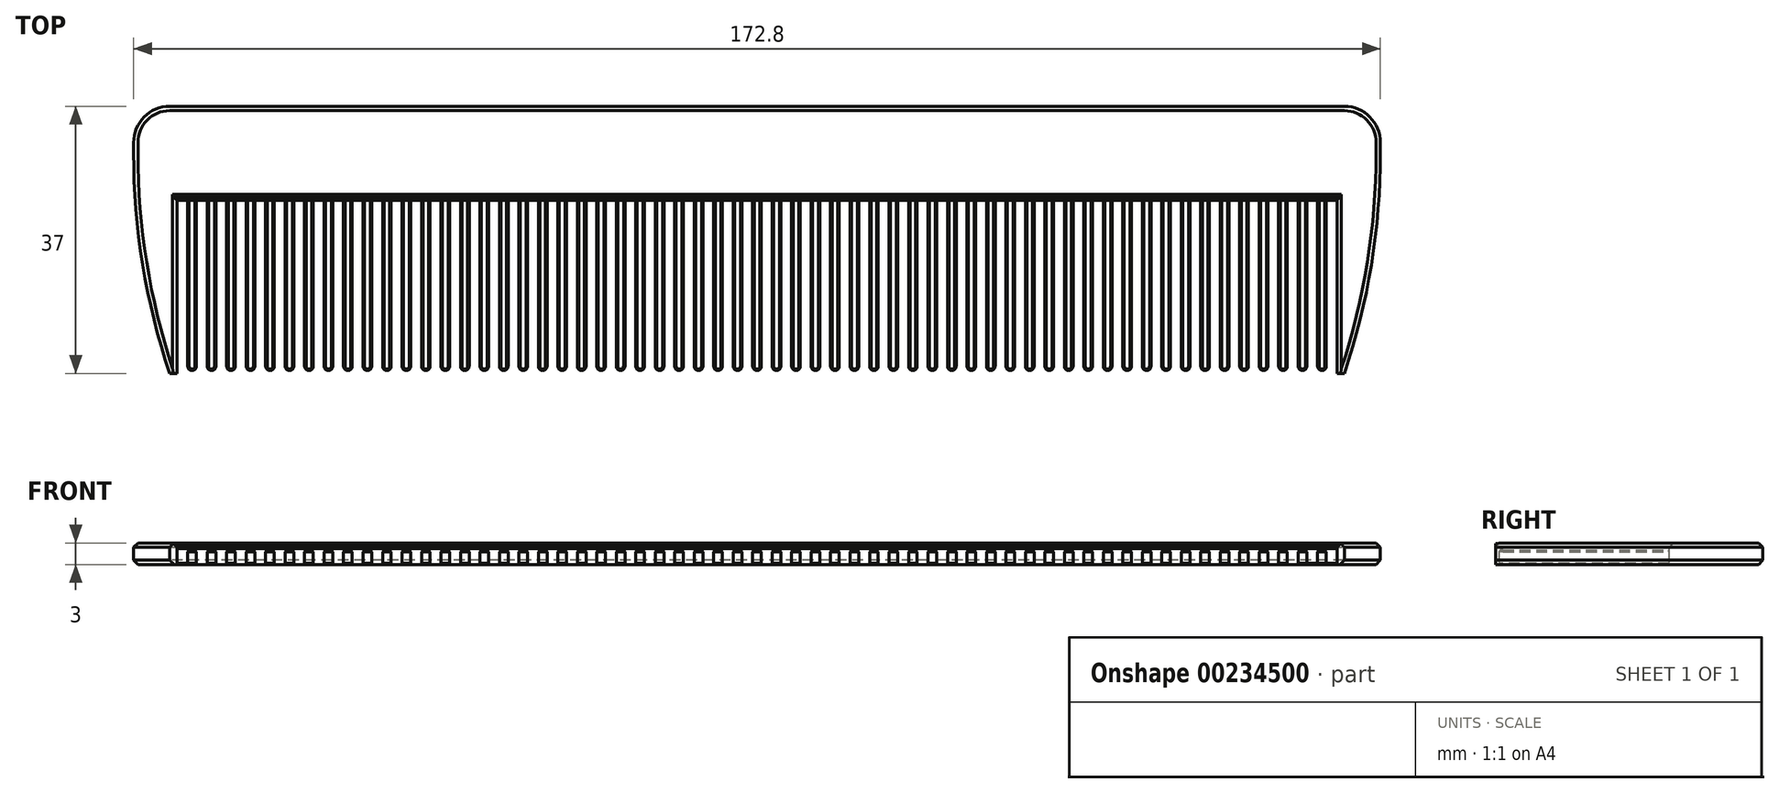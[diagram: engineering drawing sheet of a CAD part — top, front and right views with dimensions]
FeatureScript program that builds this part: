
annotation { "Feature Type Name" : "Feature", "Feature Type Description" : "" }
export const myFeature = defineFeature(function(context is Context, id is Id, definition is map)
    precondition{}
    {
        {
            var Q0;
            Q0=qCreatedBy(makeId("Top.planeOp"),FACE);
            var sketch = newSketch(context, id + "F0", { "sketchPlane" : qUnion([Q0])});
            skLineSegment(sketch, "E0.bottom", {"start": v(-80.4, 6.5) * mm, "end": v(80.4, 6.5) * mm});
            skLineSegment(sketch, "E0.top", {"start": v(-80.4, -6.5) * mm, "end": v(80.4, -6.5) * mm});
            skPoint(sketch, "E0.middle", {"position": v(0, 0) * mm});
            skLineSegment(sketch, "E1", {"start": v(-80.4, -6.5) * mm, "end": v(-80.4, -30.5) * mm});
            skLineSegment(sketch, "E2", {"start": v(-80.4, -30.5) * mm, "end": v(-81.4, -30.5) * mm});
            skArc(sketch, "E3", {"start": v(-81.4, -30.5) * mm, "mid": v(-85.14, -15.45) * mm, "end": v(-86.4, 0) * mm});
            skPoint(sketch, "E4", {"position": v(80.4, 0) * mm});
            skLineSegment(sketch, "E5", {"start": v(80.4, 0) * mm, "end": v(-80.4, 0) * mm, "construction": true});
            skLineSegment(sketch, "E6", {"start": v(-86.4, 0) * mm, "end": v(-86.4, 1.5) * mm});
            skLineSegment(sketch, "E7", {"start": v(-81.4, 6.5) * mm, "end": v(-80.4, 6.5) * mm});
            skPoint(sketch, "E8.visualSharp", {"position": v(-86.4, 6.5) * mm});
            skArc(sketch, "E8.filletArc", {"start": v(-81.4, 6.5) * mm, "mid": v(-84.94, 5.04) * mm, "end": v(-86.4, 1.5) * mm});
            skLineSegment(sketch, "E9", {"start": v(0, 0) * mm, "end": v(0, 6.5) * mm, "construction": true});
            skLineSegment(sketch, "E10.MirrorCS", {"start": v(80.4, -6.5) * mm, "end": v(80.4, -30.5) * mm});
            skLineSegment(sketch, "E11.MirrorCS", {"start": v(80.4, -30.5) * mm, "end": v(81.4, -30.5) * mm});
            skArc(sketch, "E12.MirrorCS", {"start": v(81.4, -30.5) * mm, "mid": v(85.14, -15.45) * mm, "end": v(86.4, 0) * mm});
            skArc(sketch, "E13.MirrorCS", {"start": v(81.4, 6.5) * mm, "mid": v(84.94, 5.04) * mm, "end": v(86.4, 1.5) * mm});
            skLineSegment(sketch, "E14.MirrorCS", {"start": v(86.4, 0) * mm, "end": v(86.4, 1.5) * mm});
            skLineSegment(sketch, "E15.MirrorCS", {"start": v(81.4, 6.5) * mm, "end": v(80.4, 6.5) * mm});
            skSolve(sketch);
        }
        {
            var Q0;
            Q0 = qSketchRegion(id + "F0", true);
            extrude(context, id + "F1", {"entities" : qUnion([Q0]), "depth" : 3 * mm});
        }
        {
            var Q0;
            Q0=qCreatedBy(makeId("Top.planeOp"),FACE);
            var sketch = newSketch(context, id + "F2", { "sketchPlane" : qUnion([Q0])});
            skLineSegment(sketch, "E16.bottom", {"start": v(-78.9, -6.5) * mm, "end": v(-77.7, -6.5) * mm});
            skLineSegment(sketch, "E16.left", {"start": v(-78.9, -6.5) * mm, "end": v(-78.9, -29.5) * mm});
            skLineSegment(sketch, "E16.right", {"start": v(-77.7, -6.5) * mm, "end": v(-77.7, -29.5) * mm});
            skArc(sketch, "E17", {"start": v(-78.9, -29.5) * mm, "mid": v(-78.3, -30.1) * mm, "end": v(-77.7, -29.5) * mm});
            skLineSegment(sketch, "E18.1.0.0", {"start": v(-76.2, -6.5) * mm, "end": v(-76.2, -29.5) * mm});
            skLineSegment(sketch, "E18.1.0.1", {"start": v(-75, -6.5) * mm, "end": v(-75, -29.5) * mm});
            skArc(sketch, "E18.1.0.2", {"start": v(-76.2, -29.5) * mm, "mid": v(-75.6, -30.1) * mm, "end": v(-75, -29.5) * mm});
            skLineSegment(sketch, "E18.1.0.3", {"start": v(-76.2, -6.5) * mm, "end": v(-75, -6.5) * mm});
            skLineSegment(sketch, "E18.2.0.0", {"start": v(-73.5, -6.5) * mm, "end": v(-73.5, -29.5) * mm});
            skLineSegment(sketch, "E18.2.0.1", {"start": v(-72.3, -6.5) * mm, "end": v(-72.3, -29.5) * mm});
            skArc(sketch, "E18.2.0.2", {"start": v(-73.5, -29.5) * mm, "mid": v(-72.9, -30.1) * mm, "end": v(-72.3, -29.5) * mm});
            skLineSegment(sketch, "E18.2.0.3", {"start": v(-73.5, -6.5) * mm, "end": v(-72.3, -6.5) * mm});
            skLineSegment(sketch, "E18.3.0.0", {"start": v(-70.8, -6.5) * mm, "end": v(-70.8, -29.5) * mm});
            skLineSegment(sketch, "E18.3.0.1", {"start": v(-69.6, -6.5) * mm, "end": v(-69.6, -29.5) * mm});
            skArc(sketch, "E18.3.0.2", {"start": v(-70.8, -29.5) * mm, "mid": v(-70.2, -30.1) * mm, "end": v(-69.6, -29.5) * mm});
            skLineSegment(sketch, "E18.3.0.3", {"start": v(-70.8, -6.5) * mm, "end": v(-69.6, -6.5) * mm});
            skLineSegment(sketch, "E18.4.0.0", {"start": v(-68.1, -6.5) * mm, "end": v(-68.1, -29.5) * mm});
            skLineSegment(sketch, "E18.4.0.1", {"start": v(-66.9, -6.5) * mm, "end": v(-66.9, -29.5) * mm});
            skArc(sketch, "E18.4.0.2", {"start": v(-68.1, -29.5) * mm, "mid": v(-67.5, -30.1) * mm, "end": v(-66.9, -29.5) * mm});
            skLineSegment(sketch, "E18.4.0.3", {"start": v(-68.1, -6.5) * mm, "end": v(-66.9, -6.5) * mm});
            skLineSegment(sketch, "E18.5.0.0", {"start": v(-65.4, -6.5) * mm, "end": v(-65.4, -29.5) * mm});
            skLineSegment(sketch, "E18.5.0.1", {"start": v(-64.2, -6.5) * mm, "end": v(-64.2, -29.5) * mm});
            skArc(sketch, "E18.5.0.2", {"start": v(-65.4, -29.5) * mm, "mid": v(-64.8, -30.1) * mm, "end": v(-64.2, -29.5) * mm});
            skLineSegment(sketch, "E18.5.0.3", {"start": v(-65.4, -6.5) * mm, "end": v(-64.2, -6.5) * mm});
            skLineSegment(sketch, "E18.6.0.0", {"start": v(-62.7, -6.5) * mm, "end": v(-62.7, -29.5) * mm});
            skLineSegment(sketch, "E18.6.0.1", {"start": v(-61.5, -6.5) * mm, "end": v(-61.5, -29.5) * mm});
            skArc(sketch, "E18.6.0.2", {"start": v(-62.7, -29.5) * mm, "mid": v(-62.1, -30.1) * mm, "end": v(-61.5, -29.5) * mm});
            skLineSegment(sketch, "E18.6.0.3", {"start": v(-62.7, -6.5) * mm, "end": v(-61.5, -6.5) * mm});
            skLineSegment(sketch, "E18.7.0.0", {"start": v(-60, -6.5) * mm, "end": v(-60, -29.5) * mm});
            skLineSegment(sketch, "E18.7.0.1", {"start": v(-58.8, -6.5) * mm, "end": v(-58.8, -29.5) * mm});
            skArc(sketch, "E18.7.0.2", {"start": v(-60, -29.5) * mm, "mid": v(-59.4, -30.1) * mm, "end": v(-58.8, -29.5) * mm});
            skLineSegment(sketch, "E18.7.0.3", {"start": v(-60, -6.5) * mm, "end": v(-58.8, -6.5) * mm});
            skLineSegment(sketch, "E18.8.0.0", {"start": v(-57.3, -6.5) * mm, "end": v(-57.3, -29.5) * mm});
            skLineSegment(sketch, "E18.8.0.1", {"start": v(-56.1, -6.5) * mm, "end": v(-56.1, -29.5) * mm});
            skArc(sketch, "E18.8.0.2", {"start": v(-57.3, -29.5) * mm, "mid": v(-56.7, -30.1) * mm, "end": v(-56.1, -29.5) * mm});
            skLineSegment(sketch, "E18.8.0.3", {"start": v(-57.3, -6.5) * mm, "end": v(-56.1, -6.5) * mm});
            skLineSegment(sketch, "E18.9.0.0", {"start": v(-54.6, -6.5) * mm, "end": v(-54.6, -29.5) * mm});
            skLineSegment(sketch, "E18.9.0.1", {"start": v(-53.4, -6.5) * mm, "end": v(-53.4, -29.5) * mm});
            skArc(sketch, "E18.9.0.2", {"start": v(-54.6, -29.5) * mm, "mid": v(-54, -30.1) * mm, "end": v(-53.4, -29.5) * mm});
            skLineSegment(sketch, "E18.9.0.3", {"start": v(-54.6, -6.5) * mm, "end": v(-53.4, -6.5) * mm});
            skLineSegment(sketch, "E18.10.0.0", {"start": v(-51.9, -6.5) * mm, "end": v(-51.9, -29.5) * mm});
            skLineSegment(sketch, "E18.10.0.1", {"start": v(-50.7, -6.5) * mm, "end": v(-50.7, -29.5) * mm});
            skArc(sketch, "E18.10.0.2", {"start": v(-51.9, -29.5) * mm, "mid": v(-51.3, -30.1) * mm, "end": v(-50.7, -29.5) * mm});
            skLineSegment(sketch, "E18.10.0.3", {"start": v(-51.9, -6.5) * mm, "end": v(-50.7, -6.5) * mm});
            skLineSegment(sketch, "E18.11.0.0", {"start": v(-49.2, -6.5) * mm, "end": v(-49.2, -29.5) * mm});
            skLineSegment(sketch, "E18.11.0.1", {"start": v(-48, -6.5) * mm, "end": v(-48, -29.5) * mm});
            skArc(sketch, "E18.11.0.2", {"start": v(-49.2, -29.5) * mm, "mid": v(-48.6, -30.1) * mm, "end": v(-48, -29.5) * mm});
            skLineSegment(sketch, "E18.11.0.3", {"start": v(-49.2, -6.5) * mm, "end": v(-48, -6.5) * mm});
            skLineSegment(sketch, "E18.12.0.0", {"start": v(-46.5, -6.5) * mm, "end": v(-46.5, -29.5) * mm});
            skLineSegment(sketch, "E18.12.0.1", {"start": v(-45.3, -6.5) * mm, "end": v(-45.3, -29.5) * mm});
            skArc(sketch, "E18.12.0.2", {"start": v(-46.5, -29.5) * mm, "mid": v(-45.9, -30.1) * mm, "end": v(-45.3, -29.5) * mm});
            skLineSegment(sketch, "E18.12.0.3", {"start": v(-46.5, -6.5) * mm, "end": v(-45.3, -6.5) * mm});
            skLineSegment(sketch, "E18.13.0.0", {"start": v(-43.8, -6.5) * mm, "end": v(-43.8, -29.5) * mm});
            skLineSegment(sketch, "E18.13.0.1", {"start": v(-42.6, -6.5) * mm, "end": v(-42.6, -29.5) * mm});
            skArc(sketch, "E18.13.0.2", {"start": v(-43.8, -29.5) * mm, "mid": v(-43.2, -30.1) * mm, "end": v(-42.6, -29.5) * mm});
            skLineSegment(sketch, "E18.13.0.3", {"start": v(-43.8, -6.5) * mm, "end": v(-42.6, -6.5) * mm});
            skLineSegment(sketch, "E18.14.0.0", {"start": v(-41.1, -6.5) * mm, "end": v(-41.1, -29.5) * mm});
            skLineSegment(sketch, "E18.14.0.1", {"start": v(-39.9, -6.5) * mm, "end": v(-39.9, -29.5) * mm});
            skArc(sketch, "E18.14.0.2", {"start": v(-41.1, -29.5) * mm, "mid": v(-40.5, -30.1) * mm, "end": v(-39.9, -29.5) * mm});
            skLineSegment(sketch, "E18.14.0.3", {"start": v(-41.1, -6.5) * mm, "end": v(-39.9, -6.5) * mm});
            skLineSegment(sketch, "E18.15.0.0", {"start": v(-38.4, -6.5) * mm, "end": v(-38.4, -29.5) * mm});
            skLineSegment(sketch, "E18.15.0.1", {"start": v(-37.2, -6.5) * mm, "end": v(-37.2, -29.5) * mm});
            skArc(sketch, "E18.15.0.2", {"start": v(-38.4, -29.5) * mm, "mid": v(-37.8, -30.1) * mm, "end": v(-37.2, -29.5) * mm});
            skLineSegment(sketch, "E18.15.0.3", {"start": v(-38.4, -6.5) * mm, "end": v(-37.2, -6.5) * mm});
            skLineSegment(sketch, "E18.16.0.0", {"start": v(-35.7, -6.5) * mm, "end": v(-35.7, -29.5) * mm});
            skLineSegment(sketch, "E18.16.0.1", {"start": v(-34.5, -6.5) * mm, "end": v(-34.5, -29.5) * mm});
            skArc(sketch, "E18.16.0.2", {"start": v(-35.7, -29.5) * mm, "mid": v(-35.1, -30.1) * mm, "end": v(-34.5, -29.5) * mm});
            skLineSegment(sketch, "E18.16.0.3", {"start": v(-35.7, -6.5) * mm, "end": v(-34.5, -6.5) * mm});
            skLineSegment(sketch, "E18.17.0.0", {"start": v(-33, -6.5) * mm, "end": v(-33, -29.5) * mm});
            skLineSegment(sketch, "E18.17.0.1", {"start": v(-31.8, -6.5) * mm, "end": v(-31.8, -29.5) * mm});
            skArc(sketch, "E18.17.0.2", {"start": v(-33, -29.5) * mm, "mid": v(-32.4, -30.1) * mm, "end": v(-31.8, -29.5) * mm});
            skLineSegment(sketch, "E18.17.0.3", {"start": v(-33, -6.5) * mm, "end": v(-31.8, -6.5) * mm});
            skLineSegment(sketch, "E18.18.0.0", {"start": v(-30.3, -6.5) * mm, "end": v(-30.3, -29.5) * mm});
            skLineSegment(sketch, "E18.18.0.1", {"start": v(-29.1, -6.5) * mm, "end": v(-29.1, -29.5) * mm});
            skArc(sketch, "E18.18.0.2", {"start": v(-30.3, -29.5) * mm, "mid": v(-29.7, -30.1) * mm, "end": v(-29.1, -29.5) * mm});
            skLineSegment(sketch, "E18.18.0.3", {"start": v(-30.3, -6.5) * mm, "end": v(-29.1, -6.5) * mm});
            skLineSegment(sketch, "E18.19.0.0", {"start": v(-27.6, -6.5) * mm, "end": v(-27.6, -29.5) * mm});
            skLineSegment(sketch, "E18.19.0.1", {"start": v(-26.4, -6.5) * mm, "end": v(-26.4, -29.5) * mm});
            skArc(sketch, "E18.19.0.2", {"start": v(-27.6, -29.5) * mm, "mid": v(-27, -30.1) * mm, "end": v(-26.4, -29.5) * mm});
            skLineSegment(sketch, "E18.19.0.3", {"start": v(-27.6, -6.5) * mm, "end": v(-26.4, -6.5) * mm});
            skLineSegment(sketch, "E18.20.0.0", {"start": v(-24.9, -6.5) * mm, "end": v(-24.9, -29.5) * mm});
            skLineSegment(sketch, "E18.20.0.1", {"start": v(-23.7, -6.5) * mm, "end": v(-23.7, -29.5) * mm});
            skArc(sketch, "E18.20.0.2", {"start": v(-24.9, -29.5) * mm, "mid": v(-24.3, -30.1) * mm, "end": v(-23.7, -29.5) * mm});
            skLineSegment(sketch, "E18.20.0.3", {"start": v(-24.9, -6.5) * mm, "end": v(-23.7, -6.5) * mm});
            skLineSegment(sketch, "E18.21.0.0", {"start": v(-22.2, -6.5) * mm, "end": v(-22.2, -29.5) * mm});
            skLineSegment(sketch, "E18.21.0.1", {"start": v(-21, -6.5) * mm, "end": v(-21, -29.5) * mm});
            skArc(sketch, "E18.21.0.2", {"start": v(-22.2, -29.5) * mm, "mid": v(-21.6, -30.1) * mm, "end": v(-21, -29.5) * mm});
            skLineSegment(sketch, "E18.21.0.3", {"start": v(-22.2, -6.5) * mm, "end": v(-21, -6.5) * mm});
            skLineSegment(sketch, "E18.22.0.0", {"start": v(-19.5, -6.5) * mm, "end": v(-19.5, -29.5) * mm});
            skLineSegment(sketch, "E18.22.0.1", {"start": v(-18.3, -6.5) * mm, "end": v(-18.3, -29.5) * mm});
            skArc(sketch, "E18.22.0.2", {"start": v(-19.5, -29.5) * mm, "mid": v(-18.9, -30.1) * mm, "end": v(-18.3, -29.5) * mm});
            skLineSegment(sketch, "E18.22.0.3", {"start": v(-19.5, -6.5) * mm, "end": v(-18.3, -6.5) * mm});
            skLineSegment(sketch, "E18.23.0.0", {"start": v(-16.8, -6.5) * mm, "end": v(-16.8, -29.5) * mm});
            skLineSegment(sketch, "E18.23.0.1", {"start": v(-15.6, -6.5) * mm, "end": v(-15.6, -29.5) * mm});
            skArc(sketch, "E18.23.0.2", {"start": v(-16.8, -29.5) * mm, "mid": v(-16.2, -30.1) * mm, "end": v(-15.6, -29.5) * mm});
            skLineSegment(sketch, "E18.23.0.3", {"start": v(-16.8, -6.5) * mm, "end": v(-15.6, -6.5) * mm});
            skLineSegment(sketch, "E18.24.0.0", {"start": v(-14.1, -6.5) * mm, "end": v(-14.1, -29.5) * mm});
            skLineSegment(sketch, "E18.24.0.1", {"start": v(-12.9, -6.5) * mm, "end": v(-12.9, -29.5) * mm});
            skArc(sketch, "E18.24.0.2", {"start": v(-14.1, -29.5) * mm, "mid": v(-13.5, -30.1) * mm, "end": v(-12.9, -29.5) * mm});
            skLineSegment(sketch, "E18.24.0.3", {"start": v(-14.1, -6.5) * mm, "end": v(-12.9, -6.5) * mm});
            skLineSegment(sketch, "E18.25.0.0", {"start": v(-11.4, -6.5) * mm, "end": v(-11.4, -29.5) * mm});
            skLineSegment(sketch, "E18.25.0.1", {"start": v(-10.2, -6.5) * mm, "end": v(-10.2, -29.5) * mm});
            skArc(sketch, "E18.25.0.2", {"start": v(-11.4, -29.5) * mm, "mid": v(-10.8, -30.1) * mm, "end": v(-10.2, -29.5) * mm});
            skLineSegment(sketch, "E18.25.0.3", {"start": v(-11.4, -6.5) * mm, "end": v(-10.2, -6.5) * mm});
            skLineSegment(sketch, "E18.26.0.0", {"start": v(-8.7, -6.5) * mm, "end": v(-8.7, -29.5) * mm});
            skLineSegment(sketch, "E18.26.0.1", {"start": v(-7.5, -6.5) * mm, "end": v(-7.5, -29.5) * mm});
            skArc(sketch, "E18.26.0.2", {"start": v(-8.7, -29.5) * mm, "mid": v(-8.1, -30.1) * mm, "end": v(-7.5, -29.5) * mm});
            skLineSegment(sketch, "E18.26.0.3", {"start": v(-8.7, -6.5) * mm, "end": v(-7.5, -6.5) * mm});
            skLineSegment(sketch, "E18.27.0.0", {"start": v(-6, -6.5) * mm, "end": v(-6, -29.5) * mm});
            skLineSegment(sketch, "E18.27.0.1", {"start": v(-4.8, -6.5) * mm, "end": v(-4.8, -29.5) * mm});
            skArc(sketch, "E18.27.0.2", {"start": v(-6, -29.5) * mm, "mid": v(-5.4, -30.1) * mm, "end": v(-4.8, -29.5) * mm});
            skLineSegment(sketch, "E18.27.0.3", {"start": v(-6, -6.5) * mm, "end": v(-4.8, -6.5) * mm});
            skLineSegment(sketch, "E18.28.0.0", {"start": v(-3.3, -6.5) * mm, "end": v(-3.3, -29.5) * mm});
            skLineSegment(sketch, "E18.28.0.1", {"start": v(-2.1, -6.5) * mm, "end": v(-2.1, -29.5) * mm});
            skArc(sketch, "E18.28.0.2", {"start": v(-3.3, -29.5) * mm, "mid": v(-2.7, -30.1) * mm, "end": v(-2.1, -29.5) * mm});
            skLineSegment(sketch, "E18.28.0.3", {"start": v(-3.3, -6.5) * mm, "end": v(-2.1, -6.5) * mm});
            skLineSegment(sketch, "E18.29.0.0", {"start": v(-0.6, -6.5) * mm, "end": v(-0.6, -29.5) * mm});
            skLineSegment(sketch, "E18.29.0.1", {"start": v(0.6, -6.5) * mm, "end": v(0.6, -29.5) * mm});
            skArc(sketch, "E18.29.0.2", {"start": v(-0.6, -29.5) * mm, "mid": v(0, -30.1) * mm, "end": v(0.6, -29.5) * mm});
            skLineSegment(sketch, "E18.29.0.3", {"start": v(-0.6, -6.5) * mm, "end": v(0.6, -6.5) * mm});
            skLineSegment(sketch, "E18.30.0.0", {"start": v(2.1, -6.5) * mm, "end": v(2.1, -29.5) * mm});
            skLineSegment(sketch, "E18.30.0.1", {"start": v(3.3, -6.5) * mm, "end": v(3.3, -29.5) * mm});
            skArc(sketch, "E18.30.0.2", {"start": v(2.1, -29.5) * mm, "mid": v(2.7, -30.1) * mm, "end": v(3.3, -29.5) * mm});
            skLineSegment(sketch, "E18.30.0.3", {"start": v(2.1, -6.5) * mm, "end": v(3.3, -6.5) * mm});
            skLineSegment(sketch, "E18.31.0.0", {"start": v(4.8, -6.5) * mm, "end": v(4.8, -29.5) * mm});
            skLineSegment(sketch, "E18.31.0.1", {"start": v(6, -6.5) * mm, "end": v(6, -29.5) * mm});
            skArc(sketch, "E18.31.0.2", {"start": v(4.8, -29.5) * mm, "mid": v(5.4, -30.1) * mm, "end": v(6, -29.5) * mm});
            skLineSegment(sketch, "E18.31.0.3", {"start": v(4.8, -6.5) * mm, "end": v(6, -6.5) * mm});
            skLineSegment(sketch, "E18.32.0.0", {"start": v(7.5, -6.5) * mm, "end": v(7.5, -29.5) * mm});
            skLineSegment(sketch, "E18.32.0.1", {"start": v(8.7, -6.5) * mm, "end": v(8.7, -29.5) * mm});
            skArc(sketch, "E18.32.0.2", {"start": v(7.5, -29.5) * mm, "mid": v(8.1, -30.1) * mm, "end": v(8.7, -29.5) * mm});
            skLineSegment(sketch, "E18.32.0.3", {"start": v(7.5, -6.5) * mm, "end": v(8.7, -6.5) * mm});
            skLineSegment(sketch, "E18.33.0.0", {"start": v(10.2, -6.5) * mm, "end": v(10.2, -29.5) * mm});
            skLineSegment(sketch, "E18.33.0.1", {"start": v(11.4, -6.5) * mm, "end": v(11.4, -29.5) * mm});
            skArc(sketch, "E18.33.0.2", {"start": v(10.2, -29.5) * mm, "mid": v(10.8, -30.1) * mm, "end": v(11.4, -29.5) * mm});
            skLineSegment(sketch, "E18.33.0.3", {"start": v(10.2, -6.5) * mm, "end": v(11.4, -6.5) * mm});
            skLineSegment(sketch, "E18.34.0.0", {"start": v(12.9, -6.5) * mm, "end": v(12.9, -29.5) * mm});
            skLineSegment(sketch, "E18.34.0.1", {"start": v(14.1, -6.5) * mm, "end": v(14.1, -29.5) * mm});
            skArc(sketch, "E18.34.0.2", {"start": v(12.9, -29.5) * mm, "mid": v(13.5, -30.1) * mm, "end": v(14.1, -29.5) * mm});
            skLineSegment(sketch, "E18.34.0.3", {"start": v(12.9, -6.5) * mm, "end": v(14.1, -6.5) * mm});
            skLineSegment(sketch, "E18.35.0.0", {"start": v(15.6, -6.5) * mm, "end": v(15.6, -29.5) * mm});
            skLineSegment(sketch, "E18.35.0.1", {"start": v(16.8, -6.5) * mm, "end": v(16.8, -29.5) * mm});
            skArc(sketch, "E18.35.0.2", {"start": v(15.6, -29.5) * mm, "mid": v(16.2, -30.1) * mm, "end": v(16.8, -29.5) * mm});
            skLineSegment(sketch, "E18.35.0.3", {"start": v(15.6, -6.5) * mm, "end": v(16.8, -6.5) * mm});
            skLineSegment(sketch, "E18.36.0.0", {"start": v(18.3, -6.5) * mm, "end": v(18.3, -29.5) * mm});
            skLineSegment(sketch, "E18.36.0.1", {"start": v(19.5, -6.5) * mm, "end": v(19.5, -29.5) * mm});
            skArc(sketch, "E18.36.0.2", {"start": v(18.3, -29.5) * mm, "mid": v(18.9, -30.1) * mm, "end": v(19.5, -29.5) * mm});
            skLineSegment(sketch, "E18.36.0.3", {"start": v(18.3, -6.5) * mm, "end": v(19.5, -6.5) * mm});
            skLineSegment(sketch, "E18.37.0.0", {"start": v(21, -6.5) * mm, "end": v(21, -29.5) * mm});
            skLineSegment(sketch, "E18.37.0.1", {"start": v(22.2, -6.5) * mm, "end": v(22.2, -29.5) * mm});
            skArc(sketch, "E18.37.0.2", {"start": v(21, -29.5) * mm, "mid": v(21.6, -30.1) * mm, "end": v(22.2, -29.5) * mm});
            skLineSegment(sketch, "E18.37.0.3", {"start": v(21, -6.5) * mm, "end": v(22.2, -6.5) * mm});
            skLineSegment(sketch, "E18.38.0.0", {"start": v(23.7, -6.5) * mm, "end": v(23.7, -29.5) * mm});
            skLineSegment(sketch, "E18.38.0.1", {"start": v(24.9, -6.5) * mm, "end": v(24.9, -29.5) * mm});
            skArc(sketch, "E18.38.0.2", {"start": v(23.7, -29.5) * mm, "mid": v(24.3, -30.1) * mm, "end": v(24.9, -29.5) * mm});
            skLineSegment(sketch, "E18.38.0.3", {"start": v(23.7, -6.5) * mm, "end": v(24.9, -6.5) * mm});
            skLineSegment(sketch, "E18.39.0.0", {"start": v(26.4, -6.5) * mm, "end": v(26.4, -29.5) * mm});
            skLineSegment(sketch, "E18.39.0.1", {"start": v(27.6, -6.5) * mm, "end": v(27.6, -29.5) * mm});
            skArc(sketch, "E18.39.0.2", {"start": v(26.4, -29.5) * mm, "mid": v(27, -30.1) * mm, "end": v(27.6, -29.5) * mm});
            skLineSegment(sketch, "E18.39.0.3", {"start": v(26.4, -6.5) * mm, "end": v(27.6, -6.5) * mm});
            skLineSegment(sketch, "E18.40.0.0", {"start": v(29.1, -6.5) * mm, "end": v(29.1, -29.5) * mm});
            skLineSegment(sketch, "E18.40.0.1", {"start": v(30.3, -6.5) * mm, "end": v(30.3, -29.5) * mm});
            skArc(sketch, "E18.40.0.2", {"start": v(29.1, -29.5) * mm, "mid": v(29.7, -30.1) * mm, "end": v(30.3, -29.5) * mm});
            skLineSegment(sketch, "E18.40.0.3", {"start": v(29.1, -6.5) * mm, "end": v(30.3, -6.5) * mm});
            skLineSegment(sketch, "E18.41.0.0", {"start": v(31.8, -6.5) * mm, "end": v(31.8, -29.5) * mm});
            skLineSegment(sketch, "E18.41.0.1", {"start": v(33, -6.5) * mm, "end": v(33, -29.5) * mm});
            skArc(sketch, "E18.41.0.2", {"start": v(31.8, -29.5) * mm, "mid": v(32.4, -30.1) * mm, "end": v(33, -29.5) * mm});
            skLineSegment(sketch, "E18.41.0.3", {"start": v(31.8, -6.5) * mm, "end": v(33, -6.5) * mm});
            skLineSegment(sketch, "E18.42.0.0", {"start": v(34.5, -6.5) * mm, "end": v(34.5, -29.5) * mm});
            skLineSegment(sketch, "E18.42.0.1", {"start": v(35.7, -6.5) * mm, "end": v(35.7, -29.5) * mm});
            skArc(sketch, "E18.42.0.2", {"start": v(34.5, -29.5) * mm, "mid": v(35.1, -30.1) * mm, "end": v(35.7, -29.5) * mm});
            skLineSegment(sketch, "E18.42.0.3", {"start": v(34.5, -6.5) * mm, "end": v(35.7, -6.5) * mm});
            skLineSegment(sketch, "E18.43.0.0", {"start": v(37.2, -6.5) * mm, "end": v(37.2, -29.5) * mm});
            skLineSegment(sketch, "E18.43.0.1", {"start": v(38.4, -6.5) * mm, "end": v(38.4, -29.5) * mm});
            skArc(sketch, "E18.43.0.2", {"start": v(37.2, -29.5) * mm, "mid": v(37.8, -30.1) * mm, "end": v(38.4, -29.5) * mm});
            skLineSegment(sketch, "E18.43.0.3", {"start": v(37.2, -6.5) * mm, "end": v(38.4, -6.5) * mm});
            skLineSegment(sketch, "E18.44.0.0", {"start": v(39.9, -6.5) * mm, "end": v(39.9, -29.5) * mm});
            skLineSegment(sketch, "E18.44.0.1", {"start": v(41.1, -6.5) * mm, "end": v(41.1, -29.5) * mm});
            skArc(sketch, "E18.44.0.2", {"start": v(39.9, -29.5) * mm, "mid": v(40.5, -30.1) * mm, "end": v(41.1, -29.5) * mm});
            skLineSegment(sketch, "E18.44.0.3", {"start": v(39.9, -6.5) * mm, "end": v(41.1, -6.5) * mm});
            skLineSegment(sketch, "E18.45.0.0", {"start": v(42.6, -6.5) * mm, "end": v(42.6, -29.5) * mm});
            skLineSegment(sketch, "E18.45.0.1", {"start": v(43.8, -6.5) * mm, "end": v(43.8, -29.5) * mm});
            skArc(sketch, "E18.45.0.2", {"start": v(42.6, -29.5) * mm, "mid": v(43.2, -30.1) * mm, "end": v(43.8, -29.5) * mm});
            skLineSegment(sketch, "E18.45.0.3", {"start": v(42.6, -6.5) * mm, "end": v(43.8, -6.5) * mm});
            skLineSegment(sketch, "E18.46.0.0", {"start": v(45.3, -6.5) * mm, "end": v(45.3, -29.5) * mm});
            skLineSegment(sketch, "E18.46.0.1", {"start": v(46.5, -6.5) * mm, "end": v(46.5, -29.5) * mm});
            skArc(sketch, "E18.46.0.2", {"start": v(45.3, -29.5) * mm, "mid": v(45.9, -30.1) * mm, "end": v(46.5, -29.5) * mm});
            skLineSegment(sketch, "E18.46.0.3", {"start": v(45.3, -6.5) * mm, "end": v(46.5, -6.5) * mm});
            skLineSegment(sketch, "E18.47.0.0", {"start": v(48, -6.5) * mm, "end": v(48, -29.5) * mm});
            skLineSegment(sketch, "E18.47.0.1", {"start": v(49.2, -6.5) * mm, "end": v(49.2, -29.5) * mm});
            skArc(sketch, "E18.47.0.2", {"start": v(48, -29.5) * mm, "mid": v(48.6, -30.1) * mm, "end": v(49.2, -29.5) * mm});
            skLineSegment(sketch, "E18.47.0.3", {"start": v(48, -6.5) * mm, "end": v(49.2, -6.5) * mm});
            skLineSegment(sketch, "E18.48.0.0", {"start": v(50.7, -6.5) * mm, "end": v(50.7, -29.5) * mm});
            skLineSegment(sketch, "E18.48.0.1", {"start": v(51.9, -6.5) * mm, "end": v(51.9, -29.5) * mm});
            skArc(sketch, "E18.48.0.2", {"start": v(50.7, -29.5) * mm, "mid": v(51.3, -30.1) * mm, "end": v(51.9, -29.5) * mm});
            skLineSegment(sketch, "E18.48.0.3", {"start": v(50.7, -6.5) * mm, "end": v(51.9, -6.5) * mm});
            skLineSegment(sketch, "E18.49.0.0", {"start": v(53.4, -6.5) * mm, "end": v(53.4, -29.5) * mm});
            skLineSegment(sketch, "E18.49.0.1", {"start": v(54.6, -6.5) * mm, "end": v(54.6, -29.5) * mm});
            skArc(sketch, "E18.49.0.2", {"start": v(53.4, -29.5) * mm, "mid": v(54, -30.1) * mm, "end": v(54.6, -29.5) * mm});
            skLineSegment(sketch, "E18.49.0.3", {"start": v(53.4, -6.5) * mm, "end": v(54.6, -6.5) * mm});
            skLineSegment(sketch, "E18.50.0.0", {"start": v(56.1, -6.5) * mm, "end": v(56.1, -29.5) * mm});
            skLineSegment(sketch, "E18.50.0.1", {"start": v(57.3, -6.5) * mm, "end": v(57.3, -29.5) * mm});
            skArc(sketch, "E18.50.0.2", {"start": v(56.1, -29.5) * mm, "mid": v(56.7, -30.1) * mm, "end": v(57.3, -29.5) * mm});
            skLineSegment(sketch, "E18.50.0.3", {"start": v(56.1, -6.5) * mm, "end": v(57.3, -6.5) * mm});
            skLineSegment(sketch, "E18.51.0.0", {"start": v(58.8, -6.5) * mm, "end": v(58.8, -29.5) * mm});
            skLineSegment(sketch, "E18.51.0.1", {"start": v(60, -6.5) * mm, "end": v(60, -29.5) * mm});
            skArc(sketch, "E18.51.0.2", {"start": v(58.8, -29.5) * mm, "mid": v(59.4, -30.1) * mm, "end": v(60, -29.5) * mm});
            skLineSegment(sketch, "E18.51.0.3", {"start": v(58.8, -6.5) * mm, "end": v(60, -6.5) * mm});
            skLineSegment(sketch, "E18.52.0.0", {"start": v(61.5, -6.5) * mm, "end": v(61.5, -29.5) * mm});
            skLineSegment(sketch, "E18.52.0.1", {"start": v(62.7, -6.5) * mm, "end": v(62.7, -29.5) * mm});
            skArc(sketch, "E18.52.0.2", {"start": v(61.5, -29.5) * mm, "mid": v(62.1, -30.1) * mm, "end": v(62.7, -29.5) * mm});
            skLineSegment(sketch, "E18.52.0.3", {"start": v(61.5, -6.5) * mm, "end": v(62.7, -6.5) * mm});
            skLineSegment(sketch, "E18.53.0.0", {"start": v(64.2, -6.5) * mm, "end": v(64.2, -29.5) * mm});
            skLineSegment(sketch, "E18.53.0.1", {"start": v(65.4, -6.5) * mm, "end": v(65.4, -29.5) * mm});
            skArc(sketch, "E18.53.0.2", {"start": v(64.2, -29.5) * mm, "mid": v(64.8, -30.1) * mm, "end": v(65.4, -29.5) * mm});
            skLineSegment(sketch, "E18.53.0.3", {"start": v(64.2, -6.5) * mm, "end": v(65.4, -6.5) * mm});
            skLineSegment(sketch, "E18.54.0.0", {"start": v(66.9, -6.5) * mm, "end": v(66.9, -29.5) * mm});
            skLineSegment(sketch, "E18.54.0.1", {"start": v(68.1, -6.5) * mm, "end": v(68.1, -29.5) * mm});
            skArc(sketch, "E18.54.0.2", {"start": v(66.9, -29.5) * mm, "mid": v(67.5, -30.1) * mm, "end": v(68.1, -29.5) * mm});
            skLineSegment(sketch, "E18.54.0.3", {"start": v(66.9, -6.5) * mm, "end": v(68.1, -6.5) * mm});
            skLineSegment(sketch, "E18.55.0.0", {"start": v(69.6, -6.5) * mm, "end": v(69.6, -29.5) * mm});
            skLineSegment(sketch, "E18.55.0.1", {"start": v(70.8, -6.5) * mm, "end": v(70.8, -29.5) * mm});
            skArc(sketch, "E18.55.0.2", {"start": v(69.6, -29.5) * mm, "mid": v(70.2, -30.1) * mm, "end": v(70.8, -29.5) * mm});
            skLineSegment(sketch, "E18.55.0.3", {"start": v(69.6, -6.5) * mm, "end": v(70.8, -6.5) * mm});
            skLineSegment(sketch, "E18.56.0.0", {"start": v(72.3, -6.5) * mm, "end": v(72.3, -29.5) * mm});
            skLineSegment(sketch, "E18.56.0.1", {"start": v(73.5, -6.5) * mm, "end": v(73.5, -29.5) * mm});
            skArc(sketch, "E18.56.0.2", {"start": v(72.3, -29.5) * mm, "mid": v(72.9, -30.1) * mm, "end": v(73.5, -29.5) * mm});
            skLineSegment(sketch, "E18.56.0.3", {"start": v(72.3, -6.5) * mm, "end": v(73.5, -6.5) * mm});
            skLineSegment(sketch, "E18.57.0.0", {"start": v(75, -6.5) * mm, "end": v(75, -29.5) * mm});
            skLineSegment(sketch, "E18.57.0.1", {"start": v(76.2, -6.5) * mm, "end": v(76.2, -29.5) * mm});
            skArc(sketch, "E18.57.0.2", {"start": v(75, -29.5) * mm, "mid": v(75.6, -30.1) * mm, "end": v(76.2, -29.5) * mm});
            skLineSegment(sketch, "E18.57.0.3", {"start": v(75, -6.5) * mm, "end": v(76.2, -6.5) * mm});
            skLineSegment(sketch, "E18.58.0.0", {"start": v(77.7, -6.5) * mm, "end": v(77.7, -29.5) * mm});
            skLineSegment(sketch, "E18.58.0.1", {"start": v(78.9, -6.5) * mm, "end": v(78.9, -29.5) * mm});
            skArc(sketch, "E18.58.0.2", {"start": v(77.7, -29.5) * mm, "mid": v(78.3, -30.1) * mm, "end": v(78.9, -29.5) * mm});
            skLineSegment(sketch, "E18.58.0.3", {"start": v(77.7, -6.5) * mm, "end": v(78.9, -6.5) * mm});
            skLineSegment(sketch, "E18.direction1", {"start": v(-78.9, -29.5) * mm, "end": v(-76.2, -29.5) * mm, "construction": true});
            skSolve(sketch);
        }
        {
            var Q0;
            Q0 = qSketchRegion(id + "F2", true);
            extrude(context, id + "F3", {"entities" : qUnion([Q0]), "operationType" : NewBodyOperationType.ADD, "depth" : 2 * mm});
        }
        {
            var Q0;
            Q0=makeQuery(id+"F1.opExtrude","CAP_FACE",FACE,{"disambiguationData":[OSD([sQuery(id+"F0.wireOp",EDGE,"E0.bottom"),sQuery(id+"F0.wireOp",EDGE,"E0.top"),sQuery(id+"F0.wireOp",EDGE,"E1"),sQuery(id+"F0.wireOp",EDGE,"E2"),sQuery(id+"F0.wireOp",EDGE,"E3"),sQuery(id+"F0.wireOp",EDGE,"E6"),sQuery(id+"F0.wireOp",EDGE,"E7"),sQuery(id+"F0.wireOp",EDGE,"E8.filletArc"),sQuery(id+"F0.wireOp",EDGE,"E10.MirrorCS"),sQuery(id+"F0.wireOp",EDGE,"E11.MirrorCS"),sQuery(id+"F0.wireOp",EDGE,"E12.MirrorCS"),sQuery(id+"F0.wireOp",EDGE,"E13.MirrorCS"),sQuery(id+"F0.wireOp",EDGE,"E14.MirrorCS"),sQuery(id+"F0.wireOp",EDGE,"E15.MirrorCS")])],"isStart":false});
            chamfer(context, id + "F4", {"entities" : qUnion([Q0]), "width" : 0.6 * mm, "tangentPropagation" : true});
        }
        {
            var Q0;
            Q0=makeQuery(id+"F1.opExtrude","CAP_EDGE",EDGE,{"disambiguationData":[OSD([sQuery(id+"F0.wireOp",EDGE,"E0.bottom"),sQuery(id+"F0.wireOp",EDGE,"E7"),sQuery(id+"F0.wireOp",EDGE,"E15.MirrorCS")])],"isStart":true});
            var Q1;
            Q1=makeQuery(id+"F1.opExtrude","CAP_EDGE",EDGE,{"disambiguationData":[OSD([sQuery(id+"F0.wireOp",EDGE,"E8.filletArc")])],"isStart":true});
            var Q2;
            Q2=makeQuery(id+"F1.opExtrude","CAP_EDGE",EDGE,{"disambiguationData":[OSD([sQuery(id+"F0.wireOp",EDGE,"E3")])],"isStart":true});
            var Q3;
            Q3=makeQuery(id+"F1.opExtrude","CAP_EDGE",EDGE,{"disambiguationData":[OSD([sQuery(id+"F0.wireOp",EDGE,"E13.MirrorCS")])],"isStart":true});
            var Q4;
            Q4=makeQuery(id+"F1.opExtrude","CAP_EDGE",EDGE,{"disambiguationData":[OSD([sQuery(id+"F0.wireOp",EDGE,"E6")])],"isStart":true});
            chamfer(context, id + "F5", {"entities" : qUnion([Q0, Q1, Q2, Q3, Q4]), "width" : 0.6 * mm, "tangentPropagation" : true});
        }
        {
            var Q0;
            {var subQ1=sQuery(id+"F0.wireOp",EDGE,"E1");var subQ2=sQuery(id+"F0.wireOp",EDGE,"E0.top");Q0=makeQuery(id+"F3.boolean.opBoolean","SPLIT",EDGE,{"disambiguationData":[TD([makeQuery(id+"F1.opExtrude","SWEPT_FACE",FACE,{"disambiguationData":[OSD([subQ1])]})])],"derivedFrom":makeQuery(id+"F1.opExtrude","CAP_EDGE",EDGE,{"disambiguationData":[OSD([subQ2])],"isStart":true})});}
            var Q1;
            {var subQ1=sQuery(id+"F2.wireOp",EDGE,"E18.40.0.1");var subQ2=sQuery(id+"F0.wireOp",EDGE,"E0.top");Q1=makeQuery(id+"F3.boolean.opBoolean","SPLIT",EDGE,{"disambiguationData":[TD([makeQuery(id+"F3.opExtrude","SWEPT_FACE",FACE,{"disambiguationData":[OSD([subQ1])]})])],"derivedFrom":makeQuery(id+"F1.opExtrude","CAP_EDGE",EDGE,{"disambiguationData":[OSD([subQ2])],"isStart":true})});}
            var Q2;
            {var subQ0=sQuery(id+"F2.wireOp",EDGE,"E18.30.0.1");var subQ2=sQuery(id+"F0.wireOp",EDGE,"E0.top");Q2=makeQuery(id+"F3.boolean.opBoolean","SPLIT",EDGE,{"disambiguationData":[TD([makeQuery(id+"F3.opExtrude","SWEPT_FACE",FACE,{"disambiguationData":[OSD([subQ0])]})])],"derivedFrom":makeQuery(id+"F1.opExtrude","CAP_EDGE",EDGE,{"disambiguationData":[OSD([subQ2])],"isStart":true})});}
            var Q3;
            {var subQ0=sQuery(id+"F2.wireOp",EDGE,"E18.44.0.1");var subQ2=sQuery(id+"F0.wireOp",EDGE,"E0.top");Q3=makeQuery(id+"F3.boolean.opBoolean","SPLIT",EDGE,{"disambiguationData":[TD([makeQuery(id+"F3.opExtrude","SWEPT_FACE",FACE,{"disambiguationData":[OSD([subQ0])]})])],"derivedFrom":makeQuery(id+"F1.opExtrude","CAP_EDGE",EDGE,{"disambiguationData":[OSD([subQ2])],"isStart":true})});}
            var Q4;
            Q4=makeQuery(id+"F3.opExtrude","CAP_EDGE",EDGE,{"disambiguationData":[OSD([sQuery(id+"F2.wireOp",EDGE,"E18.57.0.2")])],"isStart":true});
            var Q5;
            Q5=makeQuery(id+"F3.opExtrude","CAP_EDGE",EDGE,{"disambiguationData":[OSD([sQuery(id+"F2.wireOp",EDGE,"E18.55.0.2")])],"isStart":true});
            var Q6;
            Q6=makeQuery(id+"F3.opExtrude","CAP_EDGE",EDGE,{"disambiguationData":[OSD([sQuery(id+"F2.wireOp",EDGE,"E18.53.0.2")])],"isStart":true});
            var Q7;
            Q7=makeQuery(id+"F3.opExtrude","CAP_EDGE",EDGE,{"disambiguationData":[OSD([sQuery(id+"F2.wireOp",EDGE,"E18.51.0.2")])],"isStart":true});
            var Q8;
            Q8=makeQuery(id+"F3.opExtrude","CAP_EDGE",EDGE,{"disambiguationData":[OSD([sQuery(id+"F2.wireOp",EDGE,"E18.49.0.2")])],"isStart":true});
            var Q9;
            Q9=makeQuery(id+"F3.opExtrude","CAP_EDGE",EDGE,{"disambiguationData":[OSD([sQuery(id+"F2.wireOp",EDGE,"E18.47.0.2")])],"isStart":true});
            var Q10;
            Q10=makeQuery(id+"F3.opExtrude","CAP_EDGE",EDGE,{"disambiguationData":[OSD([sQuery(id+"F2.wireOp",EDGE,"E18.45.0.2")])],"isStart":true});
            var Q11;
            Q11=makeQuery(id+"F3.opExtrude","CAP_EDGE",EDGE,{"disambiguationData":[OSD([sQuery(id+"F2.wireOp",EDGE,"E18.43.0.2")])],"isStart":true});
            var Q12;
            Q12=makeQuery(id+"F3.opExtrude","CAP_EDGE",EDGE,{"disambiguationData":[OSD([sQuery(id+"F2.wireOp",EDGE,"E18.41.0.2")])],"isStart":true});
            var Q13;
            Q13=makeQuery(id+"F3.opExtrude","CAP_EDGE",EDGE,{"disambiguationData":[OSD([sQuery(id+"F2.wireOp",EDGE,"E18.39.0.2")])],"isStart":true});
            var Q14;
            Q14=makeQuery(id+"F3.opExtrude","CAP_EDGE",EDGE,{"disambiguationData":[OSD([sQuery(id+"F2.wireOp",EDGE,"E18.37.0.2")])],"isStart":true});
            var Q15;
            Q15=makeQuery(id+"F3.opExtrude","CAP_EDGE",EDGE,{"disambiguationData":[OSD([sQuery(id+"F2.wireOp",EDGE,"E18.35.0.2")])],"isStart":true});
            var Q16;
            Q16=makeQuery(id+"F3.opExtrude","CAP_EDGE",EDGE,{"disambiguationData":[OSD([sQuery(id+"F2.wireOp",EDGE,"E18.33.0.2")])],"isStart":true});
            var Q17;
            Q17=makeQuery(id+"F3.opExtrude","CAP_EDGE",EDGE,{"disambiguationData":[OSD([sQuery(id+"F2.wireOp",EDGE,"E18.31.0.2")])],"isStart":true});
            var Q18;
            Q18=makeQuery(id+"F3.opExtrude","CAP_EDGE",EDGE,{"disambiguationData":[OSD([sQuery(id+"F2.wireOp",EDGE,"E18.29.0.2")])],"isStart":true});
            var Q19;
            Q19=makeQuery(id+"F3.opExtrude","CAP_EDGE",EDGE,{"disambiguationData":[OSD([sQuery(id+"F2.wireOp",EDGE,"E18.27.0.2")])],"isStart":true});
            var Q20;
            Q20=makeQuery(id+"F3.opExtrude","CAP_EDGE",EDGE,{"disambiguationData":[OSD([sQuery(id+"F2.wireOp",EDGE,"E18.25.0.2")])],"isStart":true});
            var Q21;
            Q21=makeQuery(id+"F3.opExtrude","CAP_EDGE",EDGE,{"disambiguationData":[OSD([sQuery(id+"F2.wireOp",EDGE,"E18.23.0.2")])],"isStart":true});
            var Q22;
            Q22=makeQuery(id+"F3.opExtrude","CAP_EDGE",EDGE,{"disambiguationData":[OSD([sQuery(id+"F2.wireOp",EDGE,"E18.21.0.2")])],"isStart":true});
            var Q23;
            Q23=makeQuery(id+"F3.opExtrude","CAP_EDGE",EDGE,{"disambiguationData":[OSD([sQuery(id+"F2.wireOp",EDGE,"E18.17.0.2")])],"isStart":true});
            var Q24;
            Q24=makeQuery(id+"F3.opExtrude","CAP_EDGE",EDGE,{"disambiguationData":[OSD([sQuery(id+"F2.wireOp",EDGE,"E18.19.0.2")])],"isStart":true});
            var Q25;
            Q25=makeQuery(id+"F3.opExtrude","CAP_EDGE",EDGE,{"disambiguationData":[OSD([sQuery(id+"F2.wireOp",EDGE,"E18.13.0.2")])],"isStart":true});
            var Q26;
            Q26=makeQuery(id+"F3.opExtrude","CAP_EDGE",EDGE,{"disambiguationData":[OSD([sQuery(id+"F2.wireOp",EDGE,"E18.15.0.2")])],"isStart":true});
            var Q27;
            Q27=makeQuery(id+"F3.opExtrude","CAP_EDGE",EDGE,{"disambiguationData":[OSD([sQuery(id+"F2.wireOp",EDGE,"E18.11.0.2")])],"isStart":true});
            var Q28;
            Q28=makeQuery(id+"F3.opExtrude","CAP_EDGE",EDGE,{"disambiguationData":[OSD([sQuery(id+"F2.wireOp",EDGE,"E18.9.0.2")])],"isStart":true});
            var Q29;
            Q29=makeQuery(id+"F3.opExtrude","CAP_EDGE",EDGE,{"disambiguationData":[OSD([sQuery(id+"F2.wireOp",EDGE,"E18.5.0.2")])],"isStart":true});
            var Q30;
            Q30=makeQuery(id+"F3.opExtrude","CAP_EDGE",EDGE,{"disambiguationData":[OSD([sQuery(id+"F2.wireOp",EDGE,"E18.7.0.2")])],"isStart":true});
            var Q31;
            Q31=makeQuery(id+"F3.opExtrude","CAP_EDGE",EDGE,{"disambiguationData":[OSD([sQuery(id+"F2.wireOp",EDGE,"E18.3.0.2")])],"isStart":true});
            var Q32;
            Q32=makeQuery(id+"F3.opExtrude","CAP_EDGE",EDGE,{"disambiguationData":[OSD([sQuery(id+"F2.wireOp",EDGE,"E18.1.0.2")])],"isStart":true});
            var Q33;
            Q33=makeQuery(id+"F3.opExtrude","CAP_EDGE",EDGE,{"disambiguationData":[OSD([sQuery(id+"F2.wireOp",EDGE,"E18.57.0.1")])],"isStart":true});
            var Q34;
            Q34=makeQuery(id+"F3.opExtrude","CAP_EDGE",EDGE,{"disambiguationData":[OSD([sQuery(id+"F2.wireOp",EDGE,"E18.55.0.1")])],"isStart":true});
            var Q35;
            Q35=makeQuery(id+"F3.opExtrude","CAP_EDGE",EDGE,{"disambiguationData":[OSD([sQuery(id+"F2.wireOp",EDGE,"E18.53.0.1")])],"isStart":true});
            var Q36;
            Q36=makeQuery(id+"F3.opExtrude","CAP_EDGE",EDGE,{"disambiguationData":[OSD([sQuery(id+"F2.wireOp",EDGE,"E18.51.0.1")])],"isStart":true});
            var Q37;
            Q37=makeQuery(id+"F3.opExtrude","CAP_EDGE",EDGE,{"disambiguationData":[OSD([sQuery(id+"F2.wireOp",EDGE,"E18.49.0.1")])],"isStart":true});
            var Q38;
            Q38=makeQuery(id+"F3.opExtrude","CAP_EDGE",EDGE,{"disambiguationData":[OSD([sQuery(id+"F2.wireOp",EDGE,"E18.47.0.1")])],"isStart":true});
            var Q39;
            Q39=makeQuery(id+"F3.opExtrude","CAP_EDGE",EDGE,{"disambiguationData":[OSD([sQuery(id+"F2.wireOp",EDGE,"E18.45.0.1")])],"isStart":true});
            var Q40;
            Q40=makeQuery(id+"F3.opExtrude","CAP_EDGE",EDGE,{"disambiguationData":[OSD([sQuery(id+"F2.wireOp",EDGE,"E18.43.0.1")])],"isStart":true});
            var Q41;
            Q41=makeQuery(id+"F3.opExtrude","CAP_EDGE",EDGE,{"disambiguationData":[OSD([sQuery(id+"F2.wireOp",EDGE,"E18.41.0.1")])],"isStart":true});
            var Q42;
            Q42=makeQuery(id+"F3.opExtrude","CAP_EDGE",EDGE,{"disambiguationData":[OSD([sQuery(id+"F2.wireOp",EDGE,"E18.37.0.1")])],"isStart":true});
            var Q43;
            Q43=makeQuery(id+"F3.opExtrude","CAP_EDGE",EDGE,{"disambiguationData":[OSD([sQuery(id+"F2.wireOp",EDGE,"E18.39.0.1")])],"isStart":true});
            var Q44;
            Q44=makeQuery(id+"F3.opExtrude","CAP_EDGE",EDGE,{"disambiguationData":[OSD([sQuery(id+"F2.wireOp",EDGE,"E18.35.0.1")])],"isStart":true});
            var Q45;
            Q45=makeQuery(id+"F3.opExtrude","CAP_EDGE",EDGE,{"disambiguationData":[OSD([sQuery(id+"F2.wireOp",EDGE,"E18.33.0.1")])],"isStart":true});
            var Q46;
            Q46=makeQuery(id+"F3.opExtrude","CAP_EDGE",EDGE,{"disambiguationData":[OSD([sQuery(id+"F2.wireOp",EDGE,"E18.31.0.1")])],"isStart":true});
            var Q47;
            Q47=makeQuery(id+"F3.opExtrude","CAP_EDGE",EDGE,{"disambiguationData":[OSD([sQuery(id+"F2.wireOp",EDGE,"E18.29.0.1")])],"isStart":true});
            var Q48;
            Q48=makeQuery(id+"F3.opExtrude","CAP_EDGE",EDGE,{"disambiguationData":[OSD([sQuery(id+"F2.wireOp",EDGE,"E18.27.0.1")])],"isStart":true});
            var Q49;
            Q49=makeQuery(id+"F3.opExtrude","CAP_EDGE",EDGE,{"disambiguationData":[OSD([sQuery(id+"F2.wireOp",EDGE,"E18.25.0.1")])],"isStart":true});
            var Q50;
            Q50=makeQuery(id+"F3.opExtrude","CAP_EDGE",EDGE,{"disambiguationData":[OSD([sQuery(id+"F2.wireOp",EDGE,"E18.23.0.1")])],"isStart":true});
            var Q51;
            Q51=makeQuery(id+"F3.opExtrude","CAP_EDGE",EDGE,{"disambiguationData":[OSD([sQuery(id+"F2.wireOp",EDGE,"E18.21.0.1")])],"isStart":true});
            var Q52;
            Q52=makeQuery(id+"F3.opExtrude","CAP_EDGE",EDGE,{"disambiguationData":[OSD([sQuery(id+"F2.wireOp",EDGE,"E18.19.0.1")])],"isStart":true});
            var Q53;
            Q53=makeQuery(id+"F3.opExtrude","CAP_EDGE",EDGE,{"disambiguationData":[OSD([sQuery(id+"F2.wireOp",EDGE,"E18.17.0.1")])],"isStart":true});
            var Q54;
            Q54=makeQuery(id+"F3.opExtrude","CAP_EDGE",EDGE,{"disambiguationData":[OSD([sQuery(id+"F2.wireOp",EDGE,"E18.15.0.1")])],"isStart":true});
            var Q55;
            Q55=makeQuery(id+"F3.opExtrude","CAP_EDGE",EDGE,{"disambiguationData":[OSD([sQuery(id+"F2.wireOp",EDGE,"E18.13.0.1")])],"isStart":true});
            var Q56;
            Q56=makeQuery(id+"F3.opExtrude","CAP_EDGE",EDGE,{"disambiguationData":[OSD([sQuery(id+"F2.wireOp",EDGE,"E18.11.0.1")])],"isStart":true});
            var Q57;
            Q57=makeQuery(id+"F3.opExtrude","CAP_EDGE",EDGE,{"disambiguationData":[OSD([sQuery(id+"F2.wireOp",EDGE,"E18.9.0.1")])],"isStart":true});
            var Q58;
            Q58=makeQuery(id+"F3.opExtrude","CAP_EDGE",EDGE,{"disambiguationData":[OSD([sQuery(id+"F2.wireOp",EDGE,"E18.7.0.1")])],"isStart":true});
            var Q59;
            Q59=makeQuery(id+"F3.opExtrude","CAP_EDGE",EDGE,{"disambiguationData":[OSD([sQuery(id+"F2.wireOp",EDGE,"E18.5.0.1")])],"isStart":true});
            var Q60;
            Q60=makeQuery(id+"F3.opExtrude","CAP_EDGE",EDGE,{"disambiguationData":[OSD([sQuery(id+"F2.wireOp",EDGE,"E18.3.0.1")])],"isStart":true});
            var Q61;
            Q61=makeQuery(id+"F3.opExtrude","CAP_EDGE",EDGE,{"disambiguationData":[OSD([sQuery(id+"F2.wireOp",EDGE,"E18.1.0.1")])],"isStart":true});
            var Q62;
            Q62=makeQuery(id+"F3.opExtrude","CAP_EDGE",EDGE,{"disambiguationData":[OSD([sQuery(id+"F2.wireOp",EDGE,"E18.55.0.0")])],"isStart":true});
            var Q63;
            Q63=makeQuery(id+"F3.opExtrude","CAP_EDGE",EDGE,{"disambiguationData":[OSD([sQuery(id+"F2.wireOp",EDGE,"E18.57.0.0")])],"isStart":true});
            var Q64;
            Q64=makeQuery(id+"F3.opExtrude","CAP_EDGE",EDGE,{"disambiguationData":[OSD([sQuery(id+"F2.wireOp",EDGE,"E18.53.0.0")])],"isStart":true});
            var Q65;
            Q65=makeQuery(id+"F3.opExtrude","CAP_EDGE",EDGE,{"disambiguationData":[OSD([sQuery(id+"F2.wireOp",EDGE,"E18.51.0.0")])],"isStart":true});
            var Q66;
            Q66=makeQuery(id+"F3.opExtrude","CAP_EDGE",EDGE,{"disambiguationData":[OSD([sQuery(id+"F2.wireOp",EDGE,"E18.49.0.0")])],"isStart":true});
            var Q67;
            Q67=makeQuery(id+"F3.opExtrude","CAP_EDGE",EDGE,{"disambiguationData":[OSD([sQuery(id+"F2.wireOp",EDGE,"E18.47.0.0")])],"isStart":true});
            var Q68;
            Q68=makeQuery(id+"F3.opExtrude","CAP_EDGE",EDGE,{"disambiguationData":[OSD([sQuery(id+"F2.wireOp",EDGE,"E18.43.0.0")])],"isStart":true});
            var Q69;
            Q69=makeQuery(id+"F3.opExtrude","CAP_EDGE",EDGE,{"disambiguationData":[OSD([sQuery(id+"F2.wireOp",EDGE,"E18.45.0.0")])],"isStart":true});
            var Q70;
            Q70=makeQuery(id+"F3.opExtrude","CAP_EDGE",EDGE,{"disambiguationData":[OSD([sQuery(id+"F2.wireOp",EDGE,"E18.41.0.0")])],"isStart":true});
            var Q71;
            Q71=makeQuery(id+"F3.opExtrude","CAP_EDGE",EDGE,{"disambiguationData":[OSD([sQuery(id+"F2.wireOp",EDGE,"E18.39.0.0")])],"isStart":true});
            var Q72;
            Q72=makeQuery(id+"F3.opExtrude","CAP_EDGE",EDGE,{"disambiguationData":[OSD([sQuery(id+"F2.wireOp",EDGE,"E18.37.0.0")])],"isStart":true});
            var Q73;
            Q73=makeQuery(id+"F3.opExtrude","CAP_EDGE",EDGE,{"disambiguationData":[OSD([sQuery(id+"F2.wireOp",EDGE,"E18.35.0.0")])],"isStart":true});
            var Q74;
            Q74=makeQuery(id+"F3.opExtrude","CAP_EDGE",EDGE,{"disambiguationData":[OSD([sQuery(id+"F2.wireOp",EDGE,"E18.33.0.0")])],"isStart":true});
            var Q75;
            Q75=makeQuery(id+"F3.opExtrude","CAP_EDGE",EDGE,{"disambiguationData":[OSD([sQuery(id+"F2.wireOp",EDGE,"E18.31.0.0")])],"isStart":true});
            var Q76;
            Q76=makeQuery(id+"F3.opExtrude","CAP_EDGE",EDGE,{"disambiguationData":[OSD([sQuery(id+"F2.wireOp",EDGE,"E18.27.0.0")])],"isStart":true});
            var Q77;
            Q77=makeQuery(id+"F3.opExtrude","CAP_EDGE",EDGE,{"disambiguationData":[OSD([sQuery(id+"F2.wireOp",EDGE,"E18.29.0.0")])],"isStart":true});
            var Q78;
            Q78=makeQuery(id+"F3.opExtrude","CAP_EDGE",EDGE,{"disambiguationData":[OSD([sQuery(id+"F2.wireOp",EDGE,"E18.25.0.0")])],"isStart":true});
            var Q79;
            Q79=makeQuery(id+"F3.opExtrude","CAP_EDGE",EDGE,{"disambiguationData":[OSD([sQuery(id+"F2.wireOp",EDGE,"E18.23.0.0")])],"isStart":true});
            var Q80;
            Q80=makeQuery(id+"F3.opExtrude","CAP_EDGE",EDGE,{"disambiguationData":[OSD([sQuery(id+"F2.wireOp",EDGE,"E18.21.0.0")])],"isStart":true});
            var Q81;
            Q81=makeQuery(id+"F3.opExtrude","CAP_EDGE",EDGE,{"disambiguationData":[OSD([sQuery(id+"F2.wireOp",EDGE,"E18.17.0.0")])],"isStart":true});
            var Q82;
            Q82=makeQuery(id+"F3.opExtrude","CAP_EDGE",EDGE,{"disambiguationData":[OSD([sQuery(id+"F2.wireOp",EDGE,"E18.19.0.0")])],"isStart":true});
            var Q83;
            Q83=makeQuery(id+"F3.opExtrude","CAP_EDGE",EDGE,{"disambiguationData":[OSD([sQuery(id+"F2.wireOp",EDGE,"E18.15.0.0")])],"isStart":true});
            var Q84;
            Q84=makeQuery(id+"F3.opExtrude","CAP_EDGE",EDGE,{"disambiguationData":[OSD([sQuery(id+"F2.wireOp",EDGE,"E18.13.0.0")])],"isStart":true});
            var Q85;
            Q85=makeQuery(id+"F3.opExtrude","CAP_EDGE",EDGE,{"disambiguationData":[OSD([sQuery(id+"F2.wireOp",EDGE,"E18.11.0.0")])],"isStart":true});
            var Q86;
            Q86=makeQuery(id+"F3.opExtrude","CAP_EDGE",EDGE,{"disambiguationData":[OSD([sQuery(id+"F2.wireOp",EDGE,"E18.9.0.0")])],"isStart":true});
            var Q87;
            Q87=makeQuery(id+"F3.opExtrude","CAP_EDGE",EDGE,{"disambiguationData":[OSD([sQuery(id+"F2.wireOp",EDGE,"E18.7.0.0")])],"isStart":true});
            var Q88;
            Q88=makeQuery(id+"F3.opExtrude","CAP_EDGE",EDGE,{"disambiguationData":[OSD([sQuery(id+"F2.wireOp",EDGE,"E18.5.0.0")])],"isStart":true});
            var Q89;
            Q89=makeQuery(id+"F3.opExtrude","CAP_EDGE",EDGE,{"disambiguationData":[OSD([sQuery(id+"F2.wireOp",EDGE,"E18.3.0.0")])],"isStart":true});
            var Q90;
            Q90=makeQuery(id+"F3.opExtrude","CAP_EDGE",EDGE,{"disambiguationData":[OSD([sQuery(id+"F2.wireOp",EDGE,"E18.1.0.0")])],"isStart":true});
            var Q91;
            Q91=makeQuery(id+"F3.opExtrude","CAP_EDGE",EDGE,{"disambiguationData":[OSD([sQuery(id+"F2.wireOp",EDGE,"E17")])],"isStart":true});
            var Q92;
            Q92=makeQuery(id+"F3.opExtrude","CAP_EDGE",EDGE,{"disambiguationData":[OSD([sQuery(id+"F2.wireOp",EDGE,"E18.58.0.2")])],"isStart":true});
            var Q93;
            Q93=makeQuery(id+"F3.opExtrude","CAP_EDGE",EDGE,{"disambiguationData":[OSD([sQuery(id+"F2.wireOp",EDGE,"E18.56.0.2")])],"isStart":true});
            var Q94;
            Q94=makeQuery(id+"F3.opExtrude","CAP_EDGE",EDGE,{"disambiguationData":[OSD([sQuery(id+"F2.wireOp",EDGE,"E18.54.0.2")])],"isStart":true});
            var Q95;
            Q95=makeQuery(id+"F3.opExtrude","CAP_EDGE",EDGE,{"disambiguationData":[OSD([sQuery(id+"F2.wireOp",EDGE,"E18.52.0.2")])],"isStart":true});
            var Q96;
            Q96=makeQuery(id+"F3.opExtrude","CAP_EDGE",EDGE,{"disambiguationData":[OSD([sQuery(id+"F2.wireOp",EDGE,"E18.50.0.2")])],"isStart":true});
            var Q97;
            Q97=makeQuery(id+"F3.opExtrude","CAP_EDGE",EDGE,{"disambiguationData":[OSD([sQuery(id+"F2.wireOp",EDGE,"E18.48.0.2")])],"isStart":true});
            var Q98;
            Q98=makeQuery(id+"F3.opExtrude","CAP_EDGE",EDGE,{"disambiguationData":[OSD([sQuery(id+"F2.wireOp",EDGE,"E18.46.0.2")])],"isStart":true});
            var Q99;
            Q99=makeQuery(id+"F3.opExtrude","CAP_EDGE",EDGE,{"disambiguationData":[OSD([sQuery(id+"F2.wireOp",EDGE,"E18.44.0.2")])],"isStart":true});
            var Q100;
            Q100=makeQuery(id+"F3.opExtrude","CAP_EDGE",EDGE,{"disambiguationData":[OSD([sQuery(id+"F2.wireOp",EDGE,"E18.42.0.2")])],"isStart":true});
            var Q101;
            Q101=makeQuery(id+"F3.opExtrude","CAP_EDGE",EDGE,{"disambiguationData":[OSD([sQuery(id+"F2.wireOp",EDGE,"E18.40.0.2")])],"isStart":true});
            var Q102;
            Q102=makeQuery(id+"F3.opExtrude","CAP_EDGE",EDGE,{"disambiguationData":[OSD([sQuery(id+"F2.wireOp",EDGE,"E18.38.0.2")])],"isStart":true});
            var Q103;
            Q103=makeQuery(id+"F3.opExtrude","CAP_EDGE",EDGE,{"disambiguationData":[OSD([sQuery(id+"F2.wireOp",EDGE,"E18.36.0.2")])],"isStart":true});
            var Q104;
            Q104=makeQuery(id+"F3.opExtrude","CAP_EDGE",EDGE,{"disambiguationData":[OSD([sQuery(id+"F2.wireOp",EDGE,"E18.34.0.2")])],"isStart":true});
            var Q105;
            Q105=makeQuery(id+"F3.opExtrude","CAP_EDGE",EDGE,{"disambiguationData":[OSD([sQuery(id+"F2.wireOp",EDGE,"E18.32.0.2")])],"isStart":true});
            var Q106;
            Q106=makeQuery(id+"F3.opExtrude","CAP_EDGE",EDGE,{"disambiguationData":[OSD([sQuery(id+"F2.wireOp",EDGE,"E18.30.0.2")])],"isStart":true});
            var Q107;
            Q107=makeQuery(id+"F3.opExtrude","CAP_EDGE",EDGE,{"disambiguationData":[OSD([sQuery(id+"F2.wireOp",EDGE,"E18.28.0.2")])],"isStart":true});
            var Q108;
            Q108=makeQuery(id+"F3.opExtrude","CAP_EDGE",EDGE,{"disambiguationData":[OSD([sQuery(id+"F2.wireOp",EDGE,"E18.26.0.2")])],"isStart":true});
            var Q109;
            Q109=makeQuery(id+"F3.opExtrude","CAP_EDGE",EDGE,{"disambiguationData":[OSD([sQuery(id+"F2.wireOp",EDGE,"E18.24.0.2")])],"isStart":true});
            var Q110;
            Q110=makeQuery(id+"F3.opExtrude","CAP_EDGE",EDGE,{"disambiguationData":[OSD([sQuery(id+"F2.wireOp",EDGE,"E18.22.0.2")])],"isStart":true});
            var Q111;
            Q111=makeQuery(id+"F3.opExtrude","CAP_EDGE",EDGE,{"disambiguationData":[OSD([sQuery(id+"F2.wireOp",EDGE,"E18.20.0.2")])],"isStart":true});
            var Q112;
            Q112=makeQuery(id+"F3.opExtrude","CAP_EDGE",EDGE,{"disambiguationData":[OSD([sQuery(id+"F2.wireOp",EDGE,"E18.18.0.2")])],"isStart":true});
            var Q113;
            Q113=makeQuery(id+"F3.opExtrude","CAP_EDGE",EDGE,{"disambiguationData":[OSD([sQuery(id+"F2.wireOp",EDGE,"E18.16.0.2")])],"isStart":true});
            var Q114;
            Q114=makeQuery(id+"F3.opExtrude","CAP_EDGE",EDGE,{"disambiguationData":[OSD([sQuery(id+"F2.wireOp",EDGE,"E18.14.0.2")])],"isStart":true});
            var Q115;
            Q115=makeQuery(id+"F3.opExtrude","CAP_EDGE",EDGE,{"disambiguationData":[OSD([sQuery(id+"F2.wireOp",EDGE,"E18.10.0.2")])],"isStart":true});
            var Q116;
            Q116=makeQuery(id+"F3.opExtrude","CAP_EDGE",EDGE,{"disambiguationData":[OSD([sQuery(id+"F2.wireOp",EDGE,"E18.12.0.2")])],"isStart":true});
            var Q117;
            Q117=makeQuery(id+"F3.opExtrude","CAP_EDGE",EDGE,{"disambiguationData":[OSD([sQuery(id+"F2.wireOp",EDGE,"E18.6.0.2")])],"isStart":true});
            var Q118;
            Q118=makeQuery(id+"F3.opExtrude","CAP_EDGE",EDGE,{"disambiguationData":[OSD([sQuery(id+"F2.wireOp",EDGE,"E18.8.0.2")])],"isStart":true});
            var Q119;
            Q119=makeQuery(id+"F3.opExtrude","CAP_EDGE",EDGE,{"disambiguationData":[OSD([sQuery(id+"F2.wireOp",EDGE,"E18.4.0.2")])],"isStart":true});
            var Q120;
            Q120=makeQuery(id+"F3.opExtrude","CAP_EDGE",EDGE,{"disambiguationData":[OSD([sQuery(id+"F2.wireOp",EDGE,"E18.2.0.2")])],"isStart":true});
            var Q121;
            Q121=makeQuery(id+"F3.opExtrude","CAP_EDGE",EDGE,{"disambiguationData":[OSD([sQuery(id+"F2.wireOp",EDGE,"E16.right")])],"isStart":true});
            var Q122;
            Q122=makeQuery(id+"F3.opExtrude","CAP_EDGE",EDGE,{"disambiguationData":[OSD([sQuery(id+"F2.wireOp",EDGE,"E18.56.0.1")])],"isStart":true});
            var Q123;
            Q123=makeQuery(id+"F3.opExtrude","CAP_EDGE",EDGE,{"disambiguationData":[OSD([sQuery(id+"F2.wireOp",EDGE,"E18.58.0.1")])],"isStart":true});
            var Q124;
            Q124=makeQuery(id+"F3.opExtrude","CAP_EDGE",EDGE,{"disambiguationData":[OSD([sQuery(id+"F2.wireOp",EDGE,"E18.54.0.1")])],"isStart":true});
            var Q125;
            Q125=makeQuery(id+"F3.opExtrude","CAP_EDGE",EDGE,{"disambiguationData":[OSD([sQuery(id+"F2.wireOp",EDGE,"E18.52.0.1")])],"isStart":true});
            var Q126;
            Q126=makeQuery(id+"F3.opExtrude","CAP_EDGE",EDGE,{"disambiguationData":[OSD([sQuery(id+"F2.wireOp",EDGE,"E18.48.0.1")])],"isStart":true});
            var Q127;
            Q127=makeQuery(id+"F3.opExtrude","CAP_EDGE",EDGE,{"disambiguationData":[OSD([sQuery(id+"F2.wireOp",EDGE,"E18.50.0.1")])],"isStart":true});
            var Q128;
            Q128=makeQuery(id+"F3.opExtrude","CAP_EDGE",EDGE,{"disambiguationData":[OSD([sQuery(id+"F2.wireOp",EDGE,"E18.46.0.1")])],"isStart":true});
            var Q129;
            Q129=makeQuery(id+"F3.opExtrude","CAP_EDGE",EDGE,{"disambiguationData":[OSD([sQuery(id+"F2.wireOp",EDGE,"E18.44.0.1")])],"isStart":true});
            var Q130;
            Q130=makeQuery(id+"F3.opExtrude","CAP_EDGE",EDGE,{"disambiguationData":[OSD([sQuery(id+"F2.wireOp",EDGE,"E18.42.0.1")])],"isStart":true});
            var Q131;
            Q131=makeQuery(id+"F3.opExtrude","CAP_EDGE",EDGE,{"disambiguationData":[OSD([sQuery(id+"F2.wireOp",EDGE,"E18.40.0.1")])],"isStart":true});
            var Q132;
            Q132=makeQuery(id+"F3.opExtrude","CAP_EDGE",EDGE,{"disambiguationData":[OSD([sQuery(id+"F2.wireOp",EDGE,"E18.38.0.1")])],"isStart":true});
            var Q133;
            Q133=makeQuery(id+"F3.opExtrude","CAP_EDGE",EDGE,{"disambiguationData":[OSD([sQuery(id+"F2.wireOp",EDGE,"E18.36.0.1")])],"isStart":true});
            var Q134;
            Q134=makeQuery(id+"F3.opExtrude","CAP_EDGE",EDGE,{"disambiguationData":[OSD([sQuery(id+"F2.wireOp",EDGE,"E18.34.0.1")])],"isStart":true});
            var Q135;
            Q135=makeQuery(id+"F3.opExtrude","CAP_EDGE",EDGE,{"disambiguationData":[OSD([sQuery(id+"F2.wireOp",EDGE,"E18.32.0.1")])],"isStart":true});
            var Q136;
            Q136=makeQuery(id+"F3.opExtrude","CAP_EDGE",EDGE,{"disambiguationData":[OSD([sQuery(id+"F2.wireOp",EDGE,"E18.30.0.1")])],"isStart":true});
            var Q137;
            Q137=makeQuery(id+"F3.opExtrude","CAP_EDGE",EDGE,{"disambiguationData":[OSD([sQuery(id+"F2.wireOp",EDGE,"E18.28.0.1")])],"isStart":true});
            var Q138;
            Q138=makeQuery(id+"F3.opExtrude","CAP_EDGE",EDGE,{"disambiguationData":[OSD([sQuery(id+"F2.wireOp",EDGE,"E18.26.0.1")])],"isStart":true});
            var Q139;
            Q139=makeQuery(id+"F3.opExtrude","CAP_EDGE",EDGE,{"disambiguationData":[OSD([sQuery(id+"F2.wireOp",EDGE,"E18.24.0.1")])],"isStart":true});
            var Q140;
            Q140=makeQuery(id+"F3.opExtrude","CAP_EDGE",EDGE,{"disambiguationData":[OSD([sQuery(id+"F2.wireOp",EDGE,"E18.22.0.1")])],"isStart":true});
            var Q141;
            Q141=makeQuery(id+"F3.opExtrude","CAP_EDGE",EDGE,{"disambiguationData":[OSD([sQuery(id+"F2.wireOp",EDGE,"E18.20.0.1")])],"isStart":true});
            var Q142;
            Q142=makeQuery(id+"F3.opExtrude","CAP_EDGE",EDGE,{"disambiguationData":[OSD([sQuery(id+"F2.wireOp",EDGE,"E18.18.0.1")])],"isStart":true});
            var Q143;
            Q143=makeQuery(id+"F3.opExtrude","CAP_EDGE",EDGE,{"disambiguationData":[OSD([sQuery(id+"F2.wireOp",EDGE,"E18.16.0.1")])],"isStart":true});
            var Q144;
            Q144=makeQuery(id+"F3.opExtrude","CAP_EDGE",EDGE,{"disambiguationData":[OSD([sQuery(id+"F2.wireOp",EDGE,"E18.14.0.1")])],"isStart":true});
            var Q145;
            Q145=makeQuery(id+"F3.opExtrude","CAP_EDGE",EDGE,{"disambiguationData":[OSD([sQuery(id+"F2.wireOp",EDGE,"E18.12.0.1")])],"isStart":true});
            var Q146;
            Q146=makeQuery(id+"F3.opExtrude","CAP_EDGE",EDGE,{"disambiguationData":[OSD([sQuery(id+"F2.wireOp",EDGE,"E18.10.0.1")])],"isStart":true});
            var Q147;
            Q147=makeQuery(id+"F3.opExtrude","CAP_EDGE",EDGE,{"disambiguationData":[OSD([sQuery(id+"F2.wireOp",EDGE,"E18.8.0.1")])],"isStart":true});
            var Q148;
            Q148=makeQuery(id+"F3.opExtrude","CAP_EDGE",EDGE,{"disambiguationData":[OSD([sQuery(id+"F2.wireOp",EDGE,"E18.6.0.1")])],"isStart":true});
            var Q149;
            Q149=makeQuery(id+"F3.opExtrude","CAP_EDGE",EDGE,{"disambiguationData":[OSD([sQuery(id+"F2.wireOp",EDGE,"E18.4.0.1")])],"isStart":true});
            var Q150;
            Q150=makeQuery(id+"F3.opExtrude","CAP_EDGE",EDGE,{"disambiguationData":[OSD([sQuery(id+"F2.wireOp",EDGE,"E18.2.0.1")])],"isStart":true});
            var Q151;
            Q151=makeQuery(id+"F3.opExtrude","CAP_EDGE",EDGE,{"disambiguationData":[OSD([sQuery(id+"F2.wireOp",EDGE,"E16.left")])],"isStart":true});
            var Q152;
            Q152=makeQuery(id+"F3.opExtrude","SWEPT_EDGE",EDGE,{"disambiguationData":[OSD([sQuery(id+"F2.wireOp",EDGE,"E18.6.0.0"),sQuery(id+"F2.wireOp",EDGE,"E18.6.0.3")])]});
            var Q153;
            Q153=makeQuery(id+"F3.opExtrude","SWEPT_EDGE",EDGE,{"disambiguationData":[OSD([sQuery(id+"F2.wireOp",EDGE,"E18.5.0.0"),sQuery(id+"F2.wireOp",EDGE,"E18.5.0.3")])]});
            var Q154;
            Q154=makeQuery(id+"F3.opExtrude","SWEPT_EDGE",EDGE,{"disambiguationData":[OSD([sQuery(id+"F2.wireOp",EDGE,"E18.3.0.1"),sQuery(id+"F2.wireOp",EDGE,"E18.3.0.3")])]});
            var Q155;
            Q155=makeQuery(id+"F3.opExtrude","SWEPT_EDGE",EDGE,{"disambiguationData":[OSD([sQuery(id+"F2.wireOp",EDGE,"E18.2.0.1"),sQuery(id+"F2.wireOp",EDGE,"E18.2.0.3")])]});
            var Q156;
            Q156=makeQuery(id+"F3.opExtrude","SWEPT_EDGE",EDGE,{"disambiguationData":[OSD([sQuery(id+"F2.wireOp",EDGE,"E18.2.0.0"),sQuery(id+"F2.wireOp",EDGE,"E18.2.0.3")])]});
            var Q157;
            Q157=makeQuery(id+"F3.opExtrude","SWEPT_EDGE",EDGE,{"disambiguationData":[OSD([sQuery(id+"F2.wireOp",EDGE,"E16.bottom"),sQuery(id+"F2.wireOp",EDGE,"E16.right")])]});
            var Q158;
            Q158=makeQuery(id+"F3.opExtrude","SWEPT_EDGE",EDGE,{"disambiguationData":[OSD([sQuery(id+"F2.wireOp",EDGE,"E18.6.0.1"),sQuery(id+"F2.wireOp",EDGE,"E18.6.0.3")])]});
            var Q159;
            {var subQ0=sQuery(id+"F2.wireOp",EDGE,"E18.11.0.1");var subQ1=sQuery(id+"F0.wireOp",EDGE,"E0.top");Q159=makeQuery(id+"F3.boolean.opBoolean","SPLIT",EDGE,{"disambiguationData":[TD([makeQuery(id+"F3.opExtrude","SWEPT_FACE",FACE,{"disambiguationData":[OSD([subQ0])]})])],"derivedFrom":makeQuery(id+"F1.opExtrude","CAP_EDGE",EDGE,{"disambiguationData":[OSD([subQ1])],"isStart":true})});}
            var Q160;
            {var subQ0=sQuery(id+"F2.wireOp",EDGE,"E18.33.0.1");var subQ1=sQuery(id+"F0.wireOp",EDGE,"E0.top");Q160=makeQuery(id+"F3.boolean.opBoolean","SPLIT",EDGE,{"disambiguationData":[TD([makeQuery(id+"F3.opExtrude","SWEPT_FACE",FACE,{"disambiguationData":[OSD([subQ0])]})])],"derivedFrom":makeQuery(id+"F1.opExtrude","CAP_EDGE",EDGE,{"disambiguationData":[OSD([subQ1])],"isStart":true})});}
            var Q161;
            {var subQ0=sQuery(id+"F2.wireOp",EDGE,"E18.43.0.1");var subQ1=sQuery(id+"F0.wireOp",EDGE,"E0.top");Q161=makeQuery(id+"F3.boolean.opBoolean","SPLIT",EDGE,{"disambiguationData":[TD([makeQuery(id+"F3.opExtrude","SWEPT_FACE",FACE,{"disambiguationData":[OSD([subQ0])]})])],"derivedFrom":makeQuery(id+"F1.opExtrude","CAP_EDGE",EDGE,{"disambiguationData":[OSD([subQ1])],"isStart":true})});}
            var Q162;
            Q162=makeQuery(id+"F3.opExtrude","CAP_EDGE",EDGE,{"disambiguationData":[OSD([sQuery(id+"F2.wireOp",EDGE,"E18.36.0.0")])],"isStart":true});
            var Q163;
            {var subQ0=sQuery(id+"F0.wireOp",EDGE,"E0.top");var subQ1=sQuery(id+"F2.wireOp",EDGE,"E18.16.0.1");Q163=makeQuery(id+"F3.boolean.opBoolean","SPLIT",EDGE,{"disambiguationData":[TD([makeQuery(id+"F3.opExtrude","SWEPT_FACE",FACE,{"disambiguationData":[OSD([subQ1])]})])],"derivedFrom":makeQuery(id+"F1.opExtrude","CAP_EDGE",EDGE,{"disambiguationData":[OSD([subQ0])],"isStart":true})});}
            var Q164;
            {var subQ0=sQuery(id+"F2.wireOp",EDGE,"E18.41.0.1");var subQ2=sQuery(id+"F0.wireOp",EDGE,"E0.top");Q164=makeQuery(id+"F3.boolean.opBoolean","SPLIT",EDGE,{"disambiguationData":[TD([makeQuery(id+"F3.opExtrude","SWEPT_FACE",FACE,{"disambiguationData":[OSD([subQ0])]})])],"derivedFrom":makeQuery(id+"F1.opExtrude","CAP_EDGE",EDGE,{"disambiguationData":[OSD([subQ2])],"isStart":true})});}
            var Q165;
            {var subQ1=sQuery(id+"F0.wireOp",EDGE,"E0.top");var subQ2=sQuery(id+"F2.wireOp",EDGE,"E18.57.0.1");Q165=makeQuery(id+"F3.boolean.opBoolean","SPLIT",EDGE,{"disambiguationData":[TD([makeQuery(id+"F3.opExtrude","SWEPT_FACE",FACE,{"disambiguationData":[OSD([subQ2])]})])],"derivedFrom":makeQuery(id+"F1.opExtrude","CAP_EDGE",EDGE,{"disambiguationData":[OSD([subQ1])],"isStart":true})});}
            var Q166;
            Q166=makeQuery(id+"F3.opExtrude","CAP_EDGE",EDGE,{"disambiguationData":[OSD([sQuery(id+"F2.wireOp",EDGE,"E18.8.0.0")])],"isStart":true});
            var Q167;
            {var subQ0=sQuery(id+"F2.wireOp",EDGE,"E18.28.0.1");var subQ2=sQuery(id+"F0.wireOp",EDGE,"E0.top");Q167=makeQuery(id+"F3.boolean.opBoolean","SPLIT",EDGE,{"disambiguationData":[TD([makeQuery(id+"F3.opExtrude","SWEPT_FACE",FACE,{"disambiguationData":[OSD([subQ0])]})])],"derivedFrom":makeQuery(id+"F1.opExtrude","CAP_EDGE",EDGE,{"disambiguationData":[OSD([subQ2])],"isStart":true})});}
            var Q168;
            Q168=makeQuery(id+"F3.opExtrude","CAP_EDGE",EDGE,{"disambiguationData":[OSD([sQuery(id+"F2.wireOp",EDGE,"E18.14.0.0")])],"isStart":true});
            var Q169;
            {var subQ0=sQuery(id+"F2.wireOp",EDGE,"E18.7.0.1");var subQ1=sQuery(id+"F0.wireOp",EDGE,"E0.top");Q169=makeQuery(id+"F3.boolean.opBoolean","SPLIT",EDGE,{"disambiguationData":[TD([makeQuery(id+"F3.opExtrude","SWEPT_FACE",FACE,{"disambiguationData":[OSD([subQ0])]})])],"derivedFrom":makeQuery(id+"F1.opExtrude","CAP_EDGE",EDGE,{"disambiguationData":[OSD([subQ1])],"isStart":true})});}
            var Q170;
            Q170=makeQuery(id+"F3.opExtrude","CAP_EDGE",EDGE,{"disambiguationData":[OSD([sQuery(id+"F2.wireOp",EDGE,"E18.38.0.0")])],"isStart":true});
            var Q171;
            Q171=makeQuery(id+"F3.opExtrude","CAP_EDGE",EDGE,{"disambiguationData":[OSD([sQuery(id+"F2.wireOp",EDGE,"E18.22.0.0")])],"isStart":true});
            var Q172;
            {var subQ1=sQuery(id+"F2.wireOp",EDGE,"E18.29.0.1");var subQ2=sQuery(id+"F0.wireOp",EDGE,"E0.top");Q172=makeQuery(id+"F3.boolean.opBoolean","SPLIT",EDGE,{"disambiguationData":[TD([makeQuery(id+"F3.opExtrude","SWEPT_FACE",FACE,{"disambiguationData":[OSD([subQ1])]})])],"derivedFrom":makeQuery(id+"F1.opExtrude","CAP_EDGE",EDGE,{"disambiguationData":[OSD([subQ2])],"isStart":true})});}
            var Q173;
            Q173=makeQuery(id+"F3.opExtrude","CAP_EDGE",EDGE,{"disambiguationData":[OSD([sQuery(id+"F2.wireOp",EDGE,"E18.4.0.0")])],"isStart":true});
            var Q174;
            {var subQ0=sQuery(id+"F2.wireOp",EDGE,"E18.39.0.1");var subQ2=sQuery(id+"F0.wireOp",EDGE,"E0.top");Q174=makeQuery(id+"F3.boolean.opBoolean","SPLIT",EDGE,{"disambiguationData":[TD([makeQuery(id+"F3.opExtrude","SWEPT_FACE",FACE,{"disambiguationData":[OSD([subQ0])]})])],"derivedFrom":makeQuery(id+"F1.opExtrude","CAP_EDGE",EDGE,{"disambiguationData":[OSD([subQ2])],"isStart":true})});}
            var Q175;
            {var subQ0=sQuery(id+"F0.wireOp",EDGE,"E0.top");var subQ2=sQuery(id+"F2.wireOp",EDGE,"E18.8.0.1");Q175=makeQuery(id+"F3.boolean.opBoolean","SPLIT",EDGE,{"disambiguationData":[TD([makeQuery(id+"F3.opExtrude","SWEPT_FACE",FACE,{"disambiguationData":[OSD([subQ2])]})])],"derivedFrom":makeQuery(id+"F1.opExtrude","CAP_EDGE",EDGE,{"disambiguationData":[OSD([subQ0])],"isStart":true})});}
            var Q176;
            {var subQ0=sQuery(id+"F2.wireOp",EDGE,"E18.24.0.1");var subQ1=sQuery(id+"F0.wireOp",EDGE,"E0.top");Q176=makeQuery(id+"F3.boolean.opBoolean","SPLIT",EDGE,{"disambiguationData":[TD([makeQuery(id+"F3.opExtrude","SWEPT_FACE",FACE,{"disambiguationData":[OSD([subQ0])]})])],"derivedFrom":makeQuery(id+"F1.opExtrude","CAP_EDGE",EDGE,{"disambiguationData":[OSD([subQ1])],"isStart":true})});}
            var Q177;
            {var subQ0=sQuery(id+"F2.wireOp",EDGE,"E18.35.0.1");var subQ1=sQuery(id+"F0.wireOp",EDGE,"E0.top");Q177=makeQuery(id+"F3.boolean.opBoolean","SPLIT",EDGE,{"disambiguationData":[TD([makeQuery(id+"F3.opExtrude","SWEPT_FACE",FACE,{"disambiguationData":[OSD([subQ0])]})])],"derivedFrom":makeQuery(id+"F1.opExtrude","CAP_EDGE",EDGE,{"disambiguationData":[OSD([subQ1])],"isStart":true})});}
            var Q178;
            {var subQ0=sQuery(id+"F2.wireOp",EDGE,"E16.right");var subQ1=sQuery(id+"F0.wireOp",EDGE,"E0.top");Q178=makeQuery(id+"F3.boolean.opBoolean","SPLIT",EDGE,{"disambiguationData":[TD([makeQuery(id+"F3.opExtrude","SWEPT_FACE",FACE,{"disambiguationData":[OSD([subQ0])]})])],"derivedFrom":makeQuery(id+"F1.opExtrude","CAP_EDGE",EDGE,{"disambiguationData":[OSD([subQ1])],"isStart":true})});}
            var Q179;
            Q179=makeQuery(id+"F3.opExtrude","CAP_EDGE",EDGE,{"disambiguationData":[OSD([sQuery(id+"F2.wireOp",EDGE,"E18.18.0.0")])],"isStart":true});
            var Q180;
            {var subQ1=sQuery(id+"F2.wireOp",EDGE,"E18.26.0.1");var subQ2=sQuery(id+"F0.wireOp",EDGE,"E0.top");Q180=makeQuery(id+"F3.boolean.opBoolean","SPLIT",EDGE,{"disambiguationData":[TD([makeQuery(id+"F3.opExtrude","SWEPT_FACE",FACE,{"disambiguationData":[OSD([subQ1])]})])],"derivedFrom":makeQuery(id+"F1.opExtrude","CAP_EDGE",EDGE,{"disambiguationData":[OSD([subQ2])],"isStart":true})});}
            var Q181;
            Q181=makeQuery(id+"F3.opExtrude","CAP_EDGE",EDGE,{"disambiguationData":[OSD([sQuery(id+"F2.wireOp",EDGE,"E18.2.0.0")])],"isStart":true});
            var Q182;
            {var subQ1=sQuery(id+"F2.wireOp",EDGE,"E18.54.0.1");var subQ2=sQuery(id+"F0.wireOp",EDGE,"E0.top");Q182=makeQuery(id+"F3.boolean.opBoolean","SPLIT",EDGE,{"disambiguationData":[TD([makeQuery(id+"F3.opExtrude","SWEPT_FACE",FACE,{"disambiguationData":[OSD([subQ1])]})])],"derivedFrom":makeQuery(id+"F1.opExtrude","CAP_EDGE",EDGE,{"disambiguationData":[OSD([subQ2])],"isStart":true})});}
            var Q183;
            {var subQ1=sQuery(id+"F0.wireOp",EDGE,"E0.top");var subQ2=sQuery(id+"F2.wireOp",EDGE,"E18.3.0.1");Q183=makeQuery(id+"F3.boolean.opBoolean","SPLIT",EDGE,{"disambiguationData":[TD([makeQuery(id+"F3.opExtrude","SWEPT_FACE",FACE,{"disambiguationData":[OSD([subQ2])]})])],"derivedFrom":makeQuery(id+"F1.opExtrude","CAP_EDGE",EDGE,{"disambiguationData":[OSD([subQ1])],"isStart":true})});}
            var Q184;
            {var subQ0=sQuery(id+"F0.wireOp",EDGE,"E0.top");var subQ2=sQuery(id+"F2.wireOp",EDGE,"E18.48.0.1");Q184=makeQuery(id+"F3.boolean.opBoolean","SPLIT",EDGE,{"disambiguationData":[TD([makeQuery(id+"F3.opExtrude","SWEPT_FACE",FACE,{"disambiguationData":[OSD([subQ2])]})])],"derivedFrom":makeQuery(id+"F1.opExtrude","CAP_EDGE",EDGE,{"disambiguationData":[OSD([subQ0])],"isStart":true})});}
            var Q185;
            {var subQ0=sQuery(id+"F2.wireOp",EDGE,"E18.42.0.1");var subQ1=sQuery(id+"F0.wireOp",EDGE,"E0.top");Q185=makeQuery(id+"F3.boolean.opBoolean","SPLIT",EDGE,{"disambiguationData":[TD([makeQuery(id+"F3.opExtrude","SWEPT_FACE",FACE,{"disambiguationData":[OSD([subQ0])]})])],"derivedFrom":makeQuery(id+"F1.opExtrude","CAP_EDGE",EDGE,{"disambiguationData":[OSD([subQ1])],"isStart":true})});}
            var Q186;
            {var subQ1=sQuery(id+"F2.wireOp",EDGE,"E18.27.0.1");var subQ2=sQuery(id+"F0.wireOp",EDGE,"E0.top");Q186=makeQuery(id+"F3.boolean.opBoolean","SPLIT",EDGE,{"disambiguationData":[TD([makeQuery(id+"F3.opExtrude","SWEPT_FACE",FACE,{"disambiguationData":[OSD([subQ1])]})])],"derivedFrom":makeQuery(id+"F1.opExtrude","CAP_EDGE",EDGE,{"disambiguationData":[OSD([subQ2])],"isStart":true})});}
            var Q187;
            Q187=makeQuery(id+"F3.opExtrude","CAP_EDGE",EDGE,{"disambiguationData":[OSD([sQuery(id+"F2.wireOp",EDGE,"E18.48.0.0")])],"isStart":true});
            var Q188;
            Q188=makeQuery(id+"F3.opExtrude","CAP_EDGE",EDGE,{"disambiguationData":[OSD([sQuery(id+"F2.wireOp",EDGE,"E18.30.0.0")])],"isStart":true});
            var Q189;
            Q189=makeQuery(id+"F3.opExtrude","CAP_EDGE",EDGE,{"disambiguationData":[OSD([sQuery(id+"F2.wireOp",EDGE,"E18.32.0.0")])],"isStart":true});
            var Q190;
            {var subQ1=sQuery(id+"F2.wireOp",EDGE,"E18.17.0.1");var subQ2=sQuery(id+"F0.wireOp",EDGE,"E0.top");Q190=makeQuery(id+"F3.boolean.opBoolean","SPLIT",EDGE,{"disambiguationData":[TD([makeQuery(id+"F3.opExtrude","SWEPT_FACE",FACE,{"disambiguationData":[OSD([subQ1])]})])],"derivedFrom":makeQuery(id+"F1.opExtrude","CAP_EDGE",EDGE,{"disambiguationData":[OSD([subQ2])],"isStart":true})});}
            var Q191;
            {var subQ1=sQuery(id+"F2.wireOp",EDGE,"E18.32.0.1");var subQ2=sQuery(id+"F0.wireOp",EDGE,"E0.top");Q191=makeQuery(id+"F3.boolean.opBoolean","SPLIT",EDGE,{"disambiguationData":[TD([makeQuery(id+"F3.opExtrude","SWEPT_FACE",FACE,{"disambiguationData":[OSD([subQ1])]})])],"derivedFrom":makeQuery(id+"F1.opExtrude","CAP_EDGE",EDGE,{"disambiguationData":[OSD([subQ2])],"isStart":true})});}
            var Q192;
            Q192=makeQuery(id+"F3.opExtrude","CAP_EDGE",EDGE,{"disambiguationData":[OSD([sQuery(id+"F2.wireOp",EDGE,"E18.28.0.0")])],"isStart":true});
            var Q193;
            {var subQ0=sQuery(id+"F0.wireOp",EDGE,"E0.top");var subQ2=sQuery(id+"F2.wireOp",EDGE,"E18.53.0.1");Q193=makeQuery(id+"F3.boolean.opBoolean","SPLIT",EDGE,{"disambiguationData":[TD([makeQuery(id+"F3.opExtrude","SWEPT_FACE",FACE,{"disambiguationData":[OSD([subQ2])]})])],"derivedFrom":makeQuery(id+"F1.opExtrude","CAP_EDGE",EDGE,{"disambiguationData":[OSD([subQ0])],"isStart":true})});}
            var Q194;
            Q194=makeQuery(id+"F3.opExtrude","CAP_EDGE",EDGE,{"disambiguationData":[OSD([sQuery(id+"F2.wireOp",EDGE,"E18.20.0.0")])],"isStart":true});
            var Q195;
            Q195=makeQuery(id+"F3.opExtrude","CAP_EDGE",EDGE,{"disambiguationData":[OSD([sQuery(id+"F2.wireOp",EDGE,"E18.24.0.0")])],"isStart":true});
            var Q196;
            Q196=makeQuery(id+"F3.opExtrude","CAP_EDGE",EDGE,{"disambiguationData":[OSD([sQuery(id+"F2.wireOp",EDGE,"E18.40.0.0")])],"isStart":true});
            var Q197;
            {var subQ1=sQuery(id+"F2.wireOp",EDGE,"E18.23.0.1");var subQ2=sQuery(id+"F0.wireOp",EDGE,"E0.top");Q197=makeQuery(id+"F3.boolean.opBoolean","SPLIT",EDGE,{"disambiguationData":[TD([makeQuery(id+"F3.opExtrude","SWEPT_FACE",FACE,{"disambiguationData":[OSD([subQ1])]})])],"derivedFrom":makeQuery(id+"F1.opExtrude","CAP_EDGE",EDGE,{"disambiguationData":[OSD([subQ2])],"isStart":true})});}
            var Q198;
            {var subQ0=sQuery(id+"F2.wireOp",EDGE,"E18.19.0.1");var subQ1=sQuery(id+"F0.wireOp",EDGE,"E0.top");Q198=makeQuery(id+"F3.boolean.opBoolean","SPLIT",EDGE,{"disambiguationData":[TD([makeQuery(id+"F3.opExtrude","SWEPT_FACE",FACE,{"disambiguationData":[OSD([subQ0])]})])],"derivedFrom":makeQuery(id+"F1.opExtrude","CAP_EDGE",EDGE,{"disambiguationData":[OSD([subQ1])],"isStart":true})});}
            var Q199;
            {var subQ1=sQuery(id+"F0.wireOp",EDGE,"E0.top");var subQ2=sQuery(id+"F2.wireOp",EDGE,"E18.18.0.1");Q199=makeQuery(id+"F3.boolean.opBoolean","SPLIT",EDGE,{"disambiguationData":[TD([makeQuery(id+"F3.opExtrude","SWEPT_FACE",FACE,{"disambiguationData":[OSD([subQ2])]})])],"derivedFrom":makeQuery(id+"F1.opExtrude","CAP_EDGE",EDGE,{"disambiguationData":[OSD([subQ1])],"isStart":true})});}
            var Q200;
            {var subQ1=sQuery(id+"F2.wireOp",EDGE,"E18.34.0.1");var subQ2=sQuery(id+"F0.wireOp",EDGE,"E0.top");Q200=makeQuery(id+"F3.boolean.opBoolean","SPLIT",EDGE,{"disambiguationData":[TD([makeQuery(id+"F3.opExtrude","SWEPT_FACE",FACE,{"disambiguationData":[OSD([subQ1])]})])],"derivedFrom":makeQuery(id+"F1.opExtrude","CAP_EDGE",EDGE,{"disambiguationData":[OSD([subQ2])],"isStart":true})});}
            var Q201;
            Q201=makeQuery(id+"F3.opExtrude","CAP_EDGE",EDGE,{"disambiguationData":[OSD([sQuery(id+"F2.wireOp",EDGE,"E18.34.0.0")])],"isStart":true});
            var Q202;
            {var subQ0=sQuery(id+"F0.wireOp",EDGE,"E0.top");var subQ1=sQuery(id+"F2.wireOp",EDGE,"E18.13.0.1");Q202=makeQuery(id+"F3.boolean.opBoolean","SPLIT",EDGE,{"disambiguationData":[TD([makeQuery(id+"F3.opExtrude","SWEPT_FACE",FACE,{"disambiguationData":[OSD([subQ1])]})])],"derivedFrom":makeQuery(id+"F1.opExtrude","CAP_EDGE",EDGE,{"disambiguationData":[OSD([subQ0])],"isStart":true})});}
            var Q203;
            Q203=makeQuery(id+"F3.opExtrude","CAP_EDGE",EDGE,{"disambiguationData":[OSD([sQuery(id+"F2.wireOp",EDGE,"E18.16.0.0")])],"isStart":true});
            var Q204;
            {var subQ1=sQuery(id+"F2.wireOp",EDGE,"E18.31.0.1");var subQ2=sQuery(id+"F0.wireOp",EDGE,"E0.top");Q204=makeQuery(id+"F3.boolean.opBoolean","SPLIT",EDGE,{"disambiguationData":[TD([makeQuery(id+"F3.opExtrude","SWEPT_FACE",FACE,{"disambiguationData":[OSD([subQ1])]})])],"derivedFrom":makeQuery(id+"F1.opExtrude","CAP_EDGE",EDGE,{"disambiguationData":[OSD([subQ2])],"isStart":true})});}
            var Q205;
            {var subQ0=sQuery(id+"F0.wireOp",EDGE,"E0.top");var subQ1=sQuery(id+"F2.wireOp",EDGE,"E18.12.0.1");Q205=makeQuery(id+"F3.boolean.opBoolean","SPLIT",EDGE,{"disambiguationData":[TD([makeQuery(id+"F3.opExtrude","SWEPT_FACE",FACE,{"disambiguationData":[OSD([subQ1])]})])],"derivedFrom":makeQuery(id+"F1.opExtrude","CAP_EDGE",EDGE,{"disambiguationData":[OSD([subQ0])],"isStart":true})});}
            var Q206;
            {var subQ1=sQuery(id+"F2.wireOp",EDGE,"E18.21.0.1");var subQ2=sQuery(id+"F0.wireOp",EDGE,"E0.top");Q206=makeQuery(id+"F3.boolean.opBoolean","SPLIT",EDGE,{"disambiguationData":[TD([makeQuery(id+"F3.opExtrude","SWEPT_FACE",FACE,{"disambiguationData":[OSD([subQ1])]})])],"derivedFrom":makeQuery(id+"F1.opExtrude","CAP_EDGE",EDGE,{"disambiguationData":[OSD([subQ2])],"isStart":true})});}
            var Q207;
            {var subQ1=sQuery(id+"F0.wireOp",EDGE,"E0.top");var subQ2=sQuery(id+"F2.wireOp",EDGE,"E18.25.0.1");Q207=makeQuery(id+"F3.boolean.opBoolean","SPLIT",EDGE,{"disambiguationData":[TD([makeQuery(id+"F3.opExtrude","SWEPT_FACE",FACE,{"disambiguationData":[OSD([subQ2])]})])],"derivedFrom":makeQuery(id+"F1.opExtrude","CAP_EDGE",EDGE,{"disambiguationData":[OSD([subQ1])],"isStart":true})});}
            var Q208;
            {var subQ1=sQuery(id+"F2.wireOp",EDGE,"E18.22.0.1");var subQ2=sQuery(id+"F0.wireOp",EDGE,"E0.top");Q208=makeQuery(id+"F3.boolean.opBoolean","SPLIT",EDGE,{"disambiguationData":[TD([makeQuery(id+"F3.opExtrude","SWEPT_FACE",FACE,{"disambiguationData":[OSD([subQ1])]})])],"derivedFrom":makeQuery(id+"F1.opExtrude","CAP_EDGE",EDGE,{"disambiguationData":[OSD([subQ2])],"isStart":true})});}
            var Q209;
            Q209=makeQuery(id+"F3.opExtrude","CAP_EDGE",EDGE,{"disambiguationData":[OSD([sQuery(id+"F2.wireOp",EDGE,"E18.54.0.0")])],"isStart":true});
            var Q210;
            {var subQ0=sQuery(id+"F2.wireOp",EDGE,"E18.45.0.1");var subQ1=sQuery(id+"F0.wireOp",EDGE,"E0.top");Q210=makeQuery(id+"F3.boolean.opBoolean","SPLIT",EDGE,{"disambiguationData":[TD([makeQuery(id+"F3.opExtrude","SWEPT_FACE",FACE,{"disambiguationData":[OSD([subQ0])]})])],"derivedFrom":makeQuery(id+"F1.opExtrude","CAP_EDGE",EDGE,{"disambiguationData":[OSD([subQ1])],"isStart":true})});}
            var Q211;
            Q211=makeQuery(id+"F3.opExtrude","CAP_EDGE",EDGE,{"disambiguationData":[OSD([sQuery(id+"F2.wireOp",EDGE,"E18.50.0.0")])],"isStart":true});
            var Q212;
            {var subQ0=sQuery(id+"F2.wireOp",EDGE,"E18.47.0.1");var subQ1=sQuery(id+"F0.wireOp",EDGE,"E0.top");Q212=makeQuery(id+"F3.boolean.opBoolean","SPLIT",EDGE,{"disambiguationData":[TD([makeQuery(id+"F3.opExtrude","SWEPT_FACE",FACE,{"disambiguationData":[OSD([subQ0])]})])],"derivedFrom":makeQuery(id+"F1.opExtrude","CAP_EDGE",EDGE,{"disambiguationData":[OSD([subQ1])],"isStart":true})});}
            var Q213;
            Q213=makeQuery(id+"F3.opExtrude","CAP_EDGE",EDGE,{"disambiguationData":[OSD([sQuery(id+"F2.wireOp",EDGE,"E18.42.0.0")])],"isStart":true});
            var Q214;
            {var subQ0=sQuery(id+"F2.wireOp",EDGE,"E18.38.0.1");var subQ1=sQuery(id+"F0.wireOp",EDGE,"E0.top");Q214=makeQuery(id+"F3.boolean.opBoolean","SPLIT",EDGE,{"disambiguationData":[TD([makeQuery(id+"F3.opExtrude","SWEPT_FACE",FACE,{"disambiguationData":[OSD([subQ0])]})])],"derivedFrom":makeQuery(id+"F1.opExtrude","CAP_EDGE",EDGE,{"disambiguationData":[OSD([subQ1])],"isStart":true})});}
            var Q215;
            {var subQ0=sQuery(id+"F2.wireOp",EDGE,"E18.10.0.1");var subQ1=sQuery(id+"F0.wireOp",EDGE,"E0.top");Q215=makeQuery(id+"F3.boolean.opBoolean","SPLIT",EDGE,{"disambiguationData":[TD([makeQuery(id+"F3.opExtrude","SWEPT_FACE",FACE,{"disambiguationData":[OSD([subQ0])]})])],"derivedFrom":makeQuery(id+"F1.opExtrude","CAP_EDGE",EDGE,{"disambiguationData":[OSD([subQ1])],"isStart":true})});}
            var Q216;
            {var subQ1=sQuery(id+"F2.wireOp",EDGE,"E18.37.0.1");var subQ2=sQuery(id+"F0.wireOp",EDGE,"E0.top");Q216=makeQuery(id+"F3.boolean.opBoolean","SPLIT",EDGE,{"disambiguationData":[TD([makeQuery(id+"F3.opExtrude","SWEPT_FACE",FACE,{"disambiguationData":[OSD([subQ1])]})])],"derivedFrom":makeQuery(id+"F1.opExtrude","CAP_EDGE",EDGE,{"disambiguationData":[OSD([subQ2])],"isStart":true})});}
            var Q217;
            {var subQ0=sQuery(id+"F0.wireOp",EDGE,"E0.top");var subQ2=sQuery(id+"F2.wireOp",EDGE,"E18.56.0.1");Q217=makeQuery(id+"F3.boolean.opBoolean","SPLIT",EDGE,{"disambiguationData":[TD([makeQuery(id+"F3.opExtrude","SWEPT_FACE",FACE,{"disambiguationData":[OSD([subQ2])]})])],"derivedFrom":makeQuery(id+"F1.opExtrude","CAP_EDGE",EDGE,{"disambiguationData":[OSD([subQ0])],"isStart":true})});}
            var Q218;
            Q218=makeQuery(id+"F3.opExtrude","CAP_EDGE",EDGE,{"disambiguationData":[OSD([sQuery(id+"F2.wireOp",EDGE,"E18.6.0.0")])],"isStart":true});
            var Q219;
            {var subQ0=sQuery(id+"F0.wireOp",EDGE,"E0.top");var subQ2=sQuery(id+"F2.wireOp",EDGE,"E18.52.0.1");Q219=makeQuery(id+"F3.boolean.opBoolean","SPLIT",EDGE,{"disambiguationData":[TD([makeQuery(id+"F3.opExtrude","SWEPT_FACE",FACE,{"disambiguationData":[OSD([subQ2])]})])],"derivedFrom":makeQuery(id+"F1.opExtrude","CAP_EDGE",EDGE,{"disambiguationData":[OSD([subQ0])],"isStart":true})});}
            var Q220;
            Q220=makeQuery(id+"F3.opExtrude","CAP_EDGE",EDGE,{"disambiguationData":[OSD([sQuery(id+"F2.wireOp",EDGE,"E18.44.0.0")])],"isStart":true});
            var Q221;
            Q221=makeQuery(id+"F3.opExtrude","CAP_EDGE",EDGE,{"disambiguationData":[OSD([sQuery(id+"F2.wireOp",EDGE,"E18.46.0.0")])],"isStart":true});
            var Q222;
            Q222=makeQuery(id+"F3.opExtrude","CAP_EDGE",EDGE,{"disambiguationData":[OSD([sQuery(id+"F2.wireOp",EDGE,"E18.12.0.0")])],"isStart":true});
            var Q223;
            {var subQ0=sQuery(id+"F2.wireOp",EDGE,"E18.4.0.1");var subQ1=sQuery(id+"F0.wireOp",EDGE,"E0.top");Q223=makeQuery(id+"F3.boolean.opBoolean","SPLIT",EDGE,{"disambiguationData":[TD([makeQuery(id+"F3.opExtrude","SWEPT_FACE",FACE,{"disambiguationData":[OSD([subQ0])]})])],"derivedFrom":makeQuery(id+"F1.opExtrude","CAP_EDGE",EDGE,{"disambiguationData":[OSD([subQ1])],"isStart":true})});}
            var Q224;
            Q224=makeQuery(id+"F3.opExtrude","CAP_EDGE",EDGE,{"disambiguationData":[OSD([sQuery(id+"F2.wireOp",EDGE,"E18.58.0.0")])],"isStart":true});
            var Q225;
            Q225=makeQuery(id+"F3.opExtrude","CAP_EDGE",EDGE,{"disambiguationData":[OSD([sQuery(id+"F2.wireOp",EDGE,"E18.56.0.0")])],"isStart":true});
            var Q226;
            {var subQ0=sQuery(id+"F0.wireOp",EDGE,"E0.top");var subQ2=sQuery(id+"F2.wireOp",EDGE,"E18.14.0.1");Q226=makeQuery(id+"F3.boolean.opBoolean","SPLIT",EDGE,{"disambiguationData":[TD([makeQuery(id+"F3.opExtrude","SWEPT_FACE",FACE,{"disambiguationData":[OSD([subQ2])]})])],"derivedFrom":makeQuery(id+"F1.opExtrude","CAP_EDGE",EDGE,{"disambiguationData":[OSD([subQ0])],"isStart":true})});}
            var Q227;
            {var subQ0=sQuery(id+"F2.wireOp",EDGE,"E18.6.0.1");var subQ1=sQuery(id+"F0.wireOp",EDGE,"E0.top");Q227=makeQuery(id+"F3.boolean.opBoolean","SPLIT",EDGE,{"disambiguationData":[TD([makeQuery(id+"F3.opExtrude","SWEPT_FACE",FACE,{"disambiguationData":[OSD([subQ0])]})])],"derivedFrom":makeQuery(id+"F1.opExtrude","CAP_EDGE",EDGE,{"disambiguationData":[OSD([subQ1])],"isStart":true})});}
            var Q228;
            {var subQ0=sQuery(id+"F2.wireOp",EDGE,"E18.50.0.1");var subQ1=sQuery(id+"F0.wireOp",EDGE,"E0.top");Q228=makeQuery(id+"F3.boolean.opBoolean","SPLIT",EDGE,{"disambiguationData":[TD([makeQuery(id+"F3.opExtrude","SWEPT_FACE",FACE,{"disambiguationData":[OSD([subQ0])]})])],"derivedFrom":makeQuery(id+"F1.opExtrude","CAP_EDGE",EDGE,{"disambiguationData":[OSD([subQ1])],"isStart":true})});}
            var Q229;
            Q229=makeQuery(id+"F3.opExtrude","CAP_EDGE",EDGE,{"disambiguationData":[OSD([sQuery(id+"F2.wireOp",EDGE,"E18.10.0.0")])],"isStart":true});
            var Q230;
            {var subQ0=sQuery(id+"F0.wireOp",EDGE,"E0.top");var subQ2=sQuery(id+"F2.wireOp",EDGE,"E18.1.0.1");Q230=makeQuery(id+"F3.boolean.opBoolean","SPLIT",EDGE,{"disambiguationData":[TD([makeQuery(id+"F3.opExtrude","SWEPT_FACE",FACE,{"disambiguationData":[OSD([subQ2])]})])],"derivedFrom":makeQuery(id+"F1.opExtrude","CAP_EDGE",EDGE,{"disambiguationData":[OSD([subQ0])],"isStart":true})});}
            var Q231;
            {var subQ0=sQuery(id+"F2.wireOp",EDGE,"E18.51.0.1");var subQ1=sQuery(id+"F0.wireOp",EDGE,"E0.top");Q231=makeQuery(id+"F3.boolean.opBoolean","SPLIT",EDGE,{"disambiguationData":[TD([makeQuery(id+"F3.opExtrude","SWEPT_FACE",FACE,{"disambiguationData":[OSD([subQ0])]})])],"derivedFrom":makeQuery(id+"F1.opExtrude","CAP_EDGE",EDGE,{"disambiguationData":[OSD([subQ1])],"isStart":true})});}
            var Q232;
            {var subQ1=sQuery(id+"F2.wireOp",EDGE,"E18.46.0.1");var subQ2=sQuery(id+"F0.wireOp",EDGE,"E0.top");Q232=makeQuery(id+"F3.boolean.opBoolean","SPLIT",EDGE,{"disambiguationData":[TD([makeQuery(id+"F3.opExtrude","SWEPT_FACE",FACE,{"disambiguationData":[OSD([subQ1])]})])],"derivedFrom":makeQuery(id+"F1.opExtrude","CAP_EDGE",EDGE,{"disambiguationData":[OSD([subQ2])],"isStart":true})});}
            var Q233;
            {var subQ1=sQuery(id+"F2.wireOp",EDGE,"E18.20.0.1");var subQ2=sQuery(id+"F0.wireOp",EDGE,"E0.top");Q233=makeQuery(id+"F3.boolean.opBoolean","SPLIT",EDGE,{"disambiguationData":[TD([makeQuery(id+"F3.opExtrude","SWEPT_FACE",FACE,{"disambiguationData":[OSD([subQ1])]})])],"derivedFrom":makeQuery(id+"F1.opExtrude","CAP_EDGE",EDGE,{"disambiguationData":[OSD([subQ2])],"isStart":true})});}
            var Q234;
            Q234=makeQuery(id+"F3.opExtrude","CAP_EDGE",EDGE,{"disambiguationData":[OSD([sQuery(id+"F2.wireOp",EDGE,"E18.26.0.0")])],"isStart":true});
            var Q235;
            Q235=makeQuery(id+"F3.opExtrude","CAP_EDGE",EDGE,{"disambiguationData":[OSD([sQuery(id+"F2.wireOp",EDGE,"E18.52.0.0")])],"isStart":true});
            var Q236;
            {var subQ1=sQuery(id+"F2.wireOp",EDGE,"E18.49.0.1");var subQ2=sQuery(id+"F0.wireOp",EDGE,"E0.top");Q236=makeQuery(id+"F3.boolean.opBoolean","SPLIT",EDGE,{"disambiguationData":[TD([makeQuery(id+"F3.opExtrude","SWEPT_FACE",FACE,{"disambiguationData":[OSD([subQ1])]})])],"derivedFrom":makeQuery(id+"F1.opExtrude","CAP_EDGE",EDGE,{"disambiguationData":[OSD([subQ2])],"isStart":true})});}
            var Q237;
            {var subQ0=sQuery(id+"F2.wireOp",EDGE,"E18.9.0.1");var subQ2=sQuery(id+"F0.wireOp",EDGE,"E0.top");Q237=makeQuery(id+"F3.boolean.opBoolean","SPLIT",EDGE,{"disambiguationData":[TD([makeQuery(id+"F3.opExtrude","SWEPT_FACE",FACE,{"disambiguationData":[OSD([subQ0])]})])],"derivedFrom":makeQuery(id+"F1.opExtrude","CAP_EDGE",EDGE,{"disambiguationData":[OSD([subQ2])],"isStart":true})});}
            var Q238;
            {var subQ0=sQuery(id+"F2.wireOp",EDGE,"E18.55.0.1");var subQ1=sQuery(id+"F0.wireOp",EDGE,"E0.top");Q238=makeQuery(id+"F3.boolean.opBoolean","SPLIT",EDGE,{"disambiguationData":[TD([makeQuery(id+"F3.opExtrude","SWEPT_FACE",FACE,{"disambiguationData":[OSD([subQ0])]})])],"derivedFrom":makeQuery(id+"F1.opExtrude","CAP_EDGE",EDGE,{"disambiguationData":[OSD([subQ1])],"isStart":true})});}
            var Q239;
            {var subQ0=sQuery(id+"F2.wireOp",EDGE,"E18.36.0.1");var subQ2=sQuery(id+"F0.wireOp",EDGE,"E0.top");Q239=makeQuery(id+"F3.boolean.opBoolean","SPLIT",EDGE,{"disambiguationData":[TD([makeQuery(id+"F3.opExtrude","SWEPT_FACE",FACE,{"disambiguationData":[OSD([subQ0])]})])],"derivedFrom":makeQuery(id+"F1.opExtrude","CAP_EDGE",EDGE,{"disambiguationData":[OSD([subQ2])],"isStart":true})});}
            var Q240;
            {var subQ0=sQuery(id+"F2.wireOp",EDGE,"E18.5.0.1");var subQ1=sQuery(id+"F0.wireOp",EDGE,"E0.top");Q240=makeQuery(id+"F3.boolean.opBoolean","SPLIT",EDGE,{"disambiguationData":[TD([makeQuery(id+"F3.opExtrude","SWEPT_FACE",FACE,{"disambiguationData":[OSD([subQ0])]})])],"derivedFrom":makeQuery(id+"F1.opExtrude","CAP_EDGE",EDGE,{"disambiguationData":[OSD([subQ1])],"isStart":true})});}
            var Q241;
            {var subQ1=sQuery(id+"F0.wireOp",EDGE,"E10.MirrorCS");var subQ2=sQuery(id+"F0.wireOp",EDGE,"E0.top");Q241=makeQuery(id+"F3.boolean.opBoolean","SPLIT",EDGE,{"disambiguationData":[TD([makeQuery(id+"F1.opExtrude","SWEPT_FACE",FACE,{"disambiguationData":[OSD([subQ1])]})])],"derivedFrom":makeQuery(id+"F1.opExtrude","CAP_EDGE",EDGE,{"disambiguationData":[OSD([subQ2])],"isStart":true})});}
            var Q242;
            {var subQ0=sQuery(id+"F0.wireOp",EDGE,"E0.top");var subQ1=sQuery(id+"F2.wireOp",EDGE,"E18.15.0.1");Q242=makeQuery(id+"F3.boolean.opBoolean","SPLIT",EDGE,{"disambiguationData":[TD([makeQuery(id+"F3.opExtrude","SWEPT_FACE",FACE,{"disambiguationData":[OSD([subQ1])]})])],"derivedFrom":makeQuery(id+"F1.opExtrude","CAP_EDGE",EDGE,{"disambiguationData":[OSD([subQ0])],"isStart":true})});}
            var Q243;
            Q243=makeQuery(id+"F3.opExtrude","SWEPT_EDGE",EDGE,{"disambiguationData":[OSD([sQuery(id+"F2.wireOp",EDGE,"E18.56.0.1"),sQuery(id+"F2.wireOp",EDGE,"E18.56.0.3")])]});
            var Q244;
            Q244=makeQuery(id+"F3.opExtrude","SWEPT_EDGE",EDGE,{"disambiguationData":[OSD([sQuery(id+"F2.wireOp",EDGE,"E18.24.0.1"),sQuery(id+"F2.wireOp",EDGE,"E18.24.0.3")])]});
            var Q245;
            Q245=makeQuery(id+"F3.opExtrude","SWEPT_EDGE",EDGE,{"disambiguationData":[OSD([sQuery(id+"F2.wireOp",EDGE,"E18.40.0.1"),sQuery(id+"F2.wireOp",EDGE,"E18.40.0.3")])]});
            var Q246;
            Q246=makeQuery(id+"F3.opExtrude","SWEPT_EDGE",EDGE,{"disambiguationData":[OSD([sQuery(id+"F2.wireOp",EDGE,"E18.16.0.1"),sQuery(id+"F2.wireOp",EDGE,"E18.16.0.3")])]});
            var Q247;
            Q247=makeQuery(id+"F3.opExtrude","SWEPT_EDGE",EDGE,{"disambiguationData":[OSD([sQuery(id+"F2.wireOp",EDGE,"E18.32.0.1"),sQuery(id+"F2.wireOp",EDGE,"E18.32.0.3")])]});
            var Q248;
            Q248=makeQuery(id+"F3.opExtrude","SWEPT_EDGE",EDGE,{"disambiguationData":[OSD([sQuery(id+"F2.wireOp",EDGE,"E18.8.0.1"),sQuery(id+"F2.wireOp",EDGE,"E18.8.0.3")])]});
            var Q249;
            Q249=makeQuery(id+"F3.opExtrude","CAP_EDGE",EDGE,{"disambiguationData":[OSD([sQuery(id+"F2.wireOp",EDGE,"E18.42.0.3")])],"isStart":false});
            var Q250;
            Q250=makeQuery(id+"F3.opExtrude","SWEPT_EDGE",EDGE,{"disambiguationData":[OSD([sQuery(id+"F2.wireOp",EDGE,"E18.40.0.0"),sQuery(id+"F2.wireOp",EDGE,"E18.40.0.3")])]});
            var Q251;
            Q251=makeQuery(id+"F3.opExtrude","SWEPT_EDGE",EDGE,{"disambiguationData":[OSD([sQuery(id+"F2.wireOp",EDGE,"E18.56.0.0"),sQuery(id+"F2.wireOp",EDGE,"E18.56.0.3")])]});
            var Q252;
            Q252=makeQuery(id+"F3.opExtrude","SWEPT_EDGE",EDGE,{"disambiguationData":[OSD([sQuery(id+"F2.wireOp",EDGE,"E18.24.0.0"),sQuery(id+"F2.wireOp",EDGE,"E18.24.0.3")])]});
            var Q253;
            Q253=makeQuery(id+"F3.opExtrude","CAP_EDGE",EDGE,{"disambiguationData":[OSD([sQuery(id+"F2.wireOp",EDGE,"E18.25.0.3")])],"isStart":false});
            var Q254;
            Q254=makeQuery(id+"F3.opExtrude","SWEPT_EDGE",EDGE,{"disambiguationData":[OSD([sQuery(id+"F2.wireOp",EDGE,"E18.31.0.1"),sQuery(id+"F2.wireOp",EDGE,"E18.31.0.3")])]});
            var Q255;
            Q255=makeQuery(id+"F3.opExtrude","SWEPT_EDGE",EDGE,{"disambiguationData":[OSD([sQuery(id+"F2.wireOp",EDGE,"E18.55.0.1"),sQuery(id+"F2.wireOp",EDGE,"E18.55.0.3")])]});
            var Q256;
            Q256=makeQuery(id+"F3.opExtrude","SWEPT_EDGE",EDGE,{"disambiguationData":[OSD([sQuery(id+"F2.wireOp",EDGE,"E18.22.0.0"),sQuery(id+"F2.wireOp",EDGE,"E18.22.0.2")])]});
            var Q257;
            Q257=makeQuery(id+"F3.opExtrude","SWEPT_EDGE",EDGE,{"disambiguationData":[OSD([sQuery(id+"F2.wireOp",EDGE,"E18.9.0.0"),sQuery(id+"F2.wireOp",EDGE,"E18.9.0.3")])]});
            var Q258;
            Q258=makeQuery(id+"F3.opExtrude","SWEPT_EDGE",EDGE,{"disambiguationData":[OSD([sQuery(id+"F2.wireOp",EDGE,"E16.left"),sQuery(id+"F2.wireOp",EDGE,"E17")])]});
            var Q259;
            Q259=makeQuery(id+"F3.opExtrude","SWEPT_EDGE",EDGE,{"disambiguationData":[OSD([sQuery(id+"F2.wireOp",EDGE,"E16.right"),sQuery(id+"F2.wireOp",EDGE,"E17")])]});
            var Q260;
            Q260=makeQuery(id+"F3.opExtrude","SWEPT_EDGE",EDGE,{"disambiguationData":[OSD([sQuery(id+"F2.wireOp",EDGE,"E18.3.0.1"),sQuery(id+"F2.wireOp",EDGE,"E18.3.0.2")])]});
            var Q261;
            Q261=makeQuery(id+"F3.opExtrude","SWEPT_EDGE",EDGE,{"disambiguationData":[OSD([sQuery(id+"F2.wireOp",EDGE,"E18.3.0.0"),sQuery(id+"F2.wireOp",EDGE,"E18.3.0.2")])]});
            var Q262;
            Q262=makeQuery(id+"F3.opExtrude","SWEPT_EDGE",EDGE,{"disambiguationData":[OSD([sQuery(id+"F2.wireOp",EDGE,"E18.38.0.0"),sQuery(id+"F2.wireOp",EDGE,"E18.38.0.2")])]});
            var Q263;
            Q263=makeQuery(id+"F3.opExtrude","SWEPT_EDGE",EDGE,{"disambiguationData":[OSD([sQuery(id+"F2.wireOp",EDGE,"E18.42.0.0"),sQuery(id+"F2.wireOp",EDGE,"E18.42.0.2")])]});
            var Q264;
            Q264=makeQuery(id+"F3.opExtrude","SWEPT_EDGE",EDGE,{"disambiguationData":[OSD([sQuery(id+"F2.wireOp",EDGE,"E18.46.0.0"),sQuery(id+"F2.wireOp",EDGE,"E18.46.0.2")])]});
            var Q265;
            Q265=makeQuery(id+"F3.opExtrude","SWEPT_EDGE",EDGE,{"disambiguationData":[OSD([sQuery(id+"F2.wireOp",EDGE,"E18.30.0.0"),sQuery(id+"F2.wireOp",EDGE,"E18.30.0.2")])]});
            var Q266;
            Q266=makeQuery(id+"F3.opExtrude","SWEPT_EDGE",EDGE,{"disambiguationData":[OSD([sQuery(id+"F2.wireOp",EDGE,"E18.50.0.0"),sQuery(id+"F2.wireOp",EDGE,"E18.50.0.2")])]});
            var Q267;
            Q267=makeQuery(id+"F3.opExtrude","SWEPT_EDGE",EDGE,{"disambiguationData":[OSD([sQuery(id+"F2.wireOp",EDGE,"E18.54.0.0"),sQuery(id+"F2.wireOp",EDGE,"E18.54.0.2")])]});
            var Q268;
            Q268=makeQuery(id+"F3.opExtrude","SWEPT_EDGE",EDGE,{"disambiguationData":[OSD([sQuery(id+"F2.wireOp",EDGE,"E18.18.0.0"),sQuery(id+"F2.wireOp",EDGE,"E18.18.0.2")])]});
            var Q269;
            Q269=makeQuery(id+"F3.opExtrude","SWEPT_EDGE",EDGE,{"disambiguationData":[OSD([sQuery(id+"F2.wireOp",EDGE,"E18.10.0.0"),sQuery(id+"F2.wireOp",EDGE,"E18.10.0.2")])]});
            var Q270;
            Q270=makeQuery(id+"F3.opExtrude","SWEPT_EDGE",EDGE,{"disambiguationData":[OSD([sQuery(id+"F2.wireOp",EDGE,"E18.26.0.0"),sQuery(id+"F2.wireOp",EDGE,"E18.26.0.2")])]});
            var Q271;
            Q271=makeQuery(id+"F3.opExtrude","SWEPT_EDGE",EDGE,{"disambiguationData":[OSD([sQuery(id+"F2.wireOp",EDGE,"E18.34.0.0"),sQuery(id+"F2.wireOp",EDGE,"E18.34.0.2")])]});
            var Q272;
            Q272=makeQuery(id+"F3.opExtrude","SWEPT_EDGE",EDGE,{"disambiguationData":[OSD([sQuery(id+"F2.wireOp",EDGE,"E18.58.0.0"),sQuery(id+"F2.wireOp",EDGE,"E18.58.0.2")])]});
            var Q273;
            Q273=makeQuery(id+"F3.opExtrude","SWEPT_EDGE",EDGE,{"disambiguationData":[OSD([sQuery(id+"F2.wireOp",EDGE,"E18.14.0.0"),sQuery(id+"F2.wireOp",EDGE,"E18.14.0.2")])]});
            var Q274;
            Q274=makeQuery(id+"F3.opExtrude","SWEPT_EDGE",EDGE,{"disambiguationData":[OSD([sQuery(id+"F2.wireOp",EDGE,"E18.6.0.0"),sQuery(id+"F2.wireOp",EDGE,"E18.6.0.2")])]});
            var Q275;
            Q275=makeQuery(id+"F3.opExtrude","CAP_EDGE",EDGE,{"disambiguationData":[OSD([sQuery(id+"F2.wireOp",EDGE,"E18.57.0.1")])],"isStart":false});
            var Q276;
            Q276=makeQuery(id+"F3.opExtrude","CAP_EDGE",EDGE,{"disambiguationData":[OSD([sQuery(id+"F2.wireOp",EDGE,"E18.55.0.1")])],"isStart":false});
            var Q277;
            Q277=makeQuery(id+"F3.opExtrude","CAP_EDGE",EDGE,{"disambiguationData":[OSD([sQuery(id+"F2.wireOp",EDGE,"E18.53.0.1")])],"isStart":false});
            var Q278;
            Q278=makeQuery(id+"F3.opExtrude","CAP_EDGE",EDGE,{"disambiguationData":[OSD([sQuery(id+"F2.wireOp",EDGE,"E18.51.0.1")])],"isStart":false});
            var Q279;
            Q279=makeQuery(id+"F3.opExtrude","CAP_EDGE",EDGE,{"disambiguationData":[OSD([sQuery(id+"F2.wireOp",EDGE,"E18.49.0.1")])],"isStart":false});
            var Q280;
            Q280=makeQuery(id+"F3.opExtrude","CAP_EDGE",EDGE,{"disambiguationData":[OSD([sQuery(id+"F2.wireOp",EDGE,"E18.47.0.1")])],"isStart":false});
            var Q281;
            Q281=makeQuery(id+"F3.opExtrude","CAP_EDGE",EDGE,{"disambiguationData":[OSD([sQuery(id+"F2.wireOp",EDGE,"E18.45.0.1")])],"isStart":false});
            var Q282;
            Q282=makeQuery(id+"F3.opExtrude","CAP_EDGE",EDGE,{"disambiguationData":[OSD([sQuery(id+"F2.wireOp",EDGE,"E18.43.0.1")])],"isStart":false});
            var Q283;
            Q283=makeQuery(id+"F3.opExtrude","CAP_EDGE",EDGE,{"disambiguationData":[OSD([sQuery(id+"F2.wireOp",EDGE,"E18.41.0.1")])],"isStart":false});
            var Q284;
            Q284=makeQuery(id+"F3.opExtrude","CAP_EDGE",EDGE,{"disambiguationData":[OSD([sQuery(id+"F2.wireOp",EDGE,"E18.39.0.1")])],"isStart":false});
            var Q285;
            Q285=makeQuery(id+"F3.opExtrude","CAP_EDGE",EDGE,{"disambiguationData":[OSD([sQuery(id+"F2.wireOp",EDGE,"E18.37.0.1")])],"isStart":false});
            var Q286;
            Q286=makeQuery(id+"F3.opExtrude","CAP_EDGE",EDGE,{"disambiguationData":[OSD([sQuery(id+"F2.wireOp",EDGE,"E18.35.0.1")])],"isStart":false});
            var Q287;
            Q287=makeQuery(id+"F3.opExtrude","CAP_EDGE",EDGE,{"disambiguationData":[OSD([sQuery(id+"F2.wireOp",EDGE,"E18.33.0.1")])],"isStart":false});
            var Q288;
            Q288=makeQuery(id+"F3.opExtrude","CAP_EDGE",EDGE,{"disambiguationData":[OSD([sQuery(id+"F2.wireOp",EDGE,"E18.31.0.1")])],"isStart":false});
            var Q289;
            Q289=makeQuery(id+"F3.opExtrude","CAP_EDGE",EDGE,{"disambiguationData":[OSD([sQuery(id+"F2.wireOp",EDGE,"E18.29.0.1")])],"isStart":false});
            var Q290;
            Q290=makeQuery(id+"F3.opExtrude","CAP_EDGE",EDGE,{"disambiguationData":[OSD([sQuery(id+"F2.wireOp",EDGE,"E18.27.0.1")])],"isStart":false});
            var Q291;
            Q291=makeQuery(id+"F3.opExtrude","CAP_EDGE",EDGE,{"disambiguationData":[OSD([sQuery(id+"F2.wireOp",EDGE,"E18.25.0.1")])],"isStart":false});
            var Q292;
            Q292=makeQuery(id+"F3.opExtrude","CAP_EDGE",EDGE,{"disambiguationData":[OSD([sQuery(id+"F2.wireOp",EDGE,"E18.23.0.1")])],"isStart":false});
            var Q293;
            Q293=makeQuery(id+"F3.opExtrude","CAP_EDGE",EDGE,{"disambiguationData":[OSD([sQuery(id+"F2.wireOp",EDGE,"E18.21.0.1")])],"isStart":false});
            var Q294;
            Q294=makeQuery(id+"F3.opExtrude","CAP_EDGE",EDGE,{"disambiguationData":[OSD([sQuery(id+"F2.wireOp",EDGE,"E18.19.0.1")])],"isStart":false});
            var Q295;
            Q295=makeQuery(id+"F3.opExtrude","CAP_EDGE",EDGE,{"disambiguationData":[OSD([sQuery(id+"F2.wireOp",EDGE,"E18.17.0.1")])],"isStart":false});
            var Q296;
            Q296=makeQuery(id+"F3.opExtrude","CAP_EDGE",EDGE,{"disambiguationData":[OSD([sQuery(id+"F2.wireOp",EDGE,"E18.15.0.1")])],"isStart":false});
            var Q297;
            Q297=makeQuery(id+"F3.opExtrude","CAP_EDGE",EDGE,{"disambiguationData":[OSD([sQuery(id+"F2.wireOp",EDGE,"E18.13.0.1")])],"isStart":false});
            var Q298;
            Q298=makeQuery(id+"F3.opExtrude","CAP_EDGE",EDGE,{"disambiguationData":[OSD([sQuery(id+"F2.wireOp",EDGE,"E18.11.0.1")])],"isStart":false});
            var Q299;
            Q299=makeQuery(id+"F3.opExtrude","CAP_EDGE",EDGE,{"disambiguationData":[OSD([sQuery(id+"F2.wireOp",EDGE,"E18.9.0.1")])],"isStart":false});
            var Q300;
            Q300=makeQuery(id+"F3.opExtrude","CAP_EDGE",EDGE,{"disambiguationData":[OSD([sQuery(id+"F2.wireOp",EDGE,"E18.7.0.1")])],"isStart":false});
            var Q301;
            Q301=makeQuery(id+"F3.opExtrude","CAP_EDGE",EDGE,{"disambiguationData":[OSD([sQuery(id+"F2.wireOp",EDGE,"E18.5.0.1")])],"isStart":false});
            var Q302;
            Q302=makeQuery(id+"F3.opExtrude","CAP_EDGE",EDGE,{"disambiguationData":[OSD([sQuery(id+"F2.wireOp",EDGE,"E18.3.0.1")])],"isStart":false});
            var Q303;
            Q303=makeQuery(id+"F3.opExtrude","CAP_EDGE",EDGE,{"disambiguationData":[OSD([sQuery(id+"F2.wireOp",EDGE,"E18.1.0.1")])],"isStart":false});
            var Q304;
            Q304=makeQuery(id+"F3.opExtrude","SWEPT_EDGE",EDGE,{"disambiguationData":[OSD([sQuery(id+"F2.wireOp",EDGE,"E18.57.0.1"),sQuery(id+"F2.wireOp",EDGE,"E18.57.0.2")])]});
            var Q305;
            Q305=makeQuery(id+"F3.opExtrude","SWEPT_EDGE",EDGE,{"disambiguationData":[OSD([sQuery(id+"F2.wireOp",EDGE,"E18.53.0.1"),sQuery(id+"F2.wireOp",EDGE,"E18.53.0.2")])]});
            var Q306;
            Q306=makeQuery(id+"F3.opExtrude","SWEPT_EDGE",EDGE,{"disambiguationData":[OSD([sQuery(id+"F2.wireOp",EDGE,"E18.49.0.1"),sQuery(id+"F2.wireOp",EDGE,"E18.49.0.2")])]});
            var Q307;
            Q307=makeQuery(id+"F3.opExtrude","SWEPT_EDGE",EDGE,{"disambiguationData":[OSD([sQuery(id+"F2.wireOp",EDGE,"E18.45.0.1"),sQuery(id+"F2.wireOp",EDGE,"E18.45.0.2")])]});
            var Q308;
            Q308=makeQuery(id+"F3.opExtrude","SWEPT_EDGE",EDGE,{"disambiguationData":[OSD([sQuery(id+"F2.wireOp",EDGE,"E18.41.0.1"),sQuery(id+"F2.wireOp",EDGE,"E18.41.0.2")])]});
            var Q309;
            Q309=makeQuery(id+"F3.opExtrude","SWEPT_EDGE",EDGE,{"disambiguationData":[OSD([sQuery(id+"F2.wireOp",EDGE,"E18.37.0.1"),sQuery(id+"F2.wireOp",EDGE,"E18.37.0.2")])]});
            var Q310;
            Q310=makeQuery(id+"F3.opExtrude","SWEPT_EDGE",EDGE,{"disambiguationData":[OSD([sQuery(id+"F2.wireOp",EDGE,"E18.33.0.1"),sQuery(id+"F2.wireOp",EDGE,"E18.33.0.2")])]});
            var Q311;
            Q311=makeQuery(id+"F3.opExtrude","SWEPT_EDGE",EDGE,{"disambiguationData":[OSD([sQuery(id+"F2.wireOp",EDGE,"E18.29.0.1"),sQuery(id+"F2.wireOp",EDGE,"E18.29.0.2")])]});
            var Q312;
            Q312=makeQuery(id+"F3.opExtrude","SWEPT_EDGE",EDGE,{"disambiguationData":[OSD([sQuery(id+"F2.wireOp",EDGE,"E18.25.0.1"),sQuery(id+"F2.wireOp",EDGE,"E18.25.0.2")])]});
            var Q313;
            Q313=makeQuery(id+"F3.opExtrude","SWEPT_EDGE",EDGE,{"disambiguationData":[OSD([sQuery(id+"F2.wireOp",EDGE,"E18.17.0.1"),sQuery(id+"F2.wireOp",EDGE,"E18.17.0.2")])]});
            var Q314;
            Q314=makeQuery(id+"F3.opExtrude","SWEPT_EDGE",EDGE,{"disambiguationData":[OSD([sQuery(id+"F2.wireOp",EDGE,"E18.21.0.1"),sQuery(id+"F2.wireOp",EDGE,"E18.21.0.2")])]});
            var Q315;
            Q315=makeQuery(id+"F3.opExtrude","SWEPT_EDGE",EDGE,{"disambiguationData":[OSD([sQuery(id+"F2.wireOp",EDGE,"E18.9.0.1"),sQuery(id+"F2.wireOp",EDGE,"E18.9.0.2")])]});
            var Q316;
            Q316=makeQuery(id+"F3.opExtrude","SWEPT_EDGE",EDGE,{"disambiguationData":[OSD([sQuery(id+"F2.wireOp",EDGE,"E18.13.0.1"),sQuery(id+"F2.wireOp",EDGE,"E18.13.0.2")])]});
            var Q317;
            Q317=makeQuery(id+"F3.opExtrude","SWEPT_EDGE",EDGE,{"disambiguationData":[OSD([sQuery(id+"F2.wireOp",EDGE,"E18.5.0.1"),sQuery(id+"F2.wireOp",EDGE,"E18.5.0.2")])]});
            var Q318;
            Q318=makeQuery(id+"F3.opExtrude","CAP_EDGE",EDGE,{"disambiguationData":[OSD([sQuery(id+"F2.wireOp",EDGE,"E18.57.0.0")])],"isStart":false});
            var Q319;
            Q319=makeQuery(id+"F3.opExtrude","CAP_EDGE",EDGE,{"disambiguationData":[OSD([sQuery(id+"F2.wireOp",EDGE,"E18.55.0.0")])],"isStart":false});
            var Q320;
            Q320=makeQuery(id+"F3.opExtrude","CAP_EDGE",EDGE,{"disambiguationData":[OSD([sQuery(id+"F2.wireOp",EDGE,"E18.53.0.0")])],"isStart":false});
            var Q321;
            Q321=makeQuery(id+"F3.opExtrude","CAP_EDGE",EDGE,{"disambiguationData":[OSD([sQuery(id+"F2.wireOp",EDGE,"E18.51.0.0")])],"isStart":false});
            var Q322;
            Q322=makeQuery(id+"F3.opExtrude","CAP_EDGE",EDGE,{"disambiguationData":[OSD([sQuery(id+"F2.wireOp",EDGE,"E18.49.0.0")])],"isStart":false});
            var Q323;
            Q323=makeQuery(id+"F3.opExtrude","CAP_EDGE",EDGE,{"disambiguationData":[OSD([sQuery(id+"F2.wireOp",EDGE,"E18.47.0.0")])],"isStart":false});
            var Q324;
            Q324=makeQuery(id+"F3.opExtrude","CAP_EDGE",EDGE,{"disambiguationData":[OSD([sQuery(id+"F2.wireOp",EDGE,"E18.45.0.0")])],"isStart":false});
            var Q325;
            Q325=makeQuery(id+"F3.opExtrude","CAP_EDGE",EDGE,{"disambiguationData":[OSD([sQuery(id+"F2.wireOp",EDGE,"E18.43.0.0")])],"isStart":false});
            var Q326;
            Q326=makeQuery(id+"F3.opExtrude","CAP_EDGE",EDGE,{"disambiguationData":[OSD([sQuery(id+"F2.wireOp",EDGE,"E18.41.0.0")])],"isStart":false});
            var Q327;
            Q327=makeQuery(id+"F3.opExtrude","CAP_EDGE",EDGE,{"disambiguationData":[OSD([sQuery(id+"F2.wireOp",EDGE,"E18.39.0.0")])],"isStart":false});
            var Q328;
            Q328=makeQuery(id+"F3.opExtrude","CAP_EDGE",EDGE,{"disambiguationData":[OSD([sQuery(id+"F2.wireOp",EDGE,"E18.37.0.0")])],"isStart":false});
            var Q329;
            Q329=makeQuery(id+"F3.opExtrude","CAP_EDGE",EDGE,{"disambiguationData":[OSD([sQuery(id+"F2.wireOp",EDGE,"E18.31.0.0")])],"isStart":false});
            var Q330;
            Q330=makeQuery(id+"F3.opExtrude","CAP_EDGE",EDGE,{"disambiguationData":[OSD([sQuery(id+"F2.wireOp",EDGE,"E18.33.0.0")])],"isStart":false});
            var Q331;
            Q331=makeQuery(id+"F3.opExtrude","CAP_EDGE",EDGE,{"disambiguationData":[OSD([sQuery(id+"F2.wireOp",EDGE,"E18.35.0.0")])],"isStart":false});
            var Q332;
            Q332=makeQuery(id+"F3.opExtrude","CAP_EDGE",EDGE,{"disambiguationData":[OSD([sQuery(id+"F2.wireOp",EDGE,"E18.27.0.0")])],"isStart":false});
            var Q333;
            Q333=makeQuery(id+"F3.opExtrude","CAP_EDGE",EDGE,{"disambiguationData":[OSD([sQuery(id+"F2.wireOp",EDGE,"E18.25.0.0")])],"isStart":false});
            var Q334;
            Q334=makeQuery(id+"F3.opExtrude","CAP_EDGE",EDGE,{"disambiguationData":[OSD([sQuery(id+"F2.wireOp",EDGE,"E18.29.0.0")])],"isStart":false});
            var Q335;
            Q335=makeQuery(id+"F3.opExtrude","CAP_EDGE",EDGE,{"disambiguationData":[OSD([sQuery(id+"F2.wireOp",EDGE,"E18.23.0.0")])],"isStart":false});
            var Q336;
            Q336=makeQuery(id+"F3.opExtrude","CAP_EDGE",EDGE,{"disambiguationData":[OSD([sQuery(id+"F2.wireOp",EDGE,"E18.21.0.0")])],"isStart":false});
            var Q337;
            Q337=makeQuery(id+"F3.opExtrude","CAP_EDGE",EDGE,{"disambiguationData":[OSD([sQuery(id+"F2.wireOp",EDGE,"E18.17.0.0")])],"isStart":false});
            var Q338;
            Q338=makeQuery(id+"F3.opExtrude","CAP_EDGE",EDGE,{"disambiguationData":[OSD([sQuery(id+"F2.wireOp",EDGE,"E18.19.0.0")])],"isStart":false});
            var Q339;
            Q339=makeQuery(id+"F3.opExtrude","CAP_EDGE",EDGE,{"disambiguationData":[OSD([sQuery(id+"F2.wireOp",EDGE,"E18.15.0.0")])],"isStart":false});
            var Q340;
            Q340=makeQuery(id+"F3.opExtrude","CAP_EDGE",EDGE,{"disambiguationData":[OSD([sQuery(id+"F2.wireOp",EDGE,"E18.13.0.0")])],"isStart":false});
            var Q341;
            Q341=makeQuery(id+"F3.opExtrude","CAP_EDGE",EDGE,{"disambiguationData":[OSD([sQuery(id+"F2.wireOp",EDGE,"E18.9.0.0")])],"isStart":false});
            var Q342;
            Q342=makeQuery(id+"F3.opExtrude","CAP_EDGE",EDGE,{"disambiguationData":[OSD([sQuery(id+"F2.wireOp",EDGE,"E18.11.0.0")])],"isStart":false});
            var Q343;
            Q343=makeQuery(id+"F3.opExtrude","CAP_EDGE",EDGE,{"disambiguationData":[OSD([sQuery(id+"F2.wireOp",EDGE,"E18.7.0.0")])],"isStart":false});
            var Q344;
            Q344=makeQuery(id+"F3.opExtrude","CAP_EDGE",EDGE,{"disambiguationData":[OSD([sQuery(id+"F2.wireOp",EDGE,"E18.5.0.0")])],"isStart":false});
            var Q345;
            Q345=makeQuery(id+"F3.opExtrude","CAP_EDGE",EDGE,{"disambiguationData":[OSD([sQuery(id+"F2.wireOp",EDGE,"E18.3.0.0")])],"isStart":false});
            var Q346;
            Q346=makeQuery(id+"F3.opExtrude","CAP_EDGE",EDGE,{"disambiguationData":[OSD([sQuery(id+"F2.wireOp",EDGE,"E18.1.0.0")])],"isStart":false});
            var Q347;
            Q347=makeQuery(id+"F3.opExtrude","SWEPT_EDGE",EDGE,{"disambiguationData":[OSD([sQuery(id+"F2.wireOp",EDGE,"E18.57.0.0"),sQuery(id+"F2.wireOp",EDGE,"E18.57.0.2")])]});
            var Q348;
            Q348=makeQuery(id+"F3.opExtrude","SWEPT_EDGE",EDGE,{"disambiguationData":[OSD([sQuery(id+"F2.wireOp",EDGE,"E18.53.0.0"),sQuery(id+"F2.wireOp",EDGE,"E18.53.0.2")])]});
            var Q349;
            Q349=makeQuery(id+"F3.opExtrude","SWEPT_EDGE",EDGE,{"disambiguationData":[OSD([sQuery(id+"F2.wireOp",EDGE,"E18.49.0.0"),sQuery(id+"F2.wireOp",EDGE,"E18.49.0.2")])]});
            var Q350;
            Q350=makeQuery(id+"F3.opExtrude","SWEPT_EDGE",EDGE,{"disambiguationData":[OSD([sQuery(id+"F2.wireOp",EDGE,"E18.45.0.0"),sQuery(id+"F2.wireOp",EDGE,"E18.45.0.2")])]});
            var Q351;
            Q351=makeQuery(id+"F3.opExtrude","SWEPT_EDGE",EDGE,{"disambiguationData":[OSD([sQuery(id+"F2.wireOp",EDGE,"E18.41.0.0"),sQuery(id+"F2.wireOp",EDGE,"E18.41.0.2")])]});
            var Q352;
            Q352=makeQuery(id+"F3.opExtrude","SWEPT_EDGE",EDGE,{"disambiguationData":[OSD([sQuery(id+"F2.wireOp",EDGE,"E18.37.0.0"),sQuery(id+"F2.wireOp",EDGE,"E18.37.0.2")])]});
            var Q353;
            Q353=makeQuery(id+"F3.opExtrude","SWEPT_EDGE",EDGE,{"disambiguationData":[OSD([sQuery(id+"F2.wireOp",EDGE,"E18.33.0.0"),sQuery(id+"F2.wireOp",EDGE,"E18.33.0.2")])]});
            var Q354;
            Q354=makeQuery(id+"F3.opExtrude","SWEPT_EDGE",EDGE,{"disambiguationData":[OSD([sQuery(id+"F2.wireOp",EDGE,"E18.29.0.0"),sQuery(id+"F2.wireOp",EDGE,"E18.29.0.2")])]});
            var Q355;
            Q355=makeQuery(id+"F3.opExtrude","SWEPT_EDGE",EDGE,{"disambiguationData":[OSD([sQuery(id+"F2.wireOp",EDGE,"E18.25.0.0"),sQuery(id+"F2.wireOp",EDGE,"E18.25.0.2")])]});
            var Q356;
            Q356=makeQuery(id+"F3.opExtrude","SWEPT_EDGE",EDGE,{"disambiguationData":[OSD([sQuery(id+"F2.wireOp",EDGE,"E18.21.0.0"),sQuery(id+"F2.wireOp",EDGE,"E18.21.0.2")])]});
            var Q357;
            Q357=makeQuery(id+"F3.opExtrude","SWEPT_EDGE",EDGE,{"disambiguationData":[OSD([sQuery(id+"F2.wireOp",EDGE,"E18.17.0.0"),sQuery(id+"F2.wireOp",EDGE,"E18.17.0.2")])]});
            var Q358;
            Q358=makeQuery(id+"F3.opExtrude","SWEPT_EDGE",EDGE,{"disambiguationData":[OSD([sQuery(id+"F2.wireOp",EDGE,"E18.13.0.0"),sQuery(id+"F2.wireOp",EDGE,"E18.13.0.2")])]});
            var Q359;
            Q359=makeQuery(id+"F3.opExtrude","SWEPT_EDGE",EDGE,{"disambiguationData":[OSD([sQuery(id+"F2.wireOp",EDGE,"E18.9.0.0"),sQuery(id+"F2.wireOp",EDGE,"E18.9.0.2")])]});
            var Q360;
            Q360=makeQuery(id+"F3.opExtrude","SWEPT_EDGE",EDGE,{"disambiguationData":[OSD([sQuery(id+"F2.wireOp",EDGE,"E18.5.0.0"),sQuery(id+"F2.wireOp",EDGE,"E18.5.0.2")])]});
            var Q361;
            Q361=makeQuery(id+"F3.opExtrude","SWEPT_EDGE",EDGE,{"disambiguationData":[OSD([sQuery(id+"F2.wireOp",EDGE,"E18.56.0.1"),sQuery(id+"F2.wireOp",EDGE,"E18.56.0.2")])]});
            var Q362;
            Q362=makeQuery(id+"F3.opExtrude","SWEPT_EDGE",EDGE,{"disambiguationData":[OSD([sQuery(id+"F2.wireOp",EDGE,"E18.52.0.1"),sQuery(id+"F2.wireOp",EDGE,"E18.52.0.2")])]});
            var Q363;
            Q363=makeQuery(id+"F3.opExtrude","SWEPT_EDGE",EDGE,{"disambiguationData":[OSD([sQuery(id+"F2.wireOp",EDGE,"E18.48.0.1"),sQuery(id+"F2.wireOp",EDGE,"E18.48.0.2")])]});
            var Q364;
            Q364=makeQuery(id+"F3.opExtrude","SWEPT_EDGE",EDGE,{"disambiguationData":[OSD([sQuery(id+"F2.wireOp",EDGE,"E18.44.0.1"),sQuery(id+"F2.wireOp",EDGE,"E18.44.0.2")])]});
            var Q365;
            Q365=makeQuery(id+"F3.opExtrude","SWEPT_EDGE",EDGE,{"disambiguationData":[OSD([sQuery(id+"F2.wireOp",EDGE,"E18.40.0.1"),sQuery(id+"F2.wireOp",EDGE,"E18.40.0.2")])]});
            var Q366;
            Q366=makeQuery(id+"F3.opExtrude","SWEPT_EDGE",EDGE,{"disambiguationData":[OSD([sQuery(id+"F2.wireOp",EDGE,"E18.36.0.1"),sQuery(id+"F2.wireOp",EDGE,"E18.36.0.2")])]});
            var Q367;
            Q367=makeQuery(id+"F3.opExtrude","SWEPT_EDGE",EDGE,{"disambiguationData":[OSD([sQuery(id+"F2.wireOp",EDGE,"E18.28.0.1"),sQuery(id+"F2.wireOp",EDGE,"E18.28.0.2")])]});
            var Q368;
            Q368=makeQuery(id+"F3.opExtrude","SWEPT_EDGE",EDGE,{"disambiguationData":[OSD([sQuery(id+"F2.wireOp",EDGE,"E18.32.0.1"),sQuery(id+"F2.wireOp",EDGE,"E18.32.0.2")])]});
            var Q369;
            Q369=makeQuery(id+"F3.opExtrude","SWEPT_EDGE",EDGE,{"disambiguationData":[OSD([sQuery(id+"F2.wireOp",EDGE,"E18.24.0.1"),sQuery(id+"F2.wireOp",EDGE,"E18.24.0.2")])]});
            var Q370;
            Q370=makeQuery(id+"F3.opExtrude","SWEPT_EDGE",EDGE,{"disambiguationData":[OSD([sQuery(id+"F2.wireOp",EDGE,"E18.20.0.1"),sQuery(id+"F2.wireOp",EDGE,"E18.20.0.2")])]});
            var Q371;
            Q371=makeQuery(id+"F3.opExtrude","SWEPT_EDGE",EDGE,{"disambiguationData":[OSD([sQuery(id+"F2.wireOp",EDGE,"E18.12.0.1"),sQuery(id+"F2.wireOp",EDGE,"E18.12.0.2")])]});
            var Q372;
            Q372=makeQuery(id+"F3.opExtrude","SWEPT_EDGE",EDGE,{"disambiguationData":[OSD([sQuery(id+"F2.wireOp",EDGE,"E18.16.0.1"),sQuery(id+"F2.wireOp",EDGE,"E18.16.0.2")])]});
            var Q373;
            Q373=makeQuery(id+"F3.opExtrude","SWEPT_EDGE",EDGE,{"disambiguationData":[OSD([sQuery(id+"F2.wireOp",EDGE,"E18.8.0.1"),sQuery(id+"F2.wireOp",EDGE,"E18.8.0.2")])]});
            var Q374;
            Q374=makeQuery(id+"F3.opExtrude","SWEPT_EDGE",EDGE,{"disambiguationData":[OSD([sQuery(id+"F2.wireOp",EDGE,"E18.4.0.1"),sQuery(id+"F2.wireOp",EDGE,"E18.4.0.2")])]});
            var Q375;
            Q375=makeQuery(id+"F3.opExtrude","CAP_EDGE",EDGE,{"disambiguationData":[OSD([sQuery(id+"F2.wireOp",EDGE,"E18.52.0.2")])],"isStart":false});
            var Q376;
            Q376=makeQuery(id+"F3.opExtrude","CAP_EDGE",EDGE,{"disambiguationData":[OSD([sQuery(id+"F2.wireOp",EDGE,"E18.42.0.2")])],"isStart":false});
            var Q377;
            Q377=makeQuery(id+"F3.opExtrude","CAP_EDGE",EDGE,{"disambiguationData":[OSD([sQuery(id+"F2.wireOp",EDGE,"E18.34.0.2")])],"isStart":false});
            var Q378;
            Q378=makeQuery(id+"F3.opExtrude","CAP_EDGE",EDGE,{"disambiguationData":[OSD([sQuery(id+"F2.wireOp",EDGE,"E16.right")])],"isStart":false});
            var Q379;
            Q379=makeQuery(id+"F3.opExtrude","SWEPT_EDGE",EDGE,{"disambiguationData":[OSD([sQuery(id+"F2.wireOp",EDGE,"E18.56.0.0"),sQuery(id+"F2.wireOp",EDGE,"E18.56.0.2")])]});
            var Q380;
            Q380=makeQuery(id+"F3.opExtrude","SWEPT_EDGE",EDGE,{"disambiguationData":[OSD([sQuery(id+"F2.wireOp",EDGE,"E18.52.0.0"),sQuery(id+"F2.wireOp",EDGE,"E18.52.0.2")])]});
            var Q381;
            Q381=makeQuery(id+"F3.opExtrude","SWEPT_EDGE",EDGE,{"disambiguationData":[OSD([sQuery(id+"F2.wireOp",EDGE,"E18.48.0.0"),sQuery(id+"F2.wireOp",EDGE,"E18.48.0.2")])]});
            var Q382;
            Q382=makeQuery(id+"F3.opExtrude","SWEPT_EDGE",EDGE,{"disambiguationData":[OSD([sQuery(id+"F2.wireOp",EDGE,"E18.44.0.0"),sQuery(id+"F2.wireOp",EDGE,"E18.44.0.2")])]});
            var Q383;
            Q383=makeQuery(id+"F3.opExtrude","SWEPT_EDGE",EDGE,{"disambiguationData":[OSD([sQuery(id+"F2.wireOp",EDGE,"E18.40.0.0"),sQuery(id+"F2.wireOp",EDGE,"E18.40.0.2")])]});
            var Q384;
            Q384=makeQuery(id+"F3.opExtrude","SWEPT_EDGE",EDGE,{"disambiguationData":[OSD([sQuery(id+"F2.wireOp",EDGE,"E18.36.0.0"),sQuery(id+"F2.wireOp",EDGE,"E18.36.0.2")])]});
            var Q385;
            Q385=makeQuery(id+"F3.opExtrude","SWEPT_EDGE",EDGE,{"disambiguationData":[OSD([sQuery(id+"F2.wireOp",EDGE,"E18.32.0.0"),sQuery(id+"F2.wireOp",EDGE,"E18.32.0.2")])]});
            var Q386;
            Q386=makeQuery(id+"F3.opExtrude","SWEPT_EDGE",EDGE,{"disambiguationData":[OSD([sQuery(id+"F2.wireOp",EDGE,"E18.28.0.0"),sQuery(id+"F2.wireOp",EDGE,"E18.28.0.2")])]});
            var Q387;
            Q387=makeQuery(id+"F3.opExtrude","SWEPT_EDGE",EDGE,{"disambiguationData":[OSD([sQuery(id+"F2.wireOp",EDGE,"E18.24.0.0"),sQuery(id+"F2.wireOp",EDGE,"E18.24.0.2")])]});
            var Q388;
            Q388=makeQuery(id+"F3.opExtrude","SWEPT_EDGE",EDGE,{"disambiguationData":[OSD([sQuery(id+"F2.wireOp",EDGE,"E18.20.0.0"),sQuery(id+"F2.wireOp",EDGE,"E18.20.0.2")])]});
            var Q389;
            Q389=makeQuery(id+"F3.opExtrude","SWEPT_EDGE",EDGE,{"disambiguationData":[OSD([sQuery(id+"F2.wireOp",EDGE,"E18.16.0.0"),sQuery(id+"F2.wireOp",EDGE,"E18.16.0.2")])]});
            var Q390;
            Q390=makeQuery(id+"F3.opExtrude","SWEPT_EDGE",EDGE,{"disambiguationData":[OSD([sQuery(id+"F2.wireOp",EDGE,"E18.12.0.0"),sQuery(id+"F2.wireOp",EDGE,"E18.12.0.2")])]});
            var Q391;
            Q391=makeQuery(id+"F3.opExtrude","SWEPT_EDGE",EDGE,{"disambiguationData":[OSD([sQuery(id+"F2.wireOp",EDGE,"E18.8.0.0"),sQuery(id+"F2.wireOp",EDGE,"E18.8.0.2")])]});
            var Q392;
            Q392=makeQuery(id+"F3.opExtrude","SWEPT_EDGE",EDGE,{"disambiguationData":[OSD([sQuery(id+"F2.wireOp",EDGE,"E18.4.0.0"),sQuery(id+"F2.wireOp",EDGE,"E18.4.0.2")])]});
            var Q393;
            Q393=makeQuery(id+"F3.opExtrude","CAP_EDGE",EDGE,{"disambiguationData":[OSD([sQuery(id+"F2.wireOp",EDGE,"E18.58.0.1")])],"isStart":false});
            var Q394;
            Q394=makeQuery(id+"F3.opExtrude","CAP_EDGE",EDGE,{"disambiguationData":[OSD([sQuery(id+"F2.wireOp",EDGE,"E18.56.0.1")])],"isStart":false});
            var Q395;
            Q395=makeQuery(id+"F3.opExtrude","CAP_EDGE",EDGE,{"disambiguationData":[OSD([sQuery(id+"F2.wireOp",EDGE,"E18.54.0.1")])],"isStart":false});
            var Q396;
            Q396=makeQuery(id+"F3.opExtrude","CAP_EDGE",EDGE,{"disambiguationData":[OSD([sQuery(id+"F2.wireOp",EDGE,"E18.52.0.1")])],"isStart":false});
            var Q397;
            Q397=makeQuery(id+"F3.opExtrude","CAP_EDGE",EDGE,{"disambiguationData":[OSD([sQuery(id+"F2.wireOp",EDGE,"E18.48.0.1")])],"isStart":false});
            var Q398;
            Q398=makeQuery(id+"F3.opExtrude","CAP_EDGE",EDGE,{"disambiguationData":[OSD([sQuery(id+"F2.wireOp",EDGE,"E18.50.0.1")])],"isStart":false});
            var Q399;
            Q399=makeQuery(id+"F3.opExtrude","CAP_EDGE",EDGE,{"disambiguationData":[OSD([sQuery(id+"F2.wireOp",EDGE,"E18.46.0.1")])],"isStart":false});
            var Q400;
            Q400=makeQuery(id+"F3.opExtrude","CAP_EDGE",EDGE,{"disambiguationData":[OSD([sQuery(id+"F2.wireOp",EDGE,"E18.44.0.1")])],"isStart":false});
            var Q401;
            Q401=makeQuery(id+"F3.opExtrude","CAP_EDGE",EDGE,{"disambiguationData":[OSD([sQuery(id+"F2.wireOp",EDGE,"E18.42.0.1")])],"isStart":false});
            var Q402;
            Q402=makeQuery(id+"F3.opExtrude","CAP_EDGE",EDGE,{"disambiguationData":[OSD([sQuery(id+"F2.wireOp",EDGE,"E18.40.0.1")])],"isStart":false});
            var Q403;
            Q403=makeQuery(id+"F3.opExtrude","CAP_EDGE",EDGE,{"disambiguationData":[OSD([sQuery(id+"F2.wireOp",EDGE,"E18.38.0.1")])],"isStart":false});
            var Q404;
            Q404=makeQuery(id+"F3.opExtrude","CAP_EDGE",EDGE,{"disambiguationData":[OSD([sQuery(id+"F2.wireOp",EDGE,"E18.36.0.1")])],"isStart":false});
            var Q405;
            Q405=makeQuery(id+"F3.opExtrude","CAP_EDGE",EDGE,{"disambiguationData":[OSD([sQuery(id+"F2.wireOp",EDGE,"E18.34.0.1")])],"isStart":false});
            var Q406;
            Q406=makeQuery(id+"F3.opExtrude","CAP_EDGE",EDGE,{"disambiguationData":[OSD([sQuery(id+"F2.wireOp",EDGE,"E18.32.0.1")])],"isStart":false});
            var Q407;
            Q407=makeQuery(id+"F3.opExtrude","CAP_EDGE",EDGE,{"disambiguationData":[OSD([sQuery(id+"F2.wireOp",EDGE,"E18.30.0.1")])],"isStart":false});
            var Q408;
            Q408=makeQuery(id+"F3.opExtrude","CAP_EDGE",EDGE,{"disambiguationData":[OSD([sQuery(id+"F2.wireOp",EDGE,"E18.28.0.1")])],"isStart":false});
            var Q409;
            Q409=makeQuery(id+"F3.opExtrude","CAP_EDGE",EDGE,{"disambiguationData":[OSD([sQuery(id+"F2.wireOp",EDGE,"E18.26.0.1")])],"isStart":false});
            var Q410;
            Q410=makeQuery(id+"F3.opExtrude","CAP_EDGE",EDGE,{"disambiguationData":[OSD([sQuery(id+"F2.wireOp",EDGE,"E18.24.0.1")])],"isStart":false});
            var Q411;
            Q411=makeQuery(id+"F3.opExtrude","CAP_EDGE",EDGE,{"disambiguationData":[OSD([sQuery(id+"F2.wireOp",EDGE,"E18.22.0.1")])],"isStart":false});
            var Q412;
            Q412=makeQuery(id+"F3.opExtrude","CAP_EDGE",EDGE,{"disambiguationData":[OSD([sQuery(id+"F2.wireOp",EDGE,"E18.20.0.1")])],"isStart":false});
            var Q413;
            Q413=makeQuery(id+"F3.opExtrude","CAP_EDGE",EDGE,{"disambiguationData":[OSD([sQuery(id+"F2.wireOp",EDGE,"E18.18.0.1")])],"isStart":false});
            var Q414;
            Q414=makeQuery(id+"F3.opExtrude","CAP_EDGE",EDGE,{"disambiguationData":[OSD([sQuery(id+"F2.wireOp",EDGE,"E18.16.0.1")])],"isStart":false});
            var Q415;
            Q415=makeQuery(id+"F3.opExtrude","CAP_EDGE",EDGE,{"disambiguationData":[OSD([sQuery(id+"F2.wireOp",EDGE,"E18.14.0.1")])],"isStart":false});
            var Q416;
            Q416=makeQuery(id+"F3.opExtrude","CAP_EDGE",EDGE,{"disambiguationData":[OSD([sQuery(id+"F2.wireOp",EDGE,"E18.12.0.1")])],"isStart":false});
            var Q417;
            Q417=makeQuery(id+"F3.opExtrude","CAP_EDGE",EDGE,{"disambiguationData":[OSD([sQuery(id+"F2.wireOp",EDGE,"E18.10.0.1")])],"isStart":false});
            var Q418;
            Q418=makeQuery(id+"F3.opExtrude","CAP_EDGE",EDGE,{"disambiguationData":[OSD([sQuery(id+"F2.wireOp",EDGE,"E18.8.0.1")])],"isStart":false});
            var Q419;
            Q419=makeQuery(id+"F3.opExtrude","CAP_EDGE",EDGE,{"disambiguationData":[OSD([sQuery(id+"F2.wireOp",EDGE,"E18.6.0.1")])],"isStart":false});
            var Q420;
            Q420=makeQuery(id+"F3.opExtrude","CAP_EDGE",EDGE,{"disambiguationData":[OSD([sQuery(id+"F2.wireOp",EDGE,"E18.4.0.1")])],"isStart":false});
            var Q421;
            Q421=makeQuery(id+"F3.opExtrude","CAP_EDGE",EDGE,{"disambiguationData":[OSD([sQuery(id+"F2.wireOp",EDGE,"E18.2.0.1")])],"isStart":false});
            var Q422;
            Q422=makeQuery(id+"F3.opExtrude","CAP_EDGE",EDGE,{"disambiguationData":[OSD([sQuery(id+"F2.wireOp",EDGE,"E16.left")])],"isStart":false});
            var Q423;
            Q423=makeQuery(id+"F3.opExtrude","SWEPT_EDGE",EDGE,{"disambiguationData":[OSD([sQuery(id+"F2.wireOp",EDGE,"E18.55.0.1"),sQuery(id+"F2.wireOp",EDGE,"E18.55.0.2")])]});
            var Q424;
            Q424=makeQuery(id+"F3.opExtrude","SWEPT_EDGE",EDGE,{"disambiguationData":[OSD([sQuery(id+"F2.wireOp",EDGE,"E18.51.0.1"),sQuery(id+"F2.wireOp",EDGE,"E18.51.0.2")])]});
            var Q425;
            Q425=makeQuery(id+"F3.opExtrude","SWEPT_EDGE",EDGE,{"disambiguationData":[OSD([sQuery(id+"F2.wireOp",EDGE,"E18.47.0.1"),sQuery(id+"F2.wireOp",EDGE,"E18.47.0.2")])]});
            var Q426;
            Q426=makeQuery(id+"F3.opExtrude","SWEPT_EDGE",EDGE,{"disambiguationData":[OSD([sQuery(id+"F2.wireOp",EDGE,"E18.43.0.1"),sQuery(id+"F2.wireOp",EDGE,"E18.43.0.2")])]});
            var Q427;
            Q427=makeQuery(id+"F3.opExtrude","SWEPT_EDGE",EDGE,{"disambiguationData":[OSD([sQuery(id+"F2.wireOp",EDGE,"E18.39.0.1"),sQuery(id+"F2.wireOp",EDGE,"E18.39.0.2")])]});
            var Q428;
            Q428=makeQuery(id+"F3.opExtrude","SWEPT_EDGE",EDGE,{"disambiguationData":[OSD([sQuery(id+"F2.wireOp",EDGE,"E18.35.0.1"),sQuery(id+"F2.wireOp",EDGE,"E18.35.0.2")])]});
            var Q429;
            Q429=makeQuery(id+"F3.opExtrude","SWEPT_EDGE",EDGE,{"disambiguationData":[OSD([sQuery(id+"F2.wireOp",EDGE,"E18.31.0.1"),sQuery(id+"F2.wireOp",EDGE,"E18.31.0.2")])]});
            var Q430;
            Q430=makeQuery(id+"F3.opExtrude","SWEPT_EDGE",EDGE,{"disambiguationData":[OSD([sQuery(id+"F2.wireOp",EDGE,"E18.27.0.1"),sQuery(id+"F2.wireOp",EDGE,"E18.27.0.2")])]});
            var Q431;
            Q431=makeQuery(id+"F3.opExtrude","SWEPT_EDGE",EDGE,{"disambiguationData":[OSD([sQuery(id+"F2.wireOp",EDGE,"E18.23.0.1"),sQuery(id+"F2.wireOp",EDGE,"E18.23.0.2")])]});
            var Q432;
            Q432=makeQuery(id+"F3.opExtrude","SWEPT_EDGE",EDGE,{"disambiguationData":[OSD([sQuery(id+"F2.wireOp",EDGE,"E18.19.0.1"),sQuery(id+"F2.wireOp",EDGE,"E18.19.0.2")])]});
            var Q433;
            Q433=makeQuery(id+"F3.opExtrude","SWEPT_EDGE",EDGE,{"disambiguationData":[OSD([sQuery(id+"F2.wireOp",EDGE,"E18.15.0.1"),sQuery(id+"F2.wireOp",EDGE,"E18.15.0.2")])]});
            var Q434;
            Q434=makeQuery(id+"F3.opExtrude","SWEPT_EDGE",EDGE,{"disambiguationData":[OSD([sQuery(id+"F2.wireOp",EDGE,"E18.11.0.1"),sQuery(id+"F2.wireOp",EDGE,"E18.11.0.2")])]});
            var Q435;
            Q435=makeQuery(id+"F3.opExtrude","SWEPT_EDGE",EDGE,{"disambiguationData":[OSD([sQuery(id+"F2.wireOp",EDGE,"E18.7.0.1"),sQuery(id+"F2.wireOp",EDGE,"E18.7.0.2")])]});
            var Q436;
            Q436=makeQuery(id+"F3.opExtrude","CAP_EDGE",EDGE,{"disambiguationData":[OSD([sQuery(id+"F2.wireOp",EDGE,"E18.58.0.0")])],"isStart":false});
            var Q437;
            Q437=makeQuery(id+"F3.opExtrude","CAP_EDGE",EDGE,{"disambiguationData":[OSD([sQuery(id+"F2.wireOp",EDGE,"E18.56.0.0")])],"isStart":false});
            var Q438;
            Q438=makeQuery(id+"F3.opExtrude","CAP_EDGE",EDGE,{"disambiguationData":[OSD([sQuery(id+"F2.wireOp",EDGE,"E18.54.0.0")])],"isStart":false});
            var Q439;
            Q439=makeQuery(id+"F3.opExtrude","CAP_EDGE",EDGE,{"disambiguationData":[OSD([sQuery(id+"F2.wireOp",EDGE,"E18.52.0.0")])],"isStart":false});
            var Q440;
            Q440=makeQuery(id+"F3.opExtrude","CAP_EDGE",EDGE,{"disambiguationData":[OSD([sQuery(id+"F2.wireOp",EDGE,"E18.50.0.0")])],"isStart":false});
            var Q441;
            Q441=makeQuery(id+"F3.opExtrude","CAP_EDGE",EDGE,{"disambiguationData":[OSD([sQuery(id+"F2.wireOp",EDGE,"E18.48.0.0")])],"isStart":false});
            var Q442;
            Q442=makeQuery(id+"F3.opExtrude","CAP_EDGE",EDGE,{"disambiguationData":[OSD([sQuery(id+"F2.wireOp",EDGE,"E18.46.0.0")])],"isStart":false});
            var Q443;
            Q443=makeQuery(id+"F3.opExtrude","CAP_EDGE",EDGE,{"disambiguationData":[OSD([sQuery(id+"F2.wireOp",EDGE,"E18.44.0.0")])],"isStart":false});
            var Q444;
            Q444=makeQuery(id+"F3.opExtrude","CAP_EDGE",EDGE,{"disambiguationData":[OSD([sQuery(id+"F2.wireOp",EDGE,"E18.42.0.0")])],"isStart":false});
            var Q445;
            Q445=makeQuery(id+"F3.opExtrude","CAP_EDGE",EDGE,{"disambiguationData":[OSD([sQuery(id+"F2.wireOp",EDGE,"E18.40.0.0")])],"isStart":false});
            var Q446;
            Q446=makeQuery(id+"F3.opExtrude","CAP_EDGE",EDGE,{"disambiguationData":[OSD([sQuery(id+"F2.wireOp",EDGE,"E18.38.0.0")])],"isStart":false});
            var Q447;
            Q447=makeQuery(id+"F3.opExtrude","CAP_EDGE",EDGE,{"disambiguationData":[OSD([sQuery(id+"F2.wireOp",EDGE,"E18.36.0.0")])],"isStart":false});
            var Q448;
            Q448=makeQuery(id+"F3.opExtrude","CAP_EDGE",EDGE,{"disambiguationData":[OSD([sQuery(id+"F2.wireOp",EDGE,"E18.34.0.0")])],"isStart":false});
            var Q449;
            Q449=makeQuery(id+"F3.opExtrude","CAP_EDGE",EDGE,{"disambiguationData":[OSD([sQuery(id+"F2.wireOp",EDGE,"E18.32.0.0")])],"isStart":false});
            var Q450;
            Q450=makeQuery(id+"F3.opExtrude","CAP_EDGE",EDGE,{"disambiguationData":[OSD([sQuery(id+"F2.wireOp",EDGE,"E18.30.0.0")])],"isStart":false});
            var Q451;
            Q451=makeQuery(id+"F3.opExtrude","CAP_EDGE",EDGE,{"disambiguationData":[OSD([sQuery(id+"F2.wireOp",EDGE,"E18.28.0.0")])],"isStart":false});
            var Q452;
            Q452=makeQuery(id+"F3.opExtrude","CAP_EDGE",EDGE,{"disambiguationData":[OSD([sQuery(id+"F2.wireOp",EDGE,"E18.26.0.0")])],"isStart":false});
            var Q453;
            Q453=makeQuery(id+"F3.opExtrude","CAP_EDGE",EDGE,{"disambiguationData":[OSD([sQuery(id+"F2.wireOp",EDGE,"E18.24.0.0")])],"isStart":false});
            var Q454;
            Q454=makeQuery(id+"F3.opExtrude","CAP_EDGE",EDGE,{"disambiguationData":[OSD([sQuery(id+"F2.wireOp",EDGE,"E18.22.0.0")])],"isStart":false});
            var Q455;
            Q455=makeQuery(id+"F3.opExtrude","CAP_EDGE",EDGE,{"disambiguationData":[OSD([sQuery(id+"F2.wireOp",EDGE,"E18.20.0.0")])],"isStart":false});
            var Q456;
            Q456=makeQuery(id+"F3.opExtrude","CAP_EDGE",EDGE,{"disambiguationData":[OSD([sQuery(id+"F2.wireOp",EDGE,"E18.16.0.0")])],"isStart":false});
            var Q457;
            Q457=makeQuery(id+"F3.opExtrude","CAP_EDGE",EDGE,{"disambiguationData":[OSD([sQuery(id+"F2.wireOp",EDGE,"E18.18.0.0")])],"isStart":false});
            var Q458;
            Q458=makeQuery(id+"F3.opExtrude","CAP_EDGE",EDGE,{"disambiguationData":[OSD([sQuery(id+"F2.wireOp",EDGE,"E18.12.0.0")])],"isStart":false});
            var Q459;
            Q459=makeQuery(id+"F3.opExtrude","CAP_EDGE",EDGE,{"disambiguationData":[OSD([sQuery(id+"F2.wireOp",EDGE,"E18.14.0.0")])],"isStart":false});
            var Q460;
            Q460=makeQuery(id+"F3.opExtrude","CAP_EDGE",EDGE,{"disambiguationData":[OSD([sQuery(id+"F2.wireOp",EDGE,"E18.10.0.0")])],"isStart":false});
            var Q461;
            Q461=makeQuery(id+"F3.opExtrude","CAP_EDGE",EDGE,{"disambiguationData":[OSD([sQuery(id+"F2.wireOp",EDGE,"E18.8.0.0")])],"isStart":false});
            var Q462;
            Q462=makeQuery(id+"F3.opExtrude","CAP_EDGE",EDGE,{"disambiguationData":[OSD([sQuery(id+"F2.wireOp",EDGE,"E18.6.0.0")])],"isStart":false});
            var Q463;
            Q463=makeQuery(id+"F3.opExtrude","CAP_EDGE",EDGE,{"disambiguationData":[OSD([sQuery(id+"F2.wireOp",EDGE,"E18.4.0.0")])],"isStart":false});
            var Q464;
            Q464=makeQuery(id+"F3.opExtrude","CAP_EDGE",EDGE,{"disambiguationData":[OSD([sQuery(id+"F2.wireOp",EDGE,"E18.2.0.0")])],"isStart":false});
            var Q465;
            Q465=makeQuery(id+"F3.opExtrude","SWEPT_EDGE",EDGE,{"disambiguationData":[OSD([sQuery(id+"F2.wireOp",EDGE,"E18.51.0.0"),sQuery(id+"F2.wireOp",EDGE,"E18.51.0.2")])]});
            var Q466;
            Q466=makeQuery(id+"F3.opExtrude","SWEPT_EDGE",EDGE,{"disambiguationData":[OSD([sQuery(id+"F2.wireOp",EDGE,"E18.55.0.0"),sQuery(id+"F2.wireOp",EDGE,"E18.55.0.2")])]});
            var Q467;
            Q467=makeQuery(id+"F3.opExtrude","SWEPT_EDGE",EDGE,{"disambiguationData":[OSD([sQuery(id+"F2.wireOp",EDGE,"E18.47.0.0"),sQuery(id+"F2.wireOp",EDGE,"E18.47.0.2")])]});
            var Q468;
            Q468=makeQuery(id+"F3.opExtrude","SWEPT_EDGE",EDGE,{"disambiguationData":[OSD([sQuery(id+"F2.wireOp",EDGE,"E18.43.0.0"),sQuery(id+"F2.wireOp",EDGE,"E18.43.0.2")])]});
            var Q469;
            Q469=makeQuery(id+"F3.opExtrude","SWEPT_EDGE",EDGE,{"disambiguationData":[OSD([sQuery(id+"F2.wireOp",EDGE,"E18.39.0.0"),sQuery(id+"F2.wireOp",EDGE,"E18.39.0.2")])]});
            var Q470;
            Q470=makeQuery(id+"F3.opExtrude","SWEPT_EDGE",EDGE,{"disambiguationData":[OSD([sQuery(id+"F2.wireOp",EDGE,"E18.35.0.0"),sQuery(id+"F2.wireOp",EDGE,"E18.35.0.2")])]});
            var Q471;
            Q471=makeQuery(id+"F3.opExtrude","SWEPT_EDGE",EDGE,{"disambiguationData":[OSD([sQuery(id+"F2.wireOp",EDGE,"E18.31.0.0"),sQuery(id+"F2.wireOp",EDGE,"E18.31.0.2")])]});
            var Q472;
            Q472=makeQuery(id+"F3.opExtrude","SWEPT_EDGE",EDGE,{"disambiguationData":[OSD([sQuery(id+"F2.wireOp",EDGE,"E18.27.0.0"),sQuery(id+"F2.wireOp",EDGE,"E18.27.0.2")])]});
            var Q473;
            Q473=makeQuery(id+"F3.opExtrude","SWEPT_EDGE",EDGE,{"disambiguationData":[OSD([sQuery(id+"F2.wireOp",EDGE,"E18.23.0.0"),sQuery(id+"F2.wireOp",EDGE,"E18.23.0.2")])]});
            var Q474;
            Q474=makeQuery(id+"F3.opExtrude","SWEPT_EDGE",EDGE,{"disambiguationData":[OSD([sQuery(id+"F2.wireOp",EDGE,"E18.19.0.0"),sQuery(id+"F2.wireOp",EDGE,"E18.19.0.2")])]});
            var Q475;
            Q475=makeQuery(id+"F3.opExtrude","SWEPT_EDGE",EDGE,{"disambiguationData":[OSD([sQuery(id+"F2.wireOp",EDGE,"E18.15.0.0"),sQuery(id+"F2.wireOp",EDGE,"E18.15.0.2")])]});
            var Q476;
            Q476=makeQuery(id+"F3.opExtrude","SWEPT_EDGE",EDGE,{"disambiguationData":[OSD([sQuery(id+"F2.wireOp",EDGE,"E18.11.0.0"),sQuery(id+"F2.wireOp",EDGE,"E18.11.0.2")])]});
            var Q477;
            Q477=makeQuery(id+"F3.opExtrude","SWEPT_EDGE",EDGE,{"disambiguationData":[OSD([sQuery(id+"F2.wireOp",EDGE,"E18.7.0.0"),sQuery(id+"F2.wireOp",EDGE,"E18.7.0.2")])]});
            var Q478;
            Q478=makeQuery(id+"F3.opExtrude","SWEPT_EDGE",EDGE,{"disambiguationData":[OSD([sQuery(id+"F2.wireOp",EDGE,"E18.5.0.1"),sQuery(id+"F2.wireOp",EDGE,"E18.5.0.3")])]});
            var Q479;
            Q479=makeQuery(id+"F3.opExtrude","SWEPT_EDGE",EDGE,{"disambiguationData":[OSD([sQuery(id+"F2.wireOp",EDGE,"E18.4.0.1"),sQuery(id+"F2.wireOp",EDGE,"E18.4.0.3")])]});
            var Q480;
            Q480=makeQuery(id+"F3.opExtrude","SWEPT_EDGE",EDGE,{"disambiguationData":[OSD([sQuery(id+"F2.wireOp",EDGE,"E18.4.0.0"),sQuery(id+"F2.wireOp",EDGE,"E18.4.0.3")])]});
            var Q481;
            Q481=makeQuery(id+"F3.opExtrude","SWEPT_EDGE",EDGE,{"disambiguationData":[OSD([sQuery(id+"F2.wireOp",EDGE,"E18.3.0.0"),sQuery(id+"F2.wireOp",EDGE,"E18.3.0.3")])]});
            var Q482;
            Q482=makeQuery(id+"F3.opExtrude","SWEPT_EDGE",EDGE,{"disambiguationData":[OSD([sQuery(id+"F2.wireOp",EDGE,"E18.1.0.1"),sQuery(id+"F2.wireOp",EDGE,"E18.1.0.3")])]});
            var Q483;
            Q483=makeQuery(id+"F3.opExtrude","SWEPT_EDGE",EDGE,{"disambiguationData":[OSD([sQuery(id+"F2.wireOp",EDGE,"E18.1.0.0"),sQuery(id+"F2.wireOp",EDGE,"E18.1.0.3")])]});
            var Q484;
            Q484=makeQuery(id+"F3.opExtrude","SWEPT_EDGE",EDGE,{"disambiguationData":[OSD([sQuery(id+"F2.wireOp",EDGE,"E16.bottom"),sQuery(id+"F2.wireOp",EDGE,"E16.left")])]});
            var Q485;
            Q485=makeQuery(id+"F3.opExtrude","SWEPT_EDGE",EDGE,{"disambiguationData":[OSD([sQuery(id+"F2.wireOp",EDGE,"E18.7.0.1"),sQuery(id+"F2.wireOp",EDGE,"E18.7.0.3")])]});
            var Q486;
            Q486=makeQuery(id+"F3.opExtrude","SWEPT_EDGE",EDGE,{"disambiguationData":[OSD([sQuery(id+"F2.wireOp",EDGE,"E18.7.0.0"),sQuery(id+"F2.wireOp",EDGE,"E18.7.0.3")])]});
            var Q487;
            Q487=makeQuery(id+"F3.opExtrude","SWEPT_EDGE",EDGE,{"disambiguationData":[OSD([sQuery(id+"F2.wireOp",EDGE,"E18.2.0.1"),sQuery(id+"F2.wireOp",EDGE,"E18.2.0.2")])]});
            var Q488;
            Q488=makeQuery(id+"F3.opExtrude","SWEPT_EDGE",EDGE,{"disambiguationData":[OSD([sQuery(id+"F2.wireOp",EDGE,"E18.2.0.0"),sQuery(id+"F2.wireOp",EDGE,"E18.2.0.2")])]});
            var Q489;
            Q489=makeQuery(id+"F3.opExtrude","SWEPT_EDGE",EDGE,{"disambiguationData":[OSD([sQuery(id+"F2.wireOp",EDGE,"E18.1.0.1"),sQuery(id+"F2.wireOp",EDGE,"E18.1.0.2")])]});
            var Q490;
            Q490=makeQuery(id+"F3.opExtrude","SWEPT_EDGE",EDGE,{"disambiguationData":[OSD([sQuery(id+"F2.wireOp",EDGE,"E18.1.0.0"),sQuery(id+"F2.wireOp",EDGE,"E18.1.0.2")])]});
            var Q491;
            Q491=makeQuery(id+"F3.opExtrude","CAP_EDGE",EDGE,{"disambiguationData":[OSD([sQuery(id+"F2.wireOp",EDGE,"E18.25.0.2")])],"isStart":false});
            var Q492;
            Q492=makeQuery(id+"F3.opExtrude","CAP_EDGE",EDGE,{"disambiguationData":[OSD([sQuery(id+"F2.wireOp",EDGE,"E18.15.0.2")])],"isStart":false});
            var Q493;
            Q493=makeQuery(id+"F3.opExtrude","CAP_EDGE",EDGE,{"disambiguationData":[OSD([sQuery(id+"F2.wireOp",EDGE,"E18.10.0.3")])],"isStart":false});
            var Q494;
            Q494=makeQuery(id+"F3.opExtrude","CAP_EDGE",EDGE,{"disambiguationData":[OSD([sQuery(id+"F2.wireOp",EDGE,"E18.21.0.3")])],"isStart":false});
            var Q495;
            Q495=makeQuery(id+"F3.opExtrude","CAP_EDGE",EDGE,{"disambiguationData":[OSD([sQuery(id+"F2.wireOp",EDGE,"E18.26.0.3")])],"isStart":false});
            var Q496;
            Q496=makeQuery(id+"F3.opExtrude","CAP_EDGE",EDGE,{"disambiguationData":[OSD([sQuery(id+"F2.wireOp",EDGE,"E18.58.0.3")])],"isStart":false});
            var Q497;
            Q497=makeQuery(id+"F3.opExtrude","CAP_EDGE",EDGE,{"disambiguationData":[OSD([sQuery(id+"F2.wireOp",EDGE,"E18.53.0.3")])],"isStart":false});
            var Q498;
            Q498=makeQuery(id+"F3.opExtrude","SWEPT_EDGE",EDGE,{"disambiguationData":[OSD([sQuery(id+"F2.wireOp",EDGE,"E18.37.0.1"),sQuery(id+"F2.wireOp",EDGE,"E18.37.0.3")])]});
            var Q499;
            Q499=makeQuery(id+"F3.opExtrude","SWEPT_EDGE",EDGE,{"disambiguationData":[OSD([sQuery(id+"F2.wireOp",EDGE,"E18.16.0.0"),sQuery(id+"F2.wireOp",EDGE,"E18.16.0.3")])]});
            var Q500;
            Q500=makeQuery(id+"F3.opExtrude","SWEPT_EDGE",EDGE,{"disambiguationData":[OSD([sQuery(id+"F2.wireOp",EDGE,"E18.32.0.0"),sQuery(id+"F2.wireOp",EDGE,"E18.32.0.3")])]});
            var Q501;
            Q501=makeQuery(id+"F3.opExtrude","SWEPT_EDGE",EDGE,{"disambiguationData":[OSD([sQuery(id+"F2.wireOp",EDGE,"E18.53.0.1"),sQuery(id+"F2.wireOp",EDGE,"E18.53.0.3")])]});
            var Q502;
            Q502=makeQuery(id+"F3.opExtrude","SWEPT_EDGE",EDGE,{"disambiguationData":[OSD([sQuery(id+"F2.wireOp",EDGE,"E18.42.0.1"),sQuery(id+"F2.wireOp",EDGE,"E18.42.0.2")])]});
            var Q503;
            Q503=makeQuery(id+"F3.opExtrude","CAP_EDGE",EDGE,{"disambiguationData":[OSD([sQuery(id+"F2.wireOp",EDGE,"E18.6.0.3")])],"isStart":false});
            var Q504;
            Q504=makeQuery(id+"F3.opExtrude","CAP_EDGE",EDGE,{"disambiguationData":[OSD([sQuery(id+"F2.wireOp",EDGE,"E18.22.0.3")])],"isStart":false});
            var Q505;
            Q505=makeQuery(id+"F3.opExtrude","CAP_EDGE",EDGE,{"disambiguationData":[OSD([sQuery(id+"F2.wireOp",EDGE,"E18.38.0.3")])],"isStart":false});
            var Q506;
            Q506=makeQuery(id+"F3.opExtrude","SWEPT_EDGE",EDGE,{"disambiguationData":[OSD([sQuery(id+"F2.wireOp",EDGE,"E18.45.0.0"),sQuery(id+"F2.wireOp",EDGE,"E18.45.0.3")])]});
            var Q507;
            Q507=makeQuery(id+"F3.opExtrude","SWEPT_EDGE",EDGE,{"disambiguationData":[OSD([sQuery(id+"F2.wireOp",EDGE,"E18.17.0.1"),sQuery(id+"F2.wireOp",EDGE,"E18.17.0.3")])]});
            var Q508;
            Q508=makeQuery(id+"F3.opExtrude","SWEPT_EDGE",EDGE,{"disambiguationData":[OSD([sQuery(id+"F2.wireOp",EDGE,"E18.25.0.1"),sQuery(id+"F2.wireOp",EDGE,"E18.25.0.3")])]});
            var Q509;
            Q509=makeQuery(id+"F3.opExtrude","SWEPT_EDGE",EDGE,{"disambiguationData":[OSD([sQuery(id+"F2.wireOp",EDGE,"E18.26.0.1"),sQuery(id+"F2.wireOp",EDGE,"E18.26.0.3")])]});
            var Q510;
            Q510=makeQuery(id+"F3.opExtrude","SWEPT_EDGE",EDGE,{"disambiguationData":[OSD([sQuery(id+"F2.wireOp",EDGE,"E18.42.0.1"),sQuery(id+"F2.wireOp",EDGE,"E18.42.0.3")])]});
            var Q511;
            Q511=makeQuery(id+"F3.opExtrude","SWEPT_EDGE",EDGE,{"disambiguationData":[OSD([sQuery(id+"F2.wireOp",EDGE,"E18.50.0.1"),sQuery(id+"F2.wireOp",EDGE,"E18.50.0.3")])]});
            var Q512;
            Q512=makeQuery(id+"F3.opExtrude","SWEPT_EDGE",EDGE,{"disambiguationData":[OSD([sQuery(id+"F2.wireOp",EDGE,"E18.10.0.1"),sQuery(id+"F2.wireOp",EDGE,"E18.10.0.3")])]});
            var Q513;
            Q513=makeQuery(id+"F3.opExtrude","SWEPT_EDGE",EDGE,{"disambiguationData":[OSD([sQuery(id+"F2.wireOp",EDGE,"E18.41.0.0"),sQuery(id+"F2.wireOp",EDGE,"E18.41.0.3")])]});
            var Q514;
            Q514=makeQuery(id+"F3.opExtrude","CAP_EDGE",EDGE,{"disambiguationData":[OSD([sQuery(id+"F2.wireOp",EDGE,"E18.33.0.3")])],"isStart":false});
            var Q515;
            Q515=makeQuery(id+"F3.opExtrude","CAP_EDGE",EDGE,{"disambiguationData":[OSD([sQuery(id+"F2.wireOp",EDGE,"E18.20.0.3")])],"isStart":false});
            var Q516;
            Q516=makeQuery(id+"F3.opExtrude","SWEPT_EDGE",EDGE,{"disambiguationData":[OSD([sQuery(id+"F2.wireOp",EDGE,"E18.50.0.1"),sQuery(id+"F2.wireOp",EDGE,"E18.50.0.2")])]});
            var Q517;
            Q517=makeQuery(id+"F3.opExtrude","SWEPT_EDGE",EDGE,{"disambiguationData":[OSD([sQuery(id+"F2.wireOp",EDGE,"E18.12.0.0"),sQuery(id+"F2.wireOp",EDGE,"E18.12.0.3")])]});
            var Q518;
            Q518=makeQuery(id+"F3.opExtrude","SWEPT_EDGE",EDGE,{"disambiguationData":[OSD([sQuery(id+"F2.wireOp",EDGE,"E18.23.0.1"),sQuery(id+"F2.wireOp",EDGE,"E18.23.0.3")])]});
            var Q519;
            Q519=makeQuery(id+"F3.opExtrude","SWEPT_EDGE",EDGE,{"disambiguationData":[OSD([sQuery(id+"F2.wireOp",EDGE,"E18.10.0.1"),sQuery(id+"F2.wireOp",EDGE,"E18.10.0.2")])]});
            var Q520;
            Q520=makeQuery(id+"F3.opExtrude","SWEPT_EDGE",EDGE,{"disambiguationData":[OSD([sQuery(id+"F2.wireOp",EDGE,"E18.30.0.1"),sQuery(id+"F2.wireOp",EDGE,"E18.30.0.2")])]});
            var Q521;
            Q521=makeQuery(id+"F3.opExtrude","SWEPT_EDGE",EDGE,{"disambiguationData":[OSD([sQuery(id+"F2.wireOp",EDGE,"E18.18.0.1"),sQuery(id+"F2.wireOp",EDGE,"E18.18.0.2")])]});
            var Q522;
            Q522=makeQuery(id+"F3.opExtrude","SWEPT_EDGE",EDGE,{"disambiguationData":[OSD([sQuery(id+"F2.wireOp",EDGE,"E18.27.0.0"),sQuery(id+"F2.wireOp",EDGE,"E18.27.0.3")])]});
            var Q523;
            Q523=makeQuery(id+"F3.opExtrude","SWEPT_EDGE",EDGE,{"disambiguationData":[OSD([sQuery(id+"F2.wireOp",EDGE,"E18.54.0.0"),sQuery(id+"F2.wireOp",EDGE,"E18.54.0.3")])]});
            var Q524;
            Q524=makeQuery(id+"F3.opExtrude","SWEPT_EDGE",EDGE,{"disambiguationData":[OSD([sQuery(id+"F2.wireOp",EDGE,"E18.29.0.0"),sQuery(id+"F2.wireOp",EDGE,"E18.29.0.3")])]});
            var Q525;
            Q525=makeQuery(id+"F3.opExtrude","CAP_EDGE",EDGE,{"disambiguationData":[OSD([sQuery(id+"F2.wireOp",EDGE,"E18.30.0.3")])],"isStart":false});
            var Q526;
            Q526=makeQuery(id+"F3.opExtrude","CAP_EDGE",EDGE,{"disambiguationData":[OSD([sQuery(id+"F2.wireOp",EDGE,"E18.9.0.3")])],"isStart":false});
            var Q527;
            Q527=makeQuery(id+"F3.opExtrude","SWEPT_EDGE",EDGE,{"disambiguationData":[OSD([sQuery(id+"F2.wireOp",EDGE,"E18.57.0.1"),sQuery(id+"F2.wireOp",EDGE,"E18.57.0.3")])]});
            var Q528;
            Q528=makeQuery(id+"F3.opExtrude","CAP_EDGE",EDGE,{"disambiguationData":[OSD([sQuery(id+"F2.wireOp",EDGE,"E18.54.0.3")])],"isStart":false});
            var Q529;
            Q529=makeQuery(id+"F3.opExtrude","SWEPT_EDGE",EDGE,{"disambiguationData":[OSD([sQuery(id+"F2.wireOp",EDGE,"E18.25.0.0"),sQuery(id+"F2.wireOp",EDGE,"E18.25.0.3")])]});
            var Q530;
            Q530=makeQuery(id+"F3.opExtrude","SWEPT_EDGE",EDGE,{"disambiguationData":[OSD([sQuery(id+"F2.wireOp",EDGE,"E18.41.0.1"),sQuery(id+"F2.wireOp",EDGE,"E18.41.0.3")])]});
            var Q531;
            Q531=makeQuery(id+"F3.opExtrude","SWEPT_EDGE",EDGE,{"disambiguationData":[OSD([sQuery(id+"F2.wireOp",EDGE,"E18.44.0.0"),sQuery(id+"F2.wireOp",EDGE,"E18.44.0.3")])]});
            var Q532;
            Q532=makeQuery(id+"F3.opExtrude","SWEPT_EDGE",EDGE,{"disambiguationData":[OSD([sQuery(id+"F2.wireOp",EDGE,"E18.48.0.0"),sQuery(id+"F2.wireOp",EDGE,"E18.48.0.3")])]});
            var Q533;
            Q533=makeQuery(id+"F3.opExtrude","SWEPT_EDGE",EDGE,{"disambiguationData":[OSD([sQuery(id+"F2.wireOp",EDGE,"E18.19.0.0"),sQuery(id+"F2.wireOp",EDGE,"E18.19.0.3")])]});
            var Q534;
            Q534=makeQuery(id+"F3.opExtrude","CAP_EDGE",EDGE,{"disambiguationData":[OSD([sQuery(id+"F2.wireOp",EDGE,"E18.32.0.3")])],"isStart":false});
            var Q535;
            Q535=makeQuery(id+"F3.opExtrude","SWEPT_EDGE",EDGE,{"disambiguationData":[OSD([sQuery(id+"F2.wireOp",EDGE,"E18.52.0.0"),sQuery(id+"F2.wireOp",EDGE,"E18.52.0.3")])]});
            var Q536;
            Q536=makeQuery(id+"F3.opExtrude","SWEPT_EDGE",EDGE,{"disambiguationData":[OSD([sQuery(id+"F2.wireOp",EDGE,"E18.39.0.1"),sQuery(id+"F2.wireOp",EDGE,"E18.39.0.3")])]});
            var Q537;
            Q537=makeQuery(id+"F3.opExtrude","CAP_EDGE",EDGE,{"disambiguationData":[OSD([sQuery(id+"F2.wireOp",EDGE,"E16.bottom")])],"isStart":false});
            var Q538;
            Q538=makeQuery(id+"F3.opExtrude","CAP_EDGE",EDGE,{"disambiguationData":[OSD([sQuery(id+"F2.wireOp",EDGE,"E18.12.0.3")])],"isStart":false});
            var Q539;
            Q539=makeQuery(id+"F3.opExtrude","SWEPT_EDGE",EDGE,{"disambiguationData":[OSD([sQuery(id+"F2.wireOp",EDGE,"E18.57.0.0"),sQuery(id+"F2.wireOp",EDGE,"E18.57.0.3")])]});
            var Q540;
            Q540=makeQuery(id+"F3.opExtrude","SWEPT_EDGE",EDGE,{"disambiguationData":[OSD([sQuery(id+"F2.wireOp",EDGE,"E18.11.0.0"),sQuery(id+"F2.wireOp",EDGE,"E18.11.0.3")])]});
            var Q541;
            Q541=makeQuery(id+"F3.opExtrude","SWEPT_EDGE",EDGE,{"disambiguationData":[OSD([sQuery(id+"F2.wireOp",EDGE,"E18.19.0.1"),sQuery(id+"F2.wireOp",EDGE,"E18.19.0.3")])]});
            var Q542;
            Q542=makeQuery(id+"F3.opExtrude","SWEPT_EDGE",EDGE,{"disambiguationData":[OSD([sQuery(id+"F2.wireOp",EDGE,"E18.49.0.1"),sQuery(id+"F2.wireOp",EDGE,"E18.49.0.3")])]});
            var Q543;
            Q543=makeQuery(id+"F3.opExtrude","SWEPT_EDGE",EDGE,{"disambiguationData":[OSD([sQuery(id+"F2.wireOp",EDGE,"E18.6.0.1"),sQuery(id+"F2.wireOp",EDGE,"E18.6.0.2")])]});
            var Q544;
            Q544=makeQuery(id+"F3.opExtrude","CAP_EDGE",EDGE,{"disambiguationData":[OSD([sQuery(id+"F2.wireOp",EDGE,"E18.23.0.3")])],"isStart":false});
            var Q545;
            Q545=makeQuery(id+"F3.opExtrude","CAP_EDGE",EDGE,{"disambiguationData":[OSD([sQuery(id+"F2.wireOp",EDGE,"E18.46.0.3")])],"isStart":false});
            var Q546;
            Q546=makeQuery(id+"F3.opExtrude","CAP_EDGE",EDGE,{"disambiguationData":[OSD([sQuery(id+"F2.wireOp",EDGE,"E18.43.0.3")])],"isStart":false});
            var Q547;
            Q547=makeQuery(id+"F3.opExtrude","CAP_EDGE",EDGE,{"disambiguationData":[OSD([sQuery(id+"F2.wireOp",EDGE,"E18.5.0.3")])],"isStart":false});
            var Q548;
            {var subQ0=sQuery(id+"F0.wireOp",EDGE,"E0.top");var subQ2=sQuery(id+"F2.wireOp",EDGE,"E18.2.0.1");Q548=makeQuery(id+"F3.boolean.opBoolean","SPLIT",EDGE,{"disambiguationData":[TD([makeQuery(id+"F3.opExtrude","SWEPT_FACE",FACE,{"disambiguationData":[OSD([subQ2])]})])],"derivedFrom":makeQuery(id+"F1.opExtrude","CAP_EDGE",EDGE,{"disambiguationData":[OSD([subQ0])],"isStart":true})});}
            var Q549;
            Q549=makeQuery(id+"F3.opExtrude","SWEPT_EDGE",EDGE,{"disambiguationData":[OSD([sQuery(id+"F2.wireOp",EDGE,"E18.34.0.1"),sQuery(id+"F2.wireOp",EDGE,"E18.34.0.3")])]});
            var Q550;
            Q550=makeQuery(id+"F3.opExtrude","SWEPT_EDGE",EDGE,{"disambiguationData":[OSD([sQuery(id+"F2.wireOp",EDGE,"E18.42.0.0"),sQuery(id+"F2.wireOp",EDGE,"E18.42.0.3")])]});
            var Q551;
            Q551=makeQuery(id+"F3.opExtrude","CAP_EDGE",EDGE,{"disambiguationData":[OSD([sQuery(id+"F2.wireOp",EDGE,"E18.45.0.3")])],"isStart":false});
            var Q552;
            Q552=makeQuery(id+"F3.opExtrude","SWEPT_EDGE",EDGE,{"disambiguationData":[OSD([sQuery(id+"F2.wireOp",EDGE,"E18.29.0.1"),sQuery(id+"F2.wireOp",EDGE,"E18.29.0.3")])]});
            var Q553;
            Q553=makeQuery(id+"F3.opExtrude","SWEPT_EDGE",EDGE,{"disambiguationData":[OSD([sQuery(id+"F2.wireOp",EDGE,"E18.23.0.0"),sQuery(id+"F2.wireOp",EDGE,"E18.23.0.3")])]});
            var Q554;
            Q554=makeQuery(id+"F3.opExtrude","SWEPT_EDGE",EDGE,{"disambiguationData":[OSD([sQuery(id+"F2.wireOp",EDGE,"E18.26.0.0"),sQuery(id+"F2.wireOp",EDGE,"E18.26.0.3")])]});
            var Q555;
            Q555=makeQuery(id+"F3.opExtrude","SWEPT_EDGE",EDGE,{"disambiguationData":[OSD([sQuery(id+"F2.wireOp",EDGE,"E18.30.0.1"),sQuery(id+"F2.wireOp",EDGE,"E18.30.0.3")])]});
            var Q556;
            Q556=makeQuery(id+"F3.opExtrude","CAP_EDGE",EDGE,{"disambiguationData":[OSD([sQuery(id+"F2.wireOp",EDGE,"E18.13.0.3")])],"isStart":false});
            var Q557;
            Q557=makeQuery(id+"F3.opExtrude","CAP_EDGE",EDGE,{"disambiguationData":[OSD([sQuery(id+"F2.wireOp",EDGE,"E18.41.0.3")])],"isStart":false});
            var Q558;
            Q558=makeQuery(id+"F3.opExtrude","SWEPT_EDGE",EDGE,{"disambiguationData":[OSD([sQuery(id+"F2.wireOp",EDGE,"E18.22.0.0"),sQuery(id+"F2.wireOp",EDGE,"E18.22.0.3")])]});
            var Q559;
            Q559=makeQuery(id+"F3.opExtrude","SWEPT_EDGE",EDGE,{"disambiguationData":[OSD([sQuery(id+"F2.wireOp",EDGE,"E18.15.0.0"),sQuery(id+"F2.wireOp",EDGE,"E18.15.0.3")])]});
            var Q560;
            Q560=makeQuery(id+"F3.opExtrude","SWEPT_EDGE",EDGE,{"disambiguationData":[OSD([sQuery(id+"F2.wireOp",EDGE,"E18.22.0.1"),sQuery(id+"F2.wireOp",EDGE,"E18.22.0.2")])]});
            var Q561;
            Q561=makeQuery(id+"F3.opExtrude","SWEPT_EDGE",EDGE,{"disambiguationData":[OSD([sQuery(id+"F2.wireOp",EDGE,"E18.28.0.0"),sQuery(id+"F2.wireOp",EDGE,"E18.28.0.3")])]});
            var Q562;
            Q562=makeQuery(id+"F3.opExtrude","SWEPT_EDGE",EDGE,{"disambiguationData":[OSD([sQuery(id+"F2.wireOp",EDGE,"E18.55.0.0"),sQuery(id+"F2.wireOp",EDGE,"E18.55.0.3")])]});
            var Q563;
            Q563=makeQuery(id+"F3.opExtrude","SWEPT_EDGE",EDGE,{"disambiguationData":[OSD([sQuery(id+"F2.wireOp",EDGE,"E18.30.0.0"),sQuery(id+"F2.wireOp",EDGE,"E18.30.0.3")])]});
            var Q564;
            Q564=makeQuery(id+"F3.opExtrude","SWEPT_EDGE",EDGE,{"disambiguationData":[OSD([sQuery(id+"F2.wireOp",EDGE,"E18.46.0.1"),sQuery(id+"F2.wireOp",EDGE,"E18.46.0.2")])]});
            var Q565;
            Q565=makeQuery(id+"F3.opExtrude","SWEPT_EDGE",EDGE,{"disambiguationData":[OSD([sQuery(id+"F2.wireOp",EDGE,"E18.14.0.1"),sQuery(id+"F2.wireOp",EDGE,"E18.14.0.2")])]});
            var Q566;
            Q566=makeQuery(id+"F3.opExtrude","SWEPT_EDGE",EDGE,{"disambiguationData":[OSD([sQuery(id+"F2.wireOp",EDGE,"E18.10.0.0"),sQuery(id+"F2.wireOp",EDGE,"E18.10.0.3")])]});
            var Q567;
            Q567=makeQuery(id+"F3.opExtrude","SWEPT_EDGE",EDGE,{"disambiguationData":[OSD([sQuery(id+"F2.wireOp",EDGE,"E18.34.0.1"),sQuery(id+"F2.wireOp",EDGE,"E18.34.0.2")])]});
            var Q568;
            Q568=makeQuery(id+"F3.opExtrude","CAP_EDGE",EDGE,{"disambiguationData":[OSD([sQuery(id+"F2.wireOp",EDGE,"E18.57.0.3")])],"isStart":false});
            var Q569;
            Q569=makeQuery(id+"F3.opExtrude","CAP_EDGE",EDGE,{"disambiguationData":[OSD([sQuery(id+"F2.wireOp",EDGE,"E18.39.0.3")])],"isStart":false});
            var Q570;
            Q570=makeQuery(id+"F3.opExtrude","SWEPT_EDGE",EDGE,{"disambiguationData":[OSD([sQuery(id+"F2.wireOp",EDGE,"E18.9.0.1"),sQuery(id+"F2.wireOp",EDGE,"E18.9.0.3")])]});
            var Q571;
            Q571=makeQuery(id+"F3.opExtrude","SWEPT_EDGE",EDGE,{"disambiguationData":[OSD([sQuery(id+"F2.wireOp",EDGE,"E18.34.0.0"),sQuery(id+"F2.wireOp",EDGE,"E18.34.0.3")])]});
            var Q572;
            Q572=makeQuery(id+"F3.opExtrude","SWEPT_EDGE",EDGE,{"disambiguationData":[OSD([sQuery(id+"F2.wireOp",EDGE,"E18.48.0.1"),sQuery(id+"F2.wireOp",EDGE,"E18.48.0.3")])]});
            var Q573;
            Q573=makeQuery(id+"F3.opExtrude","CAP_EDGE",EDGE,{"disambiguationData":[OSD([sQuery(id+"F2.wireOp",EDGE,"E18.37.0.3")])],"isStart":false});
            var Q574;
            Q574=makeQuery(id+"F3.opExtrude","CAP_EDGE",EDGE,{"disambiguationData":[OSD([sQuery(id+"F2.wireOp",EDGE,"E18.52.0.3")])],"isStart":false});
            var Q575;
            Q575=makeQuery(id+"F3.opExtrude","SWEPT_EDGE",EDGE,{"disambiguationData":[OSD([sQuery(id+"F2.wireOp",EDGE,"E18.54.0.1"),sQuery(id+"F2.wireOp",EDGE,"E18.54.0.3")])]});
            var Q576;
            Q576=makeQuery(id+"F3.opExtrude","CAP_EDGE",EDGE,{"disambiguationData":[OSD([sQuery(id+"F2.wireOp",EDGE,"E18.14.0.3")])],"isStart":false});
            var Q577;
            Q577=makeQuery(id+"F3.opExtrude","SWEPT_EDGE",EDGE,{"disambiguationData":[OSD([sQuery(id+"F2.wireOp",EDGE,"E18.45.0.1"),sQuery(id+"F2.wireOp",EDGE,"E18.45.0.3")])]});
            var Q578;
            Q578=makeQuery(id+"F3.opExtrude","SWEPT_EDGE",EDGE,{"disambiguationData":[OSD([sQuery(id+"F2.wireOp",EDGE,"E18.35.0.0"),sQuery(id+"F2.wireOp",EDGE,"E18.35.0.3")])]});
            var Q579;
            Q579=makeQuery(id+"F3.opExtrude","SWEPT_EDGE",EDGE,{"disambiguationData":[OSD([sQuery(id+"F2.wireOp",EDGE,"E18.27.0.1"),sQuery(id+"F2.wireOp",EDGE,"E18.27.0.3")])]});
            var Q580;
            Q580=makeQuery(id+"F3.opExtrude","SWEPT_EDGE",EDGE,{"disambiguationData":[OSD([sQuery(id+"F2.wireOp",EDGE,"E18.33.0.0"),sQuery(id+"F2.wireOp",EDGE,"E18.33.0.3")])]});
            var Q581;
            Q581=makeQuery(id+"F3.opExtrude","SWEPT_EDGE",EDGE,{"disambiguationData":[OSD([sQuery(id+"F2.wireOp",EDGE,"E18.54.0.1"),sQuery(id+"F2.wireOp",EDGE,"E18.54.0.2")])]});
            var Q582;
            Q582=makeQuery(id+"F3.opExtrude","CAP_EDGE",EDGE,{"disambiguationData":[OSD([sQuery(id+"F2.wireOp",EDGE,"E18.50.0.3")])],"isStart":false});
            var Q583;
            Q583=makeQuery(id+"F3.opExtrude","CAP_EDGE",EDGE,{"disambiguationData":[OSD([sQuery(id+"F2.wireOp",EDGE,"E18.40.0.3")])],"isStart":false});
            var Q584;
            Q584=makeQuery(id+"F3.opExtrude","CAP_EDGE",EDGE,{"disambiguationData":[OSD([sQuery(id+"F2.wireOp",EDGE,"E18.8.0.3")])],"isStart":false});
            var Q585;
            Q585=makeQuery(id+"F3.opExtrude","CAP_EDGE",EDGE,{"disambiguationData":[OSD([sQuery(id+"F2.wireOp",EDGE,"E18.48.0.3")])],"isStart":false});
            var Q586;
            Q586=makeQuery(id+"F3.opExtrude","SWEPT_EDGE",EDGE,{"disambiguationData":[OSD([sQuery(id+"F2.wireOp",EDGE,"E18.11.0.1"),sQuery(id+"F2.wireOp",EDGE,"E18.11.0.3")])]});
            var Q587;
            Q587=makeQuery(id+"F3.opExtrude","SWEPT_EDGE",EDGE,{"disambiguationData":[OSD([sQuery(id+"F2.wireOp",EDGE,"E18.26.0.1"),sQuery(id+"F2.wireOp",EDGE,"E18.26.0.2")])]});
            var Q588;
            Q588=makeQuery(id+"F3.opExtrude","SWEPT_EDGE",EDGE,{"disambiguationData":[OSD([sQuery(id+"F2.wireOp",EDGE,"E18.51.0.0"),sQuery(id+"F2.wireOp",EDGE,"E18.51.0.3")])]});
            var Q589;
            Q589=makeQuery(id+"F3.opExtrude","SWEPT_EDGE",EDGE,{"disambiguationData":[OSD([sQuery(id+"F2.wireOp",EDGE,"E18.8.0.0"),sQuery(id+"F2.wireOp",EDGE,"E18.8.0.3")])]});
            var Q590;
            Q590=makeQuery(id+"F3.opExtrude","SWEPT_EDGE",EDGE,{"disambiguationData":[OSD([sQuery(id+"F2.wireOp",EDGE,"E18.46.0.0"),sQuery(id+"F2.wireOp",EDGE,"E18.46.0.3")])]});
            var Q591;
            Q591=makeQuery(id+"F3.opExtrude","SWEPT_EDGE",EDGE,{"disambiguationData":[OSD([sQuery(id+"F2.wireOp",EDGE,"E18.13.0.1"),sQuery(id+"F2.wireOp",EDGE,"E18.13.0.3")])]});
            var Q592;
            Q592=makeQuery(id+"F3.opExtrude","CAP_EDGE",EDGE,{"disambiguationData":[OSD([sQuery(id+"F2.wireOp",EDGE,"E18.55.0.3")])],"isStart":false});
            var Q593;
            Q593=makeQuery(id+"F3.opExtrude","CAP_EDGE",EDGE,{"disambiguationData":[OSD([sQuery(id+"F2.wireOp",EDGE,"E18.34.0.3")])],"isStart":false});
            var Q594;
            Q594=makeQuery(id+"F3.opExtrude","CAP_EDGE",EDGE,{"disambiguationData":[OSD([sQuery(id+"F2.wireOp",EDGE,"E18.16.0.3")])],"isStart":false});
            var Q595;
            Q595=makeQuery(id+"F3.opExtrude","CAP_EDGE",EDGE,{"disambiguationData":[OSD([sQuery(id+"F2.wireOp",EDGE,"E18.28.0.3")])],"isStart":false});
            var Q596;
            Q596=makeQuery(id+"F3.opExtrude","CAP_EDGE",EDGE,{"disambiguationData":[OSD([sQuery(id+"F2.wireOp",EDGE,"E18.1.0.3")])],"isStart":false});
            var Q597;
            Q597=makeQuery(id+"F3.opExtrude","SWEPT_EDGE",EDGE,{"disambiguationData":[OSD([sQuery(id+"F2.wireOp",EDGE,"E18.22.0.1"),sQuery(id+"F2.wireOp",EDGE,"E18.22.0.3")])]});
            var Q598;
            Q598=makeQuery(id+"F3.opExtrude","SWEPT_EDGE",EDGE,{"disambiguationData":[OSD([sQuery(id+"F2.wireOp",EDGE,"E18.38.0.1"),sQuery(id+"F2.wireOp",EDGE,"E18.38.0.2")])]});
            var Q599;
            Q599=makeQuery(id+"F3.opExtrude","SWEPT_EDGE",EDGE,{"disambiguationData":[OSD([sQuery(id+"F2.wireOp",EDGE,"E18.49.0.0"),sQuery(id+"F2.wireOp",EDGE,"E18.49.0.3")])]});
            var Q600;
            Q600=makeQuery(id+"F3.opExtrude","SWEPT_EDGE",EDGE,{"disambiguationData":[OSD([sQuery(id+"F2.wireOp",EDGE,"E18.21.0.1"),sQuery(id+"F2.wireOp",EDGE,"E18.21.0.3")])]});
            var Q601;
            Q601=makeQuery(id+"F3.opExtrude","CAP_EDGE",EDGE,{"disambiguationData":[OSD([sQuery(id+"F2.wireOp",EDGE,"E18.44.0.3")])],"isStart":false});
            var Q602;
            Q602=makeQuery(id+"F3.opExtrude","SWEPT_EDGE",EDGE,{"disambiguationData":[OSD([sQuery(id+"F2.wireOp",EDGE,"E18.18.0.0"),sQuery(id+"F2.wireOp",EDGE,"E18.18.0.3")])]});
            var Q603;
            Q603=makeQuery(id+"F3.opExtrude","SWEPT_EDGE",EDGE,{"disambiguationData":[OSD([sQuery(id+"F2.wireOp",EDGE,"E18.17.0.0"),sQuery(id+"F2.wireOp",EDGE,"E18.17.0.3")])]});
            var Q604;
            Q604=makeQuery(id+"F3.opExtrude","SWEPT_EDGE",EDGE,{"disambiguationData":[OSD([sQuery(id+"F2.wireOp",EDGE,"E18.58.0.1"),sQuery(id+"F2.wireOp",EDGE,"E18.58.0.2")])]});
            var Q605;
            Q605=makeQuery(id+"F3.opExtrude","SWEPT_EDGE",EDGE,{"disambiguationData":[OSD([sQuery(id+"F2.wireOp",EDGE,"E18.38.0.1"),sQuery(id+"F2.wireOp",EDGE,"E18.38.0.3")])]});
            var Q606;
            Q606=makeQuery(id+"F3.opExtrude","SWEPT_EDGE",EDGE,{"disambiguationData":[OSD([sQuery(id+"F2.wireOp",EDGE,"E18.14.0.0"),sQuery(id+"F2.wireOp",EDGE,"E18.14.0.3")])]});
            var Q607;
            Q607=makeQuery(id+"F3.opExtrude","SWEPT_EDGE",EDGE,{"disambiguationData":[OSD([sQuery(id+"F2.wireOp",EDGE,"E18.46.0.1"),sQuery(id+"F2.wireOp",EDGE,"E18.46.0.3")])]});
            var Q608;
            Q608=makeQuery(id+"F3.opExtrude","SWEPT_EDGE",EDGE,{"disambiguationData":[OSD([sQuery(id+"F2.wireOp",EDGE,"E18.33.0.1"),sQuery(id+"F2.wireOp",EDGE,"E18.33.0.3")])]});
            var Q609;
            Q609=makeQuery(id+"F3.opExtrude","SWEPT_EDGE",EDGE,{"disambiguationData":[OSD([sQuery(id+"F2.wireOp",EDGE,"E18.21.0.0"),sQuery(id+"F2.wireOp",EDGE,"E18.21.0.3")])]});
            var Q610;
            Q610=makeQuery(id+"F3.opExtrude","SWEPT_EDGE",EDGE,{"disambiguationData":[OSD([sQuery(id+"F2.wireOp",EDGE,"E18.14.0.1"),sQuery(id+"F2.wireOp",EDGE,"E18.14.0.3")])]});
            var Q611;
            Q611=makeQuery(id+"F3.opExtrude","CAP_EDGE",EDGE,{"disambiguationData":[OSD([sQuery(id+"F2.wireOp",EDGE,"E18.17.0.3")])],"isStart":false});
            var Q612;
            Q612=makeQuery(id+"F3.opExtrude","CAP_EDGE",EDGE,{"disambiguationData":[OSD([sQuery(id+"F2.wireOp",EDGE,"E18.36.0.3")])],"isStart":false});
            var Q613;
            Q613=makeQuery(id+"F3.opExtrude","SWEPT_EDGE",EDGE,{"disambiguationData":[OSD([sQuery(id+"F2.wireOp",EDGE,"E18.58.0.0"),sQuery(id+"F2.wireOp",EDGE,"E18.58.0.3")])]});
            var Q614;
            Q614=makeQuery(id+"F3.opExtrude","SWEPT_EDGE",EDGE,{"disambiguationData":[OSD([sQuery(id+"F2.wireOp",EDGE,"E18.37.0.0"),sQuery(id+"F2.wireOp",EDGE,"E18.37.0.3")])]});
            var Q615;
            Q615=makeQuery(id+"F3.opExtrude","SWEPT_EDGE",EDGE,{"disambiguationData":[OSD([sQuery(id+"F2.wireOp",EDGE,"E18.50.0.0"),sQuery(id+"F2.wireOp",EDGE,"E18.50.0.3")])]});
            var Q616;
            Q616=makeQuery(id+"F3.opExtrude","SWEPT_EDGE",EDGE,{"disambiguationData":[OSD([sQuery(id+"F2.wireOp",EDGE,"E18.12.0.1"),sQuery(id+"F2.wireOp",EDGE,"E18.12.0.3")])]});
            var Q617;
            Q617=makeQuery(id+"F3.opExtrude","SWEPT_EDGE",EDGE,{"disambiguationData":[OSD([sQuery(id+"F2.wireOp",EDGE,"E18.53.0.0"),sQuery(id+"F2.wireOp",EDGE,"E18.53.0.3")])]});
            var Q618;
            Q618=makeQuery(id+"F3.opExtrude","SWEPT_EDGE",EDGE,{"disambiguationData":[OSD([sQuery(id+"F2.wireOp",EDGE,"E18.47.0.0"),sQuery(id+"F2.wireOp",EDGE,"E18.47.0.3")])]});
            var Q619;
            Q619=makeQuery(id+"F3.opExtrude","SWEPT_EDGE",EDGE,{"disambiguationData":[OSD([sQuery(id+"F2.wireOp",EDGE,"E18.39.0.0"),sQuery(id+"F2.wireOp",EDGE,"E18.39.0.3")])]});
            var Q620;
            Q620=makeQuery(id+"F3.opExtrude","SWEPT_EDGE",EDGE,{"disambiguationData":[OSD([sQuery(id+"F2.wireOp",EDGE,"E18.31.0.0"),sQuery(id+"F2.wireOp",EDGE,"E18.31.0.3")])]});
            var Q621;
            Q621=makeQuery(id+"F3.opExtrude","CAP_EDGE",EDGE,{"disambiguationData":[OSD([sQuery(id+"F2.wireOp",EDGE,"E18.56.0.3")])],"isStart":false});
            var Q622;
            Q622=makeQuery(id+"F3.opExtrude","CAP_EDGE",EDGE,{"disambiguationData":[OSD([sQuery(id+"F2.wireOp",EDGE,"E18.24.0.3")])],"isStart":false});
            var Q623;
            Q623=makeQuery(id+"F3.opExtrude","SWEPT_EDGE",EDGE,{"disambiguationData":[OSD([sQuery(id+"F2.wireOp",EDGE,"E18.15.0.1"),sQuery(id+"F2.wireOp",EDGE,"E18.15.0.3")])]});
            var Q624;
            Q624=makeQuery(id+"F3.opExtrude","CAP_EDGE",EDGE,{"disambiguationData":[OSD([sQuery(id+"F2.wireOp",EDGE,"E18.19.0.3")])],"isStart":false});
            var Q625;
            Q625=makeQuery(id+"F3.opExtrude","SWEPT_EDGE",EDGE,{"disambiguationData":[OSD([sQuery(id+"F2.wireOp",EDGE,"E18.20.0.1"),sQuery(id+"F2.wireOp",EDGE,"E18.20.0.3")])]});
            var Q626;
            Q626=makeQuery(id+"F3.opExtrude","SWEPT_EDGE",EDGE,{"disambiguationData":[OSD([sQuery(id+"F2.wireOp",EDGE,"E18.51.0.1"),sQuery(id+"F2.wireOp",EDGE,"E18.51.0.3")])]});
            var Q627;
            Q627=makeQuery(id+"F3.opExtrude","SWEPT_EDGE",EDGE,{"disambiguationData":[OSD([sQuery(id+"F2.wireOp",EDGE,"E18.20.0.0"),sQuery(id+"F2.wireOp",EDGE,"E18.20.0.3")])]});
            var Q628;
            Q628=makeQuery(id+"F3.opExtrude","SWEPT_EDGE",EDGE,{"disambiguationData":[OSD([sQuery(id+"F2.wireOp",EDGE,"E18.43.0.1"),sQuery(id+"F2.wireOp",EDGE,"E18.43.0.3")])]});
            var Q629;
            Q629=makeQuery(id+"F3.opExtrude","SWEPT_EDGE",EDGE,{"disambiguationData":[OSD([sQuery(id+"F2.wireOp",EDGE,"E18.52.0.1"),sQuery(id+"F2.wireOp",EDGE,"E18.52.0.3")])]});
            var Q630;
            Q630=makeQuery(id+"F3.opExtrude","CAP_EDGE",EDGE,{"disambiguationData":[OSD([sQuery(id+"F2.wireOp",EDGE,"E18.29.0.3")])],"isStart":false});
            var Q631;
            Q631=makeQuery(id+"F3.opExtrude","SWEPT_EDGE",EDGE,{"disambiguationData":[OSD([sQuery(id+"F2.wireOp",EDGE,"E18.28.0.1"),sQuery(id+"F2.wireOp",EDGE,"E18.28.0.3")])]});
            var Q632;
            Q632=makeQuery(id+"F3.opExtrude","SWEPT_EDGE",EDGE,{"disambiguationData":[OSD([sQuery(id+"F2.wireOp",EDGE,"E18.36.0.0"),sQuery(id+"F2.wireOp",EDGE,"E18.36.0.3")])]});
            var Q633;
            Q633=makeQuery(id+"F3.opExtrude","CAP_EDGE",EDGE,{"disambiguationData":[OSD([sQuery(id+"F2.wireOp",EDGE,"E18.49.0.3")])],"isStart":false});
            var Q634;
            Q634=makeQuery(id+"F3.opExtrude","SWEPT_EDGE",EDGE,{"disambiguationData":[OSD([sQuery(id+"F2.wireOp",EDGE,"E18.18.0.1"),sQuery(id+"F2.wireOp",EDGE,"E18.18.0.3")])]});
            var Q635;
            Q635=makeQuery(id+"F3.opExtrude","SWEPT_EDGE",EDGE,{"disambiguationData":[OSD([sQuery(id+"F2.wireOp",EDGE,"E18.13.0.0"),sQuery(id+"F2.wireOp",EDGE,"E18.13.0.3")])]});
            var Q636;
            Q636=makeQuery(id+"F3.opExtrude","CAP_EDGE",EDGE,{"disambiguationData":[OSD([sQuery(id+"F2.wireOp",EDGE,"E18.3.0.3")])],"isStart":false});
            var Q637;
            Q637=makeQuery(id+"F3.opExtrude","CAP_EDGE",EDGE,{"disambiguationData":[OSD([sQuery(id+"F2.wireOp",EDGE,"E18.18.0.3")])],"isStart":false});
            var Q638;
            Q638=makeQuery(id+"F3.opExtrude","CAP_EDGE",EDGE,{"disambiguationData":[OSD([sQuery(id+"F2.wireOp",EDGE,"E18.2.0.3")])],"isStart":false});
            var Q639;
            Q639=makeQuery(id+"F3.opExtrude","SWEPT_EDGE",EDGE,{"disambiguationData":[OSD([sQuery(id+"F2.wireOp",EDGE,"E18.47.0.1"),sQuery(id+"F2.wireOp",EDGE,"E18.47.0.3")])]});
            var Q640;
            Q640=makeQuery(id+"F3.opExtrude","SWEPT_EDGE",EDGE,{"disambiguationData":[OSD([sQuery(id+"F2.wireOp",EDGE,"E18.35.0.1"),sQuery(id+"F2.wireOp",EDGE,"E18.35.0.3")])]});
            var Q641;
            Q641=makeQuery(id+"F3.opExtrude","CAP_EDGE",EDGE,{"disambiguationData":[OSD([sQuery(id+"F2.wireOp",EDGE,"E18.4.0.3")])],"isStart":false});
            var Q642;
            Q642=makeQuery(id+"F3.opExtrude","SWEPT_EDGE",EDGE,{"disambiguationData":[OSD([sQuery(id+"F2.wireOp",EDGE,"E18.44.0.1"),sQuery(id+"F2.wireOp",EDGE,"E18.44.0.3")])]});
            var Q643;
            Q643=makeQuery(id+"F3.opExtrude","SWEPT_EDGE",EDGE,{"disambiguationData":[OSD([sQuery(id+"F2.wireOp",EDGE,"E18.38.0.0"),sQuery(id+"F2.wireOp",EDGE,"E18.38.0.3")])]});
            var Q644;
            Q644=makeQuery(id+"F3.opExtrude","CAP_EDGE",EDGE,{"disambiguationData":[OSD([sQuery(id+"F2.wireOp",EDGE,"E18.15.0.3")])],"isStart":false});
            var Q645;
            Q645=makeQuery(id+"F3.opExtrude","SWEPT_EDGE",EDGE,{"disambiguationData":[OSD([sQuery(id+"F2.wireOp",EDGE,"E18.36.0.1"),sQuery(id+"F2.wireOp",EDGE,"E18.36.0.3")])]});
            var Q646;
            Q646=makeQuery(id+"F3.opExtrude","SWEPT_EDGE",EDGE,{"disambiguationData":[OSD([sQuery(id+"F2.wireOp",EDGE,"E18.58.0.1"),sQuery(id+"F2.wireOp",EDGE,"E18.58.0.3")])]});
            var Q647;
            Q647=makeQuery(id+"F3.opExtrude","SWEPT_EDGE",EDGE,{"disambiguationData":[OSD([sQuery(id+"F2.wireOp",EDGE,"E18.43.0.0"),sQuery(id+"F2.wireOp",EDGE,"E18.43.0.3")])]});
            var Q648;
            {var subQ0=sQuery(id+"F0.wireOp",EDGE,"E0.top");Q648=makeQuery(id+"F4.opChamfer","BLEND_EDGE",EDGE,{"blendedFrom":[makeQuery(id+"F1.opExtrude","CAP_EDGE",EDGE,{"disambiguationData":[OSD([subQ0])],"isStart":false}),makeQuery(id+"F1.opExtrude","CAP_FACE",FACE,{"disambiguationData":[OSD([sQuery(id+"F0.wireOp",EDGE,"E0.bottom"),subQ0,sQuery(id+"F0.wireOp",EDGE,"E1"),sQuery(id+"F0.wireOp",EDGE,"E2"),sQuery(id+"F0.wireOp",EDGE,"E3"),sQuery(id+"F0.wireOp",EDGE,"E6"),sQuery(id+"F0.wireOp",EDGE,"E7"),sQuery(id+"F0.wireOp",EDGE,"E8.filletArc"),sQuery(id+"F0.wireOp",EDGE,"E10.MirrorCS"),sQuery(id+"F0.wireOp",EDGE,"E11.MirrorCS"),sQuery(id+"F0.wireOp",EDGE,"E12.MirrorCS"),sQuery(id+"F0.wireOp",EDGE,"E13.MirrorCS"),sQuery(id+"F0.wireOp",EDGE,"E14.MirrorCS"),sQuery(id+"F0.wireOp",EDGE,"E15.MirrorCS")])],"isStart":false})],"blendedInto":[makeQuery(id+"F1.opExtrude","CAP_FACE",FACE,{"disambiguationData":[OSD([sQuery(id+"F0.wireOp",EDGE,"E0.bottom"),subQ0,sQuery(id+"F0.wireOp",EDGE,"E1"),sQuery(id+"F0.wireOp",EDGE,"E2"),sQuery(id+"F0.wireOp",EDGE,"E3"),sQuery(id+"F0.wireOp",EDGE,"E6"),sQuery(id+"F0.wireOp",EDGE,"E7"),sQuery(id+"F0.wireOp",EDGE,"E8.filletArc"),sQuery(id+"F0.wireOp",EDGE,"E10.MirrorCS"),sQuery(id+"F0.wireOp",EDGE,"E11.MirrorCS"),sQuery(id+"F0.wireOp",EDGE,"E12.MirrorCS"),sQuery(id+"F0.wireOp",EDGE,"E13.MirrorCS"),sQuery(id+"F0.wireOp",EDGE,"E14.MirrorCS"),sQuery(id+"F0.wireOp",EDGE,"E15.MirrorCS")])],"isStart":false})]});}
            var Q649;
            {var subQ0=sQuery(id+"F0.wireOp",EDGE,"E0.top");Q649=makeQuery(id+"F4.opChamfer","BLEND_EDGE",EDGE,{"blendedFrom":[makeQuery(id+"F1.opExtrude","CAP_EDGE",EDGE,{"disambiguationData":[OSD([subQ0])],"isStart":false}),makeQuery(id+"F1.opExtrude","SWEPT_FACE",FACE,{"disambiguationData":[OSD([subQ0])]})],"blendedInto":[makeQuery(id+"F1.opExtrude","SWEPT_FACE",FACE,{"disambiguationData":[OSD([subQ0])]})]});}
            var Q650;
            Q650=makeQuery(id+"F3.opExtrude","CAP_EDGE",EDGE,{"disambiguationData":[OSD([sQuery(id+"F2.wireOp",EDGE,"E18.11.0.3")])],"isStart":false});
            var Q651;
            Q651=makeQuery(id+"F3.opExtrude","CAP_EDGE",EDGE,{"disambiguationData":[OSD([sQuery(id+"F2.wireOp",EDGE,"E18.3.0.2")])],"isStart":false});
            var Q652;
            Q652=makeQuery(id+"F3.opExtrude","CAP_EDGE",EDGE,{"disambiguationData":[OSD([sQuery(id+"F2.wireOp",EDGE,"E18.1.0.2")])],"isStart":false});
            var Q653;
            Q653=makeQuery(id+"F3.opExtrude","CAP_EDGE",EDGE,{"disambiguationData":[OSD([sQuery(id+"F2.wireOp",EDGE,"E17")])],"isStart":false});
            var Q654;
            Q654=makeQuery(id+"F3.opExtrude","CAP_EDGE",EDGE,{"disambiguationData":[OSD([sQuery(id+"F2.wireOp",EDGE,"E18.56.0.2")])],"isStart":false});
            var Q655;
            Q655=makeQuery(id+"F3.opExtrude","CAP_EDGE",EDGE,{"disambiguationData":[OSD([sQuery(id+"F2.wireOp",EDGE,"E18.58.0.2")])],"isStart":false});
            var Q656;
            Q656=makeQuery(id+"F3.opExtrude","CAP_EDGE",EDGE,{"disambiguationData":[OSD([sQuery(id+"F2.wireOp",EDGE,"E18.54.0.2")])],"isStart":false});
            var Q657;
            Q657=makeQuery(id+"F3.opExtrude","CAP_EDGE",EDGE,{"disambiguationData":[OSD([sQuery(id+"F2.wireOp",EDGE,"E18.50.0.2")])],"isStart":false});
            var Q658;
            Q658=makeQuery(id+"F3.opExtrude","CAP_EDGE",EDGE,{"disambiguationData":[OSD([sQuery(id+"F2.wireOp",EDGE,"E18.48.0.2")])],"isStart":false});
            var Q659;
            Q659=makeQuery(id+"F3.opExtrude","CAP_EDGE",EDGE,{"disambiguationData":[OSD([sQuery(id+"F2.wireOp",EDGE,"E18.46.0.2")])],"isStart":false});
            var Q660;
            Q660=makeQuery(id+"F3.opExtrude","CAP_EDGE",EDGE,{"disambiguationData":[OSD([sQuery(id+"F2.wireOp",EDGE,"E18.44.0.2")])],"isStart":false});
            var Q661;
            Q661=makeQuery(id+"F3.opExtrude","CAP_EDGE",EDGE,{"disambiguationData":[OSD([sQuery(id+"F2.wireOp",EDGE,"E18.40.0.2")])],"isStart":false});
            var Q662;
            Q662=makeQuery(id+"F3.opExtrude","CAP_EDGE",EDGE,{"disambiguationData":[OSD([sQuery(id+"F2.wireOp",EDGE,"E18.38.0.2")])],"isStart":false});
            var Q663;
            Q663=makeQuery(id+"F3.opExtrude","CAP_EDGE",EDGE,{"disambiguationData":[OSD([sQuery(id+"F2.wireOp",EDGE,"E18.36.0.2")])],"isStart":false});
            var Q664;
            Q664=makeQuery(id+"F3.opExtrude","CAP_EDGE",EDGE,{"disambiguationData":[OSD([sQuery(id+"F2.wireOp",EDGE,"E18.32.0.2")])],"isStart":false});
            var Q665;
            Q665=makeQuery(id+"F3.opExtrude","CAP_EDGE",EDGE,{"disambiguationData":[OSD([sQuery(id+"F2.wireOp",EDGE,"E18.30.0.2")])],"isStart":false});
            var Q666;
            Q666=makeQuery(id+"F3.opExtrude","CAP_EDGE",EDGE,{"disambiguationData":[OSD([sQuery(id+"F2.wireOp",EDGE,"E18.28.0.2")])],"isStart":false});
            var Q667;
            Q667=makeQuery(id+"F3.opExtrude","CAP_EDGE",EDGE,{"disambiguationData":[OSD([sQuery(id+"F2.wireOp",EDGE,"E18.26.0.2")])],"isStart":false});
            var Q668;
            Q668=makeQuery(id+"F3.opExtrude","CAP_EDGE",EDGE,{"disambiguationData":[OSD([sQuery(id+"F2.wireOp",EDGE,"E18.24.0.2")])],"isStart":false});
            var Q669;
            Q669=makeQuery(id+"F3.opExtrude","CAP_EDGE",EDGE,{"disambiguationData":[OSD([sQuery(id+"F2.wireOp",EDGE,"E18.22.0.2")])],"isStart":false});
            var Q670;
            Q670=makeQuery(id+"F3.opExtrude","CAP_EDGE",EDGE,{"disambiguationData":[OSD([sQuery(id+"F2.wireOp",EDGE,"E18.20.0.2")])],"isStart":false});
            var Q671;
            Q671=makeQuery(id+"F3.opExtrude","CAP_EDGE",EDGE,{"disambiguationData":[OSD([sQuery(id+"F2.wireOp",EDGE,"E18.18.0.2")])],"isStart":false});
            var Q672;
            Q672=makeQuery(id+"F3.opExtrude","CAP_EDGE",EDGE,{"disambiguationData":[OSD([sQuery(id+"F2.wireOp",EDGE,"E18.16.0.2")])],"isStart":false});
            var Q673;
            Q673=makeQuery(id+"F3.opExtrude","CAP_EDGE",EDGE,{"disambiguationData":[OSD([sQuery(id+"F2.wireOp",EDGE,"E18.14.0.2")])],"isStart":false});
            var Q674;
            Q674=makeQuery(id+"F3.opExtrude","CAP_EDGE",EDGE,{"disambiguationData":[OSD([sQuery(id+"F2.wireOp",EDGE,"E18.12.0.2")])],"isStart":false});
            var Q675;
            Q675=makeQuery(id+"F3.opExtrude","CAP_EDGE",EDGE,{"disambiguationData":[OSD([sQuery(id+"F2.wireOp",EDGE,"E18.10.0.2")])],"isStart":false});
            var Q676;
            Q676=makeQuery(id+"F3.opExtrude","CAP_EDGE",EDGE,{"disambiguationData":[OSD([sQuery(id+"F2.wireOp",EDGE,"E18.8.0.2")])],"isStart":false});
            var Q677;
            Q677=makeQuery(id+"F3.opExtrude","CAP_EDGE",EDGE,{"disambiguationData":[OSD([sQuery(id+"F2.wireOp",EDGE,"E18.6.0.2")])],"isStart":false});
            var Q678;
            Q678=makeQuery(id+"F3.opExtrude","CAP_EDGE",EDGE,{"disambiguationData":[OSD([sQuery(id+"F2.wireOp",EDGE,"E18.4.0.2")])],"isStart":false});
            var Q679;
            Q679=makeQuery(id+"F3.opExtrude","CAP_EDGE",EDGE,{"disambiguationData":[OSD([sQuery(id+"F2.wireOp",EDGE,"E18.2.0.2")])],"isStart":false});
            var Q680;
            Q680=makeQuery(id+"F3.opExtrude","CAP_EDGE",EDGE,{"disambiguationData":[OSD([sQuery(id+"F2.wireOp",EDGE,"E18.37.0.2")])],"isStart":false});
            var Q681;
            Q681=makeQuery(id+"F3.opExtrude","CAP_EDGE",EDGE,{"disambiguationData":[OSD([sQuery(id+"F2.wireOp",EDGE,"E18.35.0.2")])],"isStart":false});
            var Q682;
            Q682=makeQuery(id+"F3.opExtrude","CAP_EDGE",EDGE,{"disambiguationData":[OSD([sQuery(id+"F2.wireOp",EDGE,"E18.33.0.2")])],"isStart":false});
            var Q683;
            Q683=makeQuery(id+"F3.opExtrude","CAP_EDGE",EDGE,{"disambiguationData":[OSD([sQuery(id+"F2.wireOp",EDGE,"E18.31.0.2")])],"isStart":false});
            var Q684;
            Q684=makeQuery(id+"F3.opExtrude","CAP_EDGE",EDGE,{"disambiguationData":[OSD([sQuery(id+"F2.wireOp",EDGE,"E18.29.0.2")])],"isStart":false});
            var Q685;
            Q685=makeQuery(id+"F3.opExtrude","CAP_EDGE",EDGE,{"disambiguationData":[OSD([sQuery(id+"F2.wireOp",EDGE,"E18.27.0.2")])],"isStart":false});
            var Q686;
            Q686=makeQuery(id+"F3.opExtrude","CAP_EDGE",EDGE,{"disambiguationData":[OSD([sQuery(id+"F2.wireOp",EDGE,"E18.23.0.2")])],"isStart":false});
            var Q687;
            Q687=makeQuery(id+"F3.opExtrude","CAP_EDGE",EDGE,{"disambiguationData":[OSD([sQuery(id+"F2.wireOp",EDGE,"E18.21.0.2")])],"isStart":false});
            var Q688;
            Q688=makeQuery(id+"F3.opExtrude","CAP_EDGE",EDGE,{"disambiguationData":[OSD([sQuery(id+"F2.wireOp",EDGE,"E18.19.0.2")])],"isStart":false});
            var Q689;
            Q689=makeQuery(id+"F3.opExtrude","CAP_EDGE",EDGE,{"disambiguationData":[OSD([sQuery(id+"F2.wireOp",EDGE,"E18.17.0.2")])],"isStart":false});
            var Q690;
            Q690=makeQuery(id+"F3.opExtrude","CAP_EDGE",EDGE,{"disambiguationData":[OSD([sQuery(id+"F2.wireOp",EDGE,"E18.13.0.2")])],"isStart":false});
            var Q691;
            Q691=makeQuery(id+"F3.opExtrude","CAP_EDGE",EDGE,{"disambiguationData":[OSD([sQuery(id+"F2.wireOp",EDGE,"E18.11.0.2")])],"isStart":false});
            var Q692;
            Q692=makeQuery(id+"F3.opExtrude","CAP_EDGE",EDGE,{"disambiguationData":[OSD([sQuery(id+"F2.wireOp",EDGE,"E18.9.0.2")])],"isStart":false});
            var Q693;
            Q693=makeQuery(id+"F3.opExtrude","CAP_EDGE",EDGE,{"disambiguationData":[OSD([sQuery(id+"F2.wireOp",EDGE,"E18.7.0.2")])],"isStart":false});
            var Q694;
            Q694=makeQuery(id+"F3.opExtrude","CAP_EDGE",EDGE,{"disambiguationData":[OSD([sQuery(id+"F2.wireOp",EDGE,"E18.5.0.2")])],"isStart":false});
            var Q695;
            Q695=makeQuery(id+"F3.opExtrude","CAP_EDGE",EDGE,{"disambiguationData":[OSD([sQuery(id+"F2.wireOp",EDGE,"E18.47.0.2")])],"isStart":false});
            var Q696;
            Q696=makeQuery(id+"F3.opExtrude","CAP_EDGE",EDGE,{"disambiguationData":[OSD([sQuery(id+"F2.wireOp",EDGE,"E18.43.0.2")])],"isStart":false});
            var Q697;
            Q697=makeQuery(id+"F3.opExtrude","CAP_EDGE",EDGE,{"disambiguationData":[OSD([sQuery(id+"F2.wireOp",EDGE,"E18.55.0.2")])],"isStart":false});
            var Q698;
            Q698=makeQuery(id+"F3.opExtrude","CAP_EDGE",EDGE,{"disambiguationData":[OSD([sQuery(id+"F2.wireOp",EDGE,"E18.31.0.3")])],"isStart":false});
            var Q699;
            Q699=makeQuery(id+"F3.opExtrude","CAP_EDGE",EDGE,{"disambiguationData":[OSD([sQuery(id+"F2.wireOp",EDGE,"E18.41.0.2")])],"isStart":false});
            var Q700;
            Q700=makeQuery(id+"F3.opExtrude","CAP_EDGE",EDGE,{"disambiguationData":[OSD([sQuery(id+"F2.wireOp",EDGE,"E18.51.0.2")])],"isStart":false});
            var Q701;
            Q701=makeQuery(id+"F3.opExtrude","CAP_EDGE",EDGE,{"disambiguationData":[OSD([sQuery(id+"F2.wireOp",EDGE,"E18.49.0.2")])],"isStart":false});
            var Q702;
            Q702=makeQuery(id+"F3.opExtrude","CAP_EDGE",EDGE,{"disambiguationData":[OSD([sQuery(id+"F2.wireOp",EDGE,"E18.57.0.2")])],"isStart":false});
            var Q703;
            Q703=makeQuery(id+"F3.opExtrude","CAP_EDGE",EDGE,{"disambiguationData":[OSD([sQuery(id+"F2.wireOp",EDGE,"E18.47.0.3")])],"isStart":false});
            var Q704;
            Q704=makeQuery(id+"F3.opExtrude","CAP_EDGE",EDGE,{"disambiguationData":[OSD([sQuery(id+"F2.wireOp",EDGE,"E18.39.0.2")])],"isStart":false});
            var Q705;
            Q705=makeQuery(id+"F3.opExtrude","CAP_EDGE",EDGE,{"disambiguationData":[OSD([sQuery(id+"F2.wireOp",EDGE,"E18.53.0.2")])],"isStart":false});
            var Q706;
            Q706=makeQuery(id+"F3.opExtrude","CAP_EDGE",EDGE,{"disambiguationData":[OSD([sQuery(id+"F2.wireOp",EDGE,"E18.45.0.2")])],"isStart":false});
            var Q707;
            Q707=makeQuery(id+"F3.opExtrude","CAP_EDGE",EDGE,{"disambiguationData":[OSD([sQuery(id+"F2.wireOp",EDGE,"E18.7.0.3")])],"isStart":false});
            var Q708;
            Q708=makeQuery(id+"F3.opExtrude","CAP_EDGE",EDGE,{"disambiguationData":[OSD([sQuery(id+"F2.wireOp",EDGE,"E18.27.0.3")])],"isStart":false});
            var Q709;
            Q709=makeQuery(id+"F3.opExtrude","CAP_EDGE",EDGE,{"disambiguationData":[OSD([sQuery(id+"F2.wireOp",EDGE,"E18.51.0.3")])],"isStart":false});
            var Q710;
            Q710=makeQuery(id+"F3.opExtrude","CAP_EDGE",EDGE,{"disambiguationData":[OSD([sQuery(id+"F2.wireOp",EDGE,"E18.35.0.3")])],"isStart":false});
            chamfer(context, id + "F6", {"entities" : qUnion([Q0, Q1, Q2, Q3, Q4, Q5, Q6, Q7, Q8, Q9, Q10, Q11, Q12, Q13, Q14, Q15, Q16, Q17, Q18, Q19, Q20, Q21, Q22, Q23, Q24, Q25, Q26, Q27, Q28, Q29, Q30, Q31, Q32, Q33, Q34, Q35, Q36, Q37, Q38, Q39, Q40, Q41, Q42, Q43, Q44, Q45, Q46, Q47, Q48, Q49, Q50, Q51, Q52, Q53, Q54, Q55, Q56, Q57, Q58, Q59, Q60, Q61, Q62, Q63, Q64, Q65, Q66, Q67, Q68, Q69, Q70, Q71, Q72, Q73, Q74, Q75, Q76, Q77, Q78, Q79, Q80, Q81, Q82, Q83, Q84, Q85, Q86, Q87, Q88, Q89, Q90, Q91, Q92, Q93, Q94, Q95, Q96, Q97, Q98, Q99, Q100, Q101, Q102, Q103, Q104, Q105, Q106, Q107, Q108, Q109, Q110, Q111, Q112, Q113, Q114, Q115, Q116, Q117, Q118, Q119, Q120, Q121, Q122, Q123, Q124, Q125, Q126, Q127, Q128, Q129, Q130, Q131, Q132, Q133, Q134, Q135, Q136, Q137, Q138, Q139, Q140, Q141, Q142, Q143, Q144, Q145, Q146, Q147, Q148, Q149, Q150, Q151, Q152, Q153, Q154, Q155, Q156, Q157, Q158, Q159, Q160, Q161, Q162, Q163, Q164, Q165, Q166, Q167, Q168, Q169, Q170, Q171, Q172, Q173, Q174, Q175, Q176, Q177, Q178, Q179, Q180, Q181, Q182, Q183, Q184, Q185, Q186, Q187, Q188, Q189, Q190, Q191, Q192, Q193, Q194, Q195, Q196, Q197, Q198, Q199, Q200, Q201, Q202, Q203, Q204, Q205, Q206, Q207, Q208, Q209, Q210, Q211, Q212, Q213, Q214, Q215, Q216, Q217, Q218, Q219, Q220, Q221, Q222, Q223, Q224, Q225, Q226, Q227, Q228, Q229, Q230, Q231, Q232, Q233, Q234, Q235, Q236, Q237, Q238, Q239, Q240, Q241, Q242, Q243, Q244, Q245, Q246, Q247, Q248, Q249, Q250, Q251, Q252, Q253, Q254, Q255, Q256, Q257, Q258, Q259, Q260, Q261, Q262, Q263, Q264, Q265, Q266, Q267, Q268, Q269, Q270, Q271, Q272, Q273, Q274, Q275, Q276, Q277, Q278, Q279, Q280, Q281, Q282, Q283, Q284, Q285, Q286, Q287, Q288, Q289, Q290, Q291, Q292, Q293, Q294, Q295, Q296, Q297, Q298, Q299, Q300, Q301, Q302, Q303, Q304, Q305, Q306, Q307, Q308, Q309, Q310, Q311, Q312, Q313, Q314, Q315, Q316, Q317, Q318, Q319, Q320, Q321, Q322, Q323, Q324, Q325, Q326, Q327, Q328, Q329, Q330, Q331, Q332, Q333, Q334, Q335, Q336, Q337, Q338, Q339, Q340, Q341, Q342, Q343, Q344, Q345, Q346, Q347, Q348, Q349, Q350, Q351, Q352, Q353, Q354, Q355, Q356, Q357, Q358, Q359, Q360, Q361, Q362, Q363, Q364, Q365, Q366, Q367, Q368, Q369, Q370, Q371, Q372, Q373, Q374, Q375, Q376, Q377, Q378, Q379, Q380, Q381, Q382, Q383, Q384, Q385, Q386, Q387, Q388, Q389, Q390, Q391, Q392, Q393, Q394, Q395, Q396, Q397, Q398, Q399, Q400, Q401, Q402, Q403, Q404, Q405, Q406, Q407, Q408, Q409, Q410, Q411, Q412, Q413, Q414, Q415, Q416, Q417, Q418, Q419, Q420, Q421, Q422, Q423, Q424, Q425, Q426, Q427, Q428, Q429, Q430, Q431, Q432, Q433, Q434, Q435, Q436, Q437, Q438, Q439, Q440, Q441, Q442, Q443, Q444, Q445, Q446, Q447, Q448, Q449, Q450, Q451, Q452, Q453, Q454, Q455, Q456, Q457, Q458, Q459, Q460, Q461, Q462, Q463, Q464, Q465, Q466, Q467, Q468, Q469, Q470, Q471, Q472, Q473, Q474, Q475, Q476, Q477, Q478, Q479, Q480, Q481, Q482, Q483, Q484, Q485, Q486, Q487, Q488, Q489, Q490, Q491, Q492, Q493, Q494, Q495, Q496, Q497, Q498, Q499, Q500, Q501, Q502, Q503, Q504, Q505, Q506, Q507, Q508, Q509, Q510, Q511, Q512, Q513, Q514, Q515, Q516, Q517, Q518, Q519, Q520, Q521, Q522, Q523, Q524, Q525, Q526, Q527, Q528, Q529, Q530, Q531, Q532, Q533, Q534, Q535, Q536, Q537, Q538, Q539, Q540, Q541, Q542, Q543, Q544, Q545, Q546, Q547, Q548, Q549, Q550, Q551, Q552, Q553, Q554, Q555, Q556, Q557, Q558, Q559, Q560, Q561, Q562, Q563, Q564, Q565, Q566, Q567, Q568, Q569, Q570, Q571, Q572, Q573, Q574, Q575, Q576, Q577, Q578, Q579, Q580, Q581, Q582, Q583, Q584, Q585, Q586, Q587, Q588, Q589, Q590, Q591, Q592, Q593, Q594, Q595, Q596, Q597, Q598, Q599, Q600, Q601, Q602, Q603, Q604, Q605, Q606, Q607, Q608, Q609, Q610, Q611, Q612, Q613, Q614, Q615, Q616, Q617, Q618, Q619, Q620, Q621, Q622, Q623, Q624, Q625, Q626, Q627, Q628, Q629, Q630, Q631, Q632, Q633, Q634, Q635, Q636, Q637, Q638, Q639, Q640, Q641, Q642, Q643, Q644, Q645, Q646, Q647, Q648, Q649, Q650, Q651, Q652, Q653, Q654, Q655, Q656, Q657, Q658, Q659, Q660, Q661, Q662, Q663, Q664, Q665, Q666, Q667, Q668, Q669, Q670, Q671, Q672, Q673, Q674, Q675, Q676, Q677, Q678, Q679, Q680, Q681, Q682, Q683, Q684, Q685, Q686, Q687, Q688, Q689, Q690, Q691, Q692, Q693, Q694, Q695, Q696, Q697, Q698, Q699, Q700, Q701, Q702, Q703, Q704, Q705, Q706, Q707, Q708, Q709, Q710]), "width" : 0.2 * mm, "tangentPropagation" : true});
        }
    });
